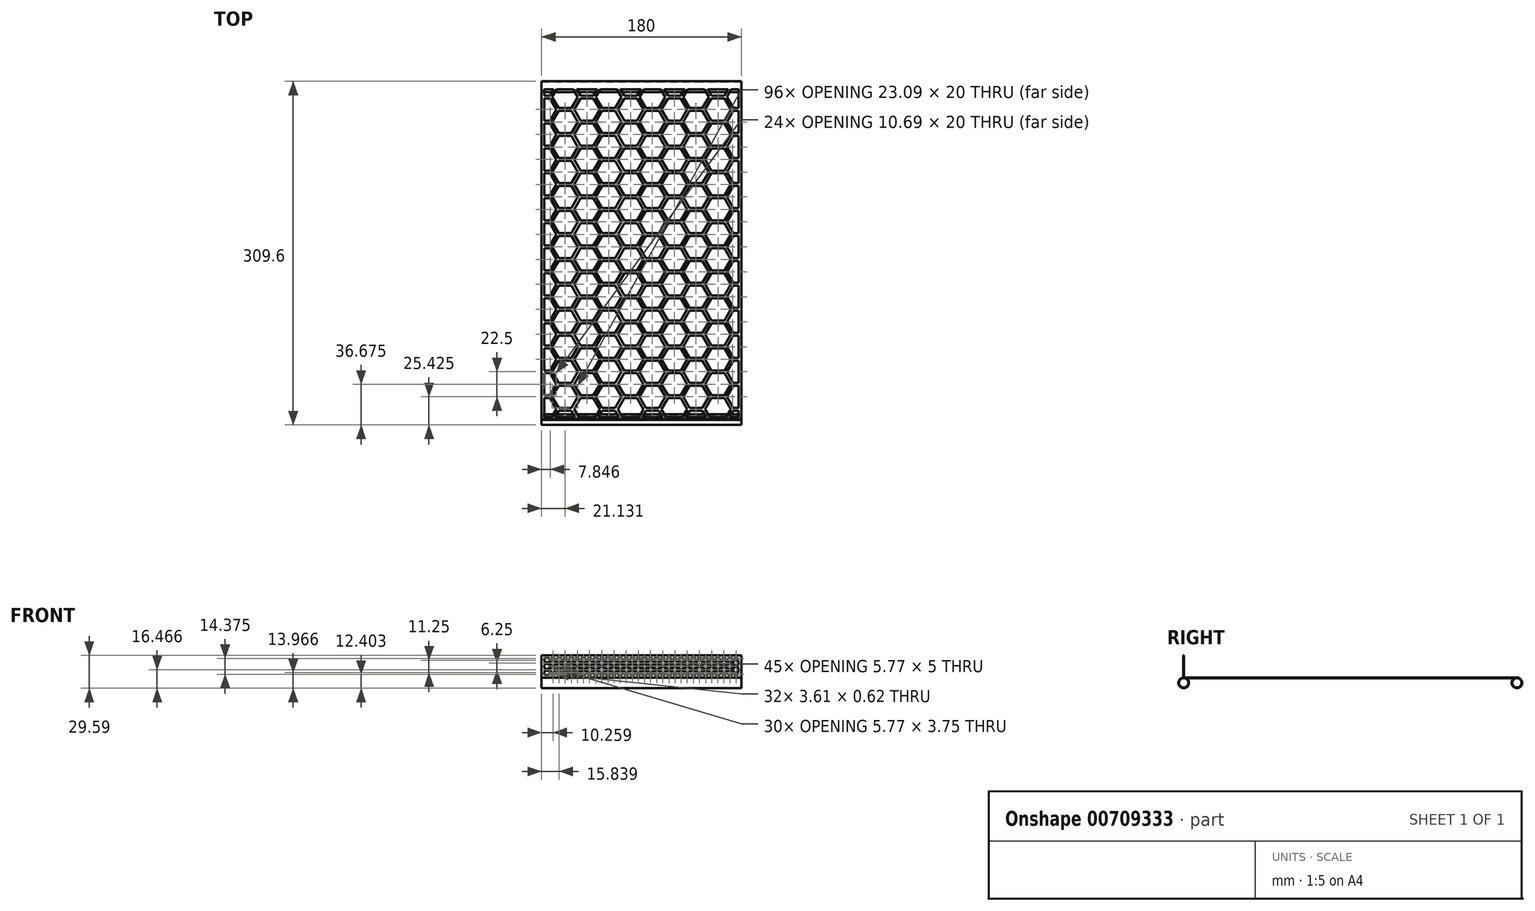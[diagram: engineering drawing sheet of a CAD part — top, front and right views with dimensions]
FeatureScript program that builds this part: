
annotation { "Feature Type Name" : "Feature", "Feature Type Description" : "" }
export const myFeature = defineFeature(function(context is Context, id is Id, definition is map)
    precondition{}
    {
        {
            var Q0;
            Q0=qCreatedBy(makeId("Top.planeOp"),FACE);
            var sketch = newSketch(context, id + "F0", { "sketchPlane" : qUnion([Q0])});
            skLineSegment(sketch, "E0.bottom", {"start": v(90, -150) * mm, "end": v(-90, -150) * mm});
            skLineSegment(sketch, "E0.top", {"start": v(90, 150) * mm, "end": v(-90, 150) * mm});
            skLineSegment(sketch, "E0.left", {"start": v(90, -150) * mm, "end": v(90, 150) * mm});
            skLineSegment(sketch, "E0.right", {"start": v(-90, -150) * mm, "end": v(-90, 150) * mm});
            skPoint(sketch, "E0.middle", {"position": v(0, 0) * mm});
            skSolve(sketch);
        }
        {
            var Q0;
            Q0 = qSketchRegion(id + "F0", true);
            extrude(context, id + "F1", {"entities" : qUnion([Q0]), "endBound" : BoundingType.SYMMETRIC, "depth" : 0.6 * mm, "offsetDistance" : 25 * mm});
        }
        {
            var Q0;
            Q0=qCreatedBy(makeId("Right.planeOp"),FACE);
            var sketch = newSketch(context, id + "F2", { "sketchPlane" : qUnion([Q0])});
            skLineSegment(sketch, "E1.0", {"start": v(-150, 0.3) * mm, "end": v(-150, -0.3) * mm, "construction": true});
            skCircle(sketch, "E2", {"center": v(-150, -4.5) * mm, "radius": 4.2 * mm});
            skCircle(sketch, "E3", {"center": v(-150, -4.5) * mm, "radius": 4.8 * mm});
            skCircle(sketch, "E4.MirrorC", {"center": v(150, -4.5) * mm, "radius": 4.8 * mm});
            skCircle(sketch, "E5.MirrorC", {"center": v(150, -4.5) * mm, "radius": 4.2 * mm});
            skLineSegment(sketch, "E6.bottom", {"start": v(-150.3, 0.3) * mm, "end": v(-149.7, 0.3) * mm});
            skLineSegment(sketch, "E6.top", {"start": v(-150.3, 20.3) * mm, "end": v(-149.7, 20.3) * mm});
            skLineSegment(sketch, "E6.left", {"start": v(-150.3, 0.3) * mm, "end": v(-150.3, 20.3) * mm});
            skLineSegment(sketch, "E6.right", {"start": v(-149.7, 0.3) * mm, "end": v(-149.7, 20.3) * mm});
            skPoint(sketch, "E7", {"position": v(-150, 0.3) * mm});
            skSolve(sketch);
        }
        {
            var Q0;
            Q0 = qSketchRegion(id + "F2", true);
            var Q1;
            Q1=makeQuery(id+"F1.opExtrude","CAP_EDGE",EDGE,{"disambiguationData":[OSD([sQuery(id+"F0.wireOp",EDGE,"E0.bottom")])],"isStart":false});
            sweep(context, id + "F3", {"operationType" : NewBodyOperationType.ADD, "profiles" : qUnion([Q0]), "path" : qUnion([Q1])});
        }
        {
            var Q0;
            Q0=makeQuery(id+"F1.opExtrude","CAP_FACE",FACE,{"disambiguationData":[OSD([sQuery(id+"F0.wireOp",EDGE,"E0.bottom"),sQuery(id+"F0.wireOp",EDGE,"E0.top"),sQuery(id+"F0.wireOp",EDGE,"E0.left"),sQuery(id+"F0.wireOp",EDGE,"E0.right")])],"isStart":false});
            var sketch = newSketch(context, id + "F4", { "sketchPlane" : qUnion([Q0])});
            skPoint(sketch, "E8.0", {"position": v(-90, 147.68) * mm});
            skPoint(sketch, "E9.0", {"position": v(-90, -147.68) * mm});
            skLineSegment(sketch, "E10", {"start": v(-90, 147.68) * mm, "end": v(90, 147.68) * mm});
            skLineSegment(sketch, "E11", {"start": v(-90, -147.68) * mm, "end": v(90, -147.68) * mm});
            skCircle(sketch, "E12.cCircle", {"center": v(-68.87, 163.12) * mm, "radius": 10 * mm, "construction": true});
            skLineSegment(sketch, "E12.0", {"start": v(-63.1, 153.12) * mm, "end": v(-74.64, 153.12) * mm});
            skLineSegment(sketch, "E12.1", {"start": v(-74.64, 153.12) * mm, "end": v(-80.42, 163.12) * mm});
            skLineSegment(sketch, "E12.2", {"start": v(-80.42, 163.12) * mm, "end": v(-74.64, 173.12) * mm});
            skLineSegment(sketch, "E12.3", {"start": v(-74.64, 173.12) * mm, "end": v(-63.1, 173.12) * mm});
            skLineSegment(sketch, "E12.4", {"start": v(-63.1, 173.12) * mm, "end": v(-57.32, 163.12) * mm});
            skLineSegment(sketch, "E12.5", {"start": v(-57.32, 163.12) * mm, "end": v(-63.1, 153.12) * mm});
            skPoint(sketch, "E12.0.midPoint", {"position": v(-68.87, 153.12) * mm});
            skCircle(sketch, "E13.cCircle", {"center": v(-88.35, 151.87) * mm, "radius": 10 * mm, "construction": true});
            skLineSegment(sketch, "E13.0", {"start": v(-82.58, 141.87) * mm, "end": v(-94.13, 141.87) * mm});
            skLineSegment(sketch, "E13.1", {"start": v(-94.13, 141.87) * mm, "end": v(-99.9, 151.87) * mm});
            skLineSegment(sketch, "E13.2", {"start": v(-99.9, 151.87) * mm, "end": v(-94.13, 161.87) * mm});
            skLineSegment(sketch, "E13.3", {"start": v(-94.13, 161.87) * mm, "end": v(-82.58, 161.87) * mm});
            skLineSegment(sketch, "E13.4", {"start": v(-82.58, 161.87) * mm, "end": v(-76.8, 151.87) * mm});
            skLineSegment(sketch, "E13.5", {"start": v(-76.8, 151.87) * mm, "end": v(-82.58, 141.87) * mm});
            skPoint(sketch, "E13.0.midPoint", {"position": v(-88.35, 141.87) * mm});
            skLineSegment(sketch, "E14.0", {"start": v(87.5, -149.7) * mm, "end": v(87.5, 150) * mm});
            skLineSegment(sketch, "E15.0", {"start": v(-87.5, -149.7) * mm, "end": v(-87.5, 150) * mm});
            skLineSegment(sketch, "E16", {"start": v(0, 147.68) * mm, "end": v(0, -147.68) * mm, "construction": true});
            skLineSegment(sketch, "E17", {"start": v(-87.5, 0) * mm, "end": v(87.5, 0) * mm, "construction": true});
            skLineSegment(sketch, "E18.0.1.0", {"start": v(-94.13, 139.37) * mm, "end": v(-82.58, 139.37) * mm});
            skLineSegment(sketch, "E18.0.1.1", {"start": v(-99.9, 129.37) * mm, "end": v(-94.13, 139.37) * mm});
            skLineSegment(sketch, "E18.0.1.2", {"start": v(-94.13, 119.37) * mm, "end": v(-99.9, 129.37) * mm});
            skLineSegment(sketch, "E18.0.1.3", {"start": v(-82.58, 119.37) * mm, "end": v(-94.13, 119.37) * mm});
            skLineSegment(sketch, "E18.0.1.4", {"start": v(-76.8, 129.37) * mm, "end": v(-82.58, 119.37) * mm});
            skLineSegment(sketch, "E18.0.1.5", {"start": v(-82.58, 139.37) * mm, "end": v(-76.8, 129.37) * mm});
            skLineSegment(sketch, "E18.0.1.6", {"start": v(-80.42, 140.62) * mm, "end": v(-74.64, 150.62) * mm});
            skLineSegment(sketch, "E18.0.1.7", {"start": v(-74.64, 130.62) * mm, "end": v(-80.42, 140.62) * mm});
            skLineSegment(sketch, "E18.0.1.8", {"start": v(-74.64, 150.62) * mm, "end": v(-63.1, 150.62) * mm});
            skLineSegment(sketch, "E18.0.1.9", {"start": v(-63.1, 150.62) * mm, "end": v(-57.32, 140.62) * mm});
            skLineSegment(sketch, "E18.0.1.10", {"start": v(-57.32, 140.62) * mm, "end": v(-63.1, 130.62) * mm});
            skLineSegment(sketch, "E18.0.1.11", {"start": v(-63.1, 130.62) * mm, "end": v(-74.64, 130.62) * mm});
            skLineSegment(sketch, "E18.1.0.0", {"start": v(-54.82, 161.87) * mm, "end": v(-43.28, 161.87) * mm});
            skLineSegment(sketch, "E18.1.0.1", {"start": v(-60.6, 151.87) * mm, "end": v(-54.82, 161.87) * mm});
            skLineSegment(sketch, "E18.1.0.2", {"start": v(-54.82, 141.87) * mm, "end": v(-60.6, 151.87) * mm});
            skLineSegment(sketch, "E18.1.0.3", {"start": v(-43.28, 141.87) * mm, "end": v(-54.82, 141.87) * mm});
            skLineSegment(sketch, "E18.1.0.4", {"start": v(-37.5, 151.87) * mm, "end": v(-43.28, 141.87) * mm});
            skLineSegment(sketch, "E18.1.0.5", {"start": v(-43.28, 161.87) * mm, "end": v(-37.5, 151.87) * mm});
            skLineSegment(sketch, "E18.1.0.6", {"start": v(-41.11, 163.12) * mm, "end": v(-35.34, 173.12) * mm});
            skLineSegment(sketch, "E18.1.0.7", {"start": v(-35.34, 153.12) * mm, "end": v(-41.11, 163.12) * mm});
            skLineSegment(sketch, "E18.1.0.8", {"start": v(-35.34, 173.12) * mm, "end": v(-23.79, 173.12) * mm});
            skLineSegment(sketch, "E18.1.0.9", {"start": v(-23.79, 173.12) * mm, "end": v(-18.02, 163.12) * mm});
            skLineSegment(sketch, "E18.1.0.10", {"start": v(-18.02, 163.12) * mm, "end": v(-23.79, 153.12) * mm});
            skLineSegment(sketch, "E18.1.0.11", {"start": v(-23.79, 153.12) * mm, "end": v(-35.34, 153.12) * mm});
            skLineSegment(sketch, "E18.1.1.0", {"start": v(-54.82, 139.37) * mm, "end": v(-43.28, 139.37) * mm});
            skLineSegment(sketch, "E18.1.1.1", {"start": v(-60.6, 129.37) * mm, "end": v(-54.82, 139.37) * mm});
            skLineSegment(sketch, "E18.1.1.2", {"start": v(-54.82, 119.37) * mm, "end": v(-60.6, 129.37) * mm});
            skLineSegment(sketch, "E18.1.1.3", {"start": v(-43.28, 119.37) * mm, "end": v(-54.82, 119.37) * mm});
            skLineSegment(sketch, "E18.1.1.4", {"start": v(-37.5, 129.37) * mm, "end": v(-43.28, 119.37) * mm});
            skLineSegment(sketch, "E18.1.1.5", {"start": v(-43.28, 139.37) * mm, "end": v(-37.5, 129.37) * mm});
            skLineSegment(sketch, "E18.1.1.6", {"start": v(-41.11, 140.62) * mm, "end": v(-35.34, 150.62) * mm});
            skLineSegment(sketch, "E18.1.1.7", {"start": v(-35.34, 130.62) * mm, "end": v(-41.11, 140.62) * mm});
            skLineSegment(sketch, "E18.1.1.8", {"start": v(-35.34, 150.62) * mm, "end": v(-23.79, 150.62) * mm});
            skLineSegment(sketch, "E18.1.1.9", {"start": v(-23.79, 150.62) * mm, "end": v(-18.02, 140.62) * mm});
            skLineSegment(sketch, "E18.1.1.10", {"start": v(-18.02, 140.62) * mm, "end": v(-23.79, 130.62) * mm});
            skLineSegment(sketch, "E18.1.1.11", {"start": v(-23.79, 130.62) * mm, "end": v(-35.34, 130.62) * mm});
            skLineSegment(sketch, "E18.2.0.0", {"start": v(-15.52, 161.87) * mm, "end": v(-3.97, 161.87) * mm});
            skLineSegment(sketch, "E18.2.0.1", {"start": v(-21.29, 151.87) * mm, "end": v(-15.52, 161.87) * mm});
            skLineSegment(sketch, "E18.2.0.2", {"start": v(-15.52, 141.87) * mm, "end": v(-21.29, 151.87) * mm});
            skLineSegment(sketch, "E18.2.0.3", {"start": v(-3.97, 141.87) * mm, "end": v(-15.52, 141.87) * mm});
            skLineSegment(sketch, "E18.2.0.4", {"start": v(1.8, 151.87) * mm, "end": v(-3.97, 141.87) * mm});
            skLineSegment(sketch, "E18.2.0.5", {"start": v(-3.97, 161.87) * mm, "end": v(1.8, 151.87) * mm});
            skLineSegment(sketch, "E18.2.0.6", {"start": v(-1.8, 163.12) * mm, "end": v(3.97, 173.12) * mm});
            skLineSegment(sketch, "E18.2.0.7", {"start": v(3.97, 153.12) * mm, "end": v(-1.8, 163.12) * mm});
            skLineSegment(sketch, "E18.2.0.8", {"start": v(3.97, 173.12) * mm, "end": v(15.52, 173.12) * mm});
            skLineSegment(sketch, "E18.2.0.9", {"start": v(15.52, 173.12) * mm, "end": v(21.29, 163.12) * mm});
            skLineSegment(sketch, "E18.2.0.10", {"start": v(21.29, 163.12) * mm, "end": v(15.52, 153.12) * mm});
            skLineSegment(sketch, "E18.2.0.11", {"start": v(15.52, 153.12) * mm, "end": v(3.97, 153.12) * mm});
            skLineSegment(sketch, "E18.2.1.0", {"start": v(-15.52, 139.37) * mm, "end": v(-3.97, 139.37) * mm});
            skLineSegment(sketch, "E18.2.1.1", {"start": v(-21.29, 129.37) * mm, "end": v(-15.52, 139.37) * mm});
            skLineSegment(sketch, "E18.2.1.2", {"start": v(-15.52, 119.37) * mm, "end": v(-21.29, 129.37) * mm});
            skLineSegment(sketch, "E18.2.1.3", {"start": v(-3.97, 119.37) * mm, "end": v(-15.52, 119.37) * mm});
            skLineSegment(sketch, "E18.2.1.4", {"start": v(1.8, 129.37) * mm, "end": v(-3.97, 119.37) * mm});
            skLineSegment(sketch, "E18.2.1.5", {"start": v(-3.97, 139.37) * mm, "end": v(1.8, 129.37) * mm});
            skLineSegment(sketch, "E18.2.1.6", {"start": v(-1.8, 140.62) * mm, "end": v(3.97, 150.62) * mm});
            skLineSegment(sketch, "E18.2.1.7", {"start": v(3.97, 130.62) * mm, "end": v(-1.8, 140.62) * mm});
            skLineSegment(sketch, "E18.2.1.8", {"start": v(3.97, 150.62) * mm, "end": v(15.52, 150.62) * mm});
            skLineSegment(sketch, "E18.2.1.9", {"start": v(15.52, 150.62) * mm, "end": v(21.29, 140.62) * mm});
            skLineSegment(sketch, "E18.2.1.10", {"start": v(21.29, 140.62) * mm, "end": v(15.52, 130.62) * mm});
            skLineSegment(sketch, "E18.2.1.11", {"start": v(15.52, 130.62) * mm, "end": v(3.97, 130.62) * mm});
            skLineSegment(sketch, "E18.direction1", {"start": v(-94.13, 161.87) * mm, "end": v(-54.82, 161.87) * mm, "construction": true});
            skLineSegment(sketch, "E18.direction2", {"start": v(-94.13, 161.87) * mm, "end": v(-94.13, 139.37) * mm, "construction": true});
            skLineSegment(sketch, "E19.0.3.0", {"start": v(23.79, 161.87) * mm, "end": v(35.34, 161.87) * mm});
            skLineSegment(sketch, "E19.3.3.0", {"start": v(18.02, 151.87) * mm, "end": v(23.79, 161.87) * mm});
            skLineSegment(sketch, "E19.6.3.0", {"start": v(23.79, 141.87) * mm, "end": v(18.02, 151.87) * mm});
            skLineSegment(sketch, "E19.9.3.0", {"start": v(35.34, 141.87) * mm, "end": v(23.79, 141.87) * mm});
            skLineSegment(sketch, "E19.12.3.0", {"start": v(41.11, 151.87) * mm, "end": v(35.34, 141.87) * mm});
            skLineSegment(sketch, "E19.15.3.0", {"start": v(35.34, 161.87) * mm, "end": v(41.11, 151.87) * mm});
            skLineSegment(sketch, "E19.18.3.0", {"start": v(37.5, 163.12) * mm, "end": v(43.28, 173.12) * mm});
            skLineSegment(sketch, "E19.21.3.0", {"start": v(43.28, 153.12) * mm, "end": v(37.5, 163.12) * mm});
            skLineSegment(sketch, "E19.24.3.0", {"start": v(43.28, 173.12) * mm, "end": v(54.82, 173.12) * mm});
            skLineSegment(sketch, "E19.27.3.0", {"start": v(54.82, 173.12) * mm, "end": v(60.6, 163.12) * mm});
            skLineSegment(sketch, "E19.30.3.0", {"start": v(60.6, 163.12) * mm, "end": v(54.82, 153.12) * mm});
            skLineSegment(sketch, "E19.33.3.0", {"start": v(54.82, 153.12) * mm, "end": v(43.28, 153.12) * mm});
            skLineSegment(sketch, "E19.0.3.1", {"start": v(23.79, 139.37) * mm, "end": v(35.34, 139.37) * mm});
            skLineSegment(sketch, "E19.3.3.1", {"start": v(18.02, 129.37) * mm, "end": v(23.79, 139.37) * mm});
            skLineSegment(sketch, "E19.6.3.1", {"start": v(23.79, 119.37) * mm, "end": v(18.02, 129.37) * mm});
            skLineSegment(sketch, "E19.9.3.1", {"start": v(35.34, 119.37) * mm, "end": v(23.79, 119.37) * mm});
            skLineSegment(sketch, "E19.12.3.1", {"start": v(41.11, 129.37) * mm, "end": v(35.34, 119.37) * mm});
            skLineSegment(sketch, "E19.15.3.1", {"start": v(35.34, 139.37) * mm, "end": v(41.11, 129.37) * mm});
            skLineSegment(sketch, "E19.18.3.1", {"start": v(37.5, 140.62) * mm, "end": v(43.28, 150.62) * mm});
            skLineSegment(sketch, "E19.21.3.1", {"start": v(43.28, 130.62) * mm, "end": v(37.5, 140.62) * mm});
            skLineSegment(sketch, "E19.24.3.1", {"start": v(43.28, 150.62) * mm, "end": v(54.82, 150.62) * mm});
            skLineSegment(sketch, "E19.27.3.1", {"start": v(54.82, 150.62) * mm, "end": v(60.6, 140.62) * mm});
            skLineSegment(sketch, "E19.30.3.1", {"start": v(60.6, 140.62) * mm, "end": v(54.82, 130.62) * mm});
            skLineSegment(sketch, "E19.33.3.1", {"start": v(54.82, 130.62) * mm, "end": v(43.28, 130.62) * mm});
            skLineSegment(sketch, "E19.0.4.0", {"start": v(63.1, 161.87) * mm, "end": v(74.64, 161.87) * mm});
            skLineSegment(sketch, "E19.3.4.0", {"start": v(57.32, 151.87) * mm, "end": v(63.1, 161.87) * mm});
            skLineSegment(sketch, "E19.6.4.0", {"start": v(63.1, 141.87) * mm, "end": v(57.32, 151.87) * mm});
            skLineSegment(sketch, "E19.9.4.0", {"start": v(74.64, 141.87) * mm, "end": v(63.1, 141.87) * mm});
            skLineSegment(sketch, "E19.12.4.0", {"start": v(80.42, 151.87) * mm, "end": v(74.64, 141.87) * mm});
            skLineSegment(sketch, "E19.15.4.0", {"start": v(74.64, 161.87) * mm, "end": v(80.42, 151.87) * mm});
            skLineSegment(sketch, "E19.18.4.0", {"start": v(76.8, 163.12) * mm, "end": v(82.58, 173.12) * mm});
            skLineSegment(sketch, "E19.21.4.0", {"start": v(82.58, 153.12) * mm, "end": v(76.8, 163.12) * mm});
            skLineSegment(sketch, "E19.24.4.0", {"start": v(82.58, 173.12) * mm, "end": v(94.13, 173.12) * mm});
            skLineSegment(sketch, "E19.27.4.0", {"start": v(94.13, 173.12) * mm, "end": v(99.9, 163.12) * mm});
            skLineSegment(sketch, "E19.30.4.0", {"start": v(99.9, 163.12) * mm, "end": v(94.13, 153.12) * mm});
            skLineSegment(sketch, "E19.33.4.0", {"start": v(94.13, 153.12) * mm, "end": v(82.58, 153.12) * mm});
            skLineSegment(sketch, "E19.0.4.1", {"start": v(63.1, 139.37) * mm, "end": v(74.64, 139.37) * mm});
            skLineSegment(sketch, "E19.3.4.1", {"start": v(57.32, 129.37) * mm, "end": v(63.1, 139.37) * mm});
            skLineSegment(sketch, "E19.6.4.1", {"start": v(63.1, 119.37) * mm, "end": v(57.32, 129.37) * mm});
            skLineSegment(sketch, "E19.9.4.1", {"start": v(74.64, 119.37) * mm, "end": v(63.1, 119.37) * mm});
            skLineSegment(sketch, "E19.12.4.1", {"start": v(80.42, 129.37) * mm, "end": v(74.64, 119.37) * mm});
            skLineSegment(sketch, "E19.15.4.1", {"start": v(74.64, 139.37) * mm, "end": v(80.42, 129.37) * mm});
            skLineSegment(sketch, "E19.18.4.1", {"start": v(76.8, 140.62) * mm, "end": v(82.58, 150.62) * mm});
            skLineSegment(sketch, "E19.21.4.1", {"start": v(82.58, 130.62) * mm, "end": v(76.8, 140.62) * mm});
            skLineSegment(sketch, "E19.24.4.1", {"start": v(82.58, 150.62) * mm, "end": v(94.13, 150.62) * mm});
            skLineSegment(sketch, "E19.27.4.1", {"start": v(94.13, 150.62) * mm, "end": v(99.9, 140.62) * mm});
            skLineSegment(sketch, "E19.30.4.1", {"start": v(99.9, 140.62) * mm, "end": v(94.13, 130.62) * mm});
            skLineSegment(sketch, "E19.33.4.1", {"start": v(94.13, 130.62) * mm, "end": v(82.58, 130.62) * mm});
            skLineSegment(sketch, "E20.0.0.2", {"start": v(-94.13, 116.87) * mm, "end": v(-82.58, 116.87) * mm});
            skLineSegment(sketch, "E20.3.0.2", {"start": v(-99.9, 106.87) * mm, "end": v(-94.13, 116.87) * mm});
            skLineSegment(sketch, "E20.6.0.2", {"start": v(-94.13, 96.87) * mm, "end": v(-99.9, 106.87) * mm});
            skLineSegment(sketch, "E20.9.0.2", {"start": v(-82.58, 96.87) * mm, "end": v(-94.13, 96.87) * mm});
            skLineSegment(sketch, "E20.12.0.2", {"start": v(-76.8, 106.87) * mm, "end": v(-82.58, 96.87) * mm});
            skLineSegment(sketch, "E20.15.0.2", {"start": v(-82.58, 116.87) * mm, "end": v(-76.8, 106.87) * mm});
            skLineSegment(sketch, "E20.18.0.2", {"start": v(-80.42, 118.12) * mm, "end": v(-74.64, 128.12) * mm});
            skLineSegment(sketch, "E20.21.0.2", {"start": v(-74.64, 108.12) * mm, "end": v(-80.42, 118.12) * mm});
            skLineSegment(sketch, "E20.24.0.2", {"start": v(-74.64, 128.12) * mm, "end": v(-63.1, 128.12) * mm});
            skLineSegment(sketch, "E20.27.0.2", {"start": v(-63.1, 128.12) * mm, "end": v(-57.32, 118.12) * mm});
            skLineSegment(sketch, "E20.30.0.2", {"start": v(-57.32, 118.12) * mm, "end": v(-63.1, 108.12) * mm});
            skLineSegment(sketch, "E20.33.0.2", {"start": v(-63.1, 108.12) * mm, "end": v(-74.64, 108.12) * mm});
            skLineSegment(sketch, "E20.0.0.3", {"start": v(-94.13, 94.37) * mm, "end": v(-82.58, 94.37) * mm});
            skLineSegment(sketch, "E20.3.0.3", {"start": v(-99.9, 84.37) * mm, "end": v(-94.13, 94.37) * mm});
            skLineSegment(sketch, "E20.6.0.3", {"start": v(-94.13, 74.37) * mm, "end": v(-99.9, 84.37) * mm});
            skLineSegment(sketch, "E20.9.0.3", {"start": v(-82.58, 74.37) * mm, "end": v(-94.13, 74.37) * mm});
            skLineSegment(sketch, "E20.12.0.3", {"start": v(-76.8, 84.37) * mm, "end": v(-82.58, 74.37) * mm});
            skLineSegment(sketch, "E20.15.0.3", {"start": v(-82.58, 94.37) * mm, "end": v(-76.8, 84.37) * mm});
            skLineSegment(sketch, "E20.18.0.3", {"start": v(-80.42, 95.62) * mm, "end": v(-74.64, 105.62) * mm});
            skLineSegment(sketch, "E20.21.0.3", {"start": v(-74.64, 85.62) * mm, "end": v(-80.42, 95.62) * mm});
            skLineSegment(sketch, "E20.24.0.3", {"start": v(-74.64, 105.62) * mm, "end": v(-63.1, 105.62) * mm});
            skLineSegment(sketch, "E20.27.0.3", {"start": v(-63.1, 105.62) * mm, "end": v(-57.32, 95.62) * mm});
            skLineSegment(sketch, "E20.30.0.3", {"start": v(-57.32, 95.62) * mm, "end": v(-63.1, 85.62) * mm});
            skLineSegment(sketch, "E20.33.0.3", {"start": v(-63.1, 85.62) * mm, "end": v(-74.64, 85.62) * mm});
            skLineSegment(sketch, "E20.0.0.4", {"start": v(-94.13, 71.87) * mm, "end": v(-82.58, 71.87) * mm});
            skLineSegment(sketch, "E20.3.0.4", {"start": v(-99.9, 61.87) * mm, "end": v(-94.13, 71.87) * mm});
            skLineSegment(sketch, "E20.6.0.4", {"start": v(-94.13, 51.87) * mm, "end": v(-99.9, 61.87) * mm});
            skLineSegment(sketch, "E20.9.0.4", {"start": v(-82.58, 51.87) * mm, "end": v(-94.13, 51.87) * mm});
            skLineSegment(sketch, "E20.12.0.4", {"start": v(-76.8, 61.87) * mm, "end": v(-82.58, 51.87) * mm});
            skLineSegment(sketch, "E20.15.0.4", {"start": v(-82.58, 71.87) * mm, "end": v(-76.8, 61.87) * mm});
            skLineSegment(sketch, "E20.18.0.4", {"start": v(-80.42, 73.12) * mm, "end": v(-74.64, 83.12) * mm});
            skLineSegment(sketch, "E20.21.0.4", {"start": v(-74.64, 63.12) * mm, "end": v(-80.42, 73.12) * mm});
            skLineSegment(sketch, "E20.24.0.4", {"start": v(-74.64, 83.12) * mm, "end": v(-63.1, 83.12) * mm});
            skLineSegment(sketch, "E20.27.0.4", {"start": v(-63.1, 83.12) * mm, "end": v(-57.32, 73.12) * mm});
            skLineSegment(sketch, "E20.30.0.4", {"start": v(-57.32, 73.12) * mm, "end": v(-63.1, 63.12) * mm});
            skLineSegment(sketch, "E20.33.0.4", {"start": v(-63.1, 63.12) * mm, "end": v(-74.64, 63.12) * mm});
            skLineSegment(sketch, "E20.0.0.5", {"start": v(-94.13, 49.37) * mm, "end": v(-82.58, 49.37) * mm});
            skLineSegment(sketch, "E20.3.0.5", {"start": v(-99.9, 39.37) * mm, "end": v(-94.13, 49.37) * mm});
            skLineSegment(sketch, "E20.6.0.5", {"start": v(-94.13, 29.37) * mm, "end": v(-99.9, 39.37) * mm});
            skLineSegment(sketch, "E20.9.0.5", {"start": v(-82.58, 29.37) * mm, "end": v(-94.13, 29.37) * mm});
            skLineSegment(sketch, "E20.12.0.5", {"start": v(-76.8, 39.37) * mm, "end": v(-82.58, 29.37) * mm});
            skLineSegment(sketch, "E20.15.0.5", {"start": v(-82.58, 49.37) * mm, "end": v(-76.8, 39.37) * mm});
            skLineSegment(sketch, "E20.18.0.5", {"start": v(-80.42, 50.62) * mm, "end": v(-74.64, 60.62) * mm});
            skLineSegment(sketch, "E20.21.0.5", {"start": v(-74.64, 40.62) * mm, "end": v(-80.42, 50.62) * mm});
            skLineSegment(sketch, "E20.24.0.5", {"start": v(-74.64, 60.62) * mm, "end": v(-63.1, 60.62) * mm});
            skLineSegment(sketch, "E20.27.0.5", {"start": v(-63.1, 60.62) * mm, "end": v(-57.32, 50.62) * mm});
            skLineSegment(sketch, "E20.30.0.5", {"start": v(-57.32, 50.62) * mm, "end": v(-63.1, 40.62) * mm});
            skLineSegment(sketch, "E20.33.0.5", {"start": v(-63.1, 40.62) * mm, "end": v(-74.64, 40.62) * mm});
            skLineSegment(sketch, "E20.0.0.6", {"start": v(-94.13, 26.87) * mm, "end": v(-82.58, 26.87) * mm});
            skLineSegment(sketch, "E20.3.0.6", {"start": v(-99.9, 16.87) * mm, "end": v(-94.13, 26.87) * mm});
            skLineSegment(sketch, "E20.6.0.6", {"start": v(-94.13, 6.87) * mm, "end": v(-99.9, 16.87) * mm});
            skLineSegment(sketch, "E20.9.0.6", {"start": v(-82.58, 6.87) * mm, "end": v(-94.13, 6.87) * mm});
            skLineSegment(sketch, "E20.12.0.6", {"start": v(-76.8, 16.87) * mm, "end": v(-82.58, 6.87) * mm});
            skLineSegment(sketch, "E20.15.0.6", {"start": v(-82.58, 26.87) * mm, "end": v(-76.8, 16.87) * mm});
            skLineSegment(sketch, "E20.18.0.6", {"start": v(-80.42, 28.12) * mm, "end": v(-74.64, 38.12) * mm});
            skLineSegment(sketch, "E20.21.0.6", {"start": v(-74.64, 18.12) * mm, "end": v(-80.42, 28.12) * mm});
            skLineSegment(sketch, "E20.24.0.6", {"start": v(-74.64, 38.12) * mm, "end": v(-63.1, 38.12) * mm});
            skLineSegment(sketch, "E20.27.0.6", {"start": v(-63.1, 38.12) * mm, "end": v(-57.32, 28.12) * mm});
            skLineSegment(sketch, "E20.30.0.6", {"start": v(-57.32, 28.12) * mm, "end": v(-63.1, 18.12) * mm});
            skLineSegment(sketch, "E20.33.0.6", {"start": v(-63.1, 18.12) * mm, "end": v(-74.64, 18.12) * mm});
            skLineSegment(sketch, "E20.0.0.7", {"start": v(-94.13, 4.37) * mm, "end": v(-82.58, 4.37) * mm});
            skLineSegment(sketch, "E20.3.0.7", {"start": v(-99.9, -5.63) * mm, "end": v(-94.13, 4.37) * mm});
            skLineSegment(sketch, "E20.6.0.7", {"start": v(-94.13, -15.63) * mm, "end": v(-99.9, -5.63) * mm});
            skLineSegment(sketch, "E20.9.0.7", {"start": v(-82.58, -15.63) * mm, "end": v(-94.13, -15.63) * mm});
            skLineSegment(sketch, "E20.12.0.7", {"start": v(-76.8, -5.63) * mm, "end": v(-82.58, -15.63) * mm});
            skLineSegment(sketch, "E20.15.0.7", {"start": v(-82.58, 4.37) * mm, "end": v(-76.8, -5.63) * mm});
            skLineSegment(sketch, "E20.18.0.7", {"start": v(-80.42, 5.62) * mm, "end": v(-74.64, 15.62) * mm});
            skLineSegment(sketch, "E20.21.0.7", {"start": v(-74.64, -4.38) * mm, "end": v(-80.42, 5.62) * mm});
            skLineSegment(sketch, "E20.24.0.7", {"start": v(-74.64, 15.62) * mm, "end": v(-63.1, 15.62) * mm});
            skLineSegment(sketch, "E20.27.0.7", {"start": v(-63.1, 15.62) * mm, "end": v(-57.32, 5.62) * mm});
            skLineSegment(sketch, "E20.30.0.7", {"start": v(-57.32, 5.62) * mm, "end": v(-63.1, -4.38) * mm});
            skLineSegment(sketch, "E20.33.0.7", {"start": v(-63.1, -4.38) * mm, "end": v(-74.64, -4.38) * mm});
            skLineSegment(sketch, "E20.0.0.8", {"start": v(-94.13, -18.13) * mm, "end": v(-82.58, -18.13) * mm});
            skLineSegment(sketch, "E20.3.0.8", {"start": v(-99.9, -28.13) * mm, "end": v(-94.13, -18.13) * mm});
            skLineSegment(sketch, "E20.6.0.8", {"start": v(-94.13, -38.13) * mm, "end": v(-99.9, -28.13) * mm});
            skLineSegment(sketch, "E20.9.0.8", {"start": v(-82.58, -38.13) * mm, "end": v(-94.13, -38.13) * mm});
            skLineSegment(sketch, "E20.12.0.8", {"start": v(-76.8, -28.13) * mm, "end": v(-82.58, -38.13) * mm});
            skLineSegment(sketch, "E20.15.0.8", {"start": v(-82.58, -18.13) * mm, "end": v(-76.8, -28.13) * mm});
            skLineSegment(sketch, "E20.18.0.8", {"start": v(-80.42, -16.88) * mm, "end": v(-74.64, -6.88) * mm});
            skLineSegment(sketch, "E20.21.0.8", {"start": v(-74.64, -26.88) * mm, "end": v(-80.42, -16.88) * mm});
            skLineSegment(sketch, "E20.24.0.8", {"start": v(-74.64, -6.88) * mm, "end": v(-63.1, -6.88) * mm});
            skLineSegment(sketch, "E20.27.0.8", {"start": v(-63.1, -6.88) * mm, "end": v(-57.32, -16.88) * mm});
            skLineSegment(sketch, "E20.30.0.8", {"start": v(-57.32, -16.88) * mm, "end": v(-63.1, -26.88) * mm});
            skLineSegment(sketch, "E20.33.0.8", {"start": v(-63.1, -26.88) * mm, "end": v(-74.64, -26.88) * mm});
            skLineSegment(sketch, "E20.0.0.9", {"start": v(-94.13, -40.63) * mm, "end": v(-82.58, -40.63) * mm});
            skLineSegment(sketch, "E20.3.0.9", {"start": v(-99.9, -50.63) * mm, "end": v(-94.13, -40.63) * mm});
            skLineSegment(sketch, "E20.6.0.9", {"start": v(-94.13, -60.63) * mm, "end": v(-99.9, -50.63) * mm});
            skLineSegment(sketch, "E20.9.0.9", {"start": v(-82.58, -60.63) * mm, "end": v(-94.13, -60.63) * mm});
            skLineSegment(sketch, "E20.12.0.9", {"start": v(-76.8, -50.63) * mm, "end": v(-82.58, -60.63) * mm});
            skLineSegment(sketch, "E20.15.0.9", {"start": v(-82.58, -40.63) * mm, "end": v(-76.8, -50.63) * mm});
            skLineSegment(sketch, "E20.18.0.9", {"start": v(-80.42, -39.38) * mm, "end": v(-74.64, -29.38) * mm});
            skLineSegment(sketch, "E20.21.0.9", {"start": v(-74.64, -49.38) * mm, "end": v(-80.42, -39.38) * mm});
            skLineSegment(sketch, "E20.24.0.9", {"start": v(-74.64, -29.38) * mm, "end": v(-63.1, -29.38) * mm});
            skLineSegment(sketch, "E20.27.0.9", {"start": v(-63.1, -29.38) * mm, "end": v(-57.32, -39.38) * mm});
            skLineSegment(sketch, "E20.30.0.9", {"start": v(-57.32, -39.38) * mm, "end": v(-63.1, -49.38) * mm});
            skLineSegment(sketch, "E20.33.0.9", {"start": v(-63.1, -49.38) * mm, "end": v(-74.64, -49.38) * mm});
            skLineSegment(sketch, "E20.0.0.10", {"start": v(-94.13, -63.13) * mm, "end": v(-82.58, -63.13) * mm});
            skLineSegment(sketch, "E20.3.0.10", {"start": v(-99.9, -73.13) * mm, "end": v(-94.13, -63.13) * mm});
            skLineSegment(sketch, "E20.6.0.10", {"start": v(-94.13, -83.13) * mm, "end": v(-99.9, -73.13) * mm});
            skLineSegment(sketch, "E20.9.0.10", {"start": v(-82.58, -83.13) * mm, "end": v(-94.13, -83.13) * mm});
            skLineSegment(sketch, "E20.12.0.10", {"start": v(-76.8, -73.13) * mm, "end": v(-82.58, -83.13) * mm});
            skLineSegment(sketch, "E20.15.0.10", {"start": v(-82.58, -63.13) * mm, "end": v(-76.8, -73.13) * mm});
            skLineSegment(sketch, "E20.18.0.10", {"start": v(-80.42, -61.88) * mm, "end": v(-74.64, -51.88) * mm});
            skLineSegment(sketch, "E20.21.0.10", {"start": v(-74.64, -71.88) * mm, "end": v(-80.42, -61.88) * mm});
            skLineSegment(sketch, "E20.24.0.10", {"start": v(-74.64, -51.88) * mm, "end": v(-63.1, -51.88) * mm});
            skLineSegment(sketch, "E20.27.0.10", {"start": v(-63.1, -51.88) * mm, "end": v(-57.32, -61.88) * mm});
            skLineSegment(sketch, "E20.30.0.10", {"start": v(-57.32, -61.88) * mm, "end": v(-63.1, -71.88) * mm});
            skLineSegment(sketch, "E20.33.0.10", {"start": v(-63.1, -71.88) * mm, "end": v(-74.64, -71.88) * mm});
            skLineSegment(sketch, "E20.0.0.11", {"start": v(-94.13, -85.63) * mm, "end": v(-82.58, -85.63) * mm});
            skLineSegment(sketch, "E20.3.0.11", {"start": v(-99.9, -95.63) * mm, "end": v(-94.13, -85.63) * mm});
            skLineSegment(sketch, "E20.6.0.11", {"start": v(-94.13, -105.63) * mm, "end": v(-99.9, -95.63) * mm});
            skLineSegment(sketch, "E20.9.0.11", {"start": v(-82.58, -105.63) * mm, "end": v(-94.13, -105.63) * mm});
            skLineSegment(sketch, "E20.12.0.11", {"start": v(-76.8, -95.63) * mm, "end": v(-82.58, -105.63) * mm});
            skLineSegment(sketch, "E20.15.0.11", {"start": v(-82.58, -85.62) * mm, "end": v(-76.8, -95.63) * mm});
            skLineSegment(sketch, "E20.18.0.11", {"start": v(-80.42, -84.38) * mm, "end": v(-74.64, -74.38) * mm});
            skLineSegment(sketch, "E20.21.0.11", {"start": v(-74.64, -94.38) * mm, "end": v(-80.42, -84.38) * mm});
            skLineSegment(sketch, "E20.24.0.11", {"start": v(-74.64, -74.38) * mm, "end": v(-63.1, -74.38) * mm});
            skLineSegment(sketch, "E20.27.0.11", {"start": v(-63.1, -74.38) * mm, "end": v(-57.32, -84.38) * mm});
            skLineSegment(sketch, "E20.30.0.11", {"start": v(-57.32, -84.38) * mm, "end": v(-63.1, -94.38) * mm});
            skLineSegment(sketch, "E20.33.0.11", {"start": v(-63.1, -94.38) * mm, "end": v(-74.64, -94.38) * mm});
            skLineSegment(sketch, "E20.0.0.12", {"start": v(-94.13, -108.13) * mm, "end": v(-82.58, -108.13) * mm});
            skLineSegment(sketch, "E20.3.0.12", {"start": v(-99.9, -118.13) * mm, "end": v(-94.13, -108.13) * mm});
            skLineSegment(sketch, "E20.6.0.12", {"start": v(-94.13, -128.13) * mm, "end": v(-99.9, -118.13) * mm});
            skLineSegment(sketch, "E20.9.0.12", {"start": v(-82.58, -128.13) * mm, "end": v(-94.13, -128.13) * mm});
            skLineSegment(sketch, "E20.12.0.12", {"start": v(-76.8, -118.13) * mm, "end": v(-82.58, -128.13) * mm});
            skLineSegment(sketch, "E20.15.0.12", {"start": v(-82.58, -108.13) * mm, "end": v(-76.8, -118.13) * mm});
            skLineSegment(sketch, "E20.18.0.12", {"start": v(-80.42, -106.88) * mm, "end": v(-74.64, -96.88) * mm});
            skLineSegment(sketch, "E20.21.0.12", {"start": v(-74.64, -116.87) * mm, "end": v(-80.42, -106.88) * mm});
            skLineSegment(sketch, "E20.24.0.12", {"start": v(-74.64, -96.88) * mm, "end": v(-63.1, -96.88) * mm});
            skLineSegment(sketch, "E20.27.0.12", {"start": v(-63.1, -96.88) * mm, "end": v(-57.32, -106.88) * mm});
            skLineSegment(sketch, "E20.30.0.12", {"start": v(-57.32, -106.88) * mm, "end": v(-63.1, -116.88) * mm});
            skLineSegment(sketch, "E20.33.0.12", {"start": v(-63.1, -116.88) * mm, "end": v(-74.64, -116.88) * mm});
            skLineSegment(sketch, "E20.0.0.13", {"start": v(-94.13, -130.62) * mm, "end": v(-82.58, -130.62) * mm});
            skLineSegment(sketch, "E20.3.0.13", {"start": v(-99.9, -140.63) * mm, "end": v(-94.13, -130.63) * mm});
            skLineSegment(sketch, "E20.6.0.13", {"start": v(-94.13, -150.63) * mm, "end": v(-99.9, -140.63) * mm});
            skLineSegment(sketch, "E20.9.0.13", {"start": v(-82.58, -150.62) * mm, "end": v(-94.13, -150.62) * mm});
            skLineSegment(sketch, "E20.12.0.13", {"start": v(-76.8, -140.62) * mm, "end": v(-82.58, -150.62) * mm});
            skLineSegment(sketch, "E20.15.0.13", {"start": v(-82.58, -130.62) * mm, "end": v(-76.8, -140.62) * mm});
            skLineSegment(sketch, "E20.18.0.13", {"start": v(-80.42, -129.38) * mm, "end": v(-74.64, -119.38) * mm});
            skLineSegment(sketch, "E20.21.0.13", {"start": v(-74.64, -139.37) * mm, "end": v(-80.42, -129.38) * mm});
            skLineSegment(sketch, "E20.24.0.13", {"start": v(-74.64, -119.37) * mm, "end": v(-63.1, -119.37) * mm});
            skLineSegment(sketch, "E20.27.0.13", {"start": v(-63.1, -119.38) * mm, "end": v(-57.32, -129.37) * mm});
            skLineSegment(sketch, "E20.30.0.13", {"start": v(-57.32, -129.38) * mm, "end": v(-63.1, -139.38) * mm});
            skLineSegment(sketch, "E20.33.0.13", {"start": v(-63.1, -139.38) * mm, "end": v(-74.64, -139.38) * mm});
            skLineSegment(sketch, "E20.0.0.14", {"start": v(-94.13, -153.12) * mm, "end": v(-82.58, -153.12) * mm});
            skLineSegment(sketch, "E20.3.0.14", {"start": v(-99.9, -163.13) * mm, "end": v(-94.13, -153.13) * mm});
            skLineSegment(sketch, "E20.6.0.14", {"start": v(-94.13, -173.13) * mm, "end": v(-99.9, -163.13) * mm});
            skLineSegment(sketch, "E20.9.0.14", {"start": v(-82.58, -173.12) * mm, "end": v(-94.13, -173.12) * mm});
            skLineSegment(sketch, "E20.12.0.14", {"start": v(-76.8, -163.13) * mm, "end": v(-82.58, -173.12) * mm});
            skLineSegment(sketch, "E20.15.0.14", {"start": v(-82.58, -153.12) * mm, "end": v(-76.8, -163.12) * mm});
            skLineSegment(sketch, "E20.18.0.14", {"start": v(-80.42, -151.88) * mm, "end": v(-74.64, -141.88) * mm});
            skLineSegment(sketch, "E20.21.0.14", {"start": v(-74.64, -161.87) * mm, "end": v(-80.42, -151.88) * mm});
            skLineSegment(sketch, "E20.24.0.14", {"start": v(-74.64, -141.88) * mm, "end": v(-63.1, -141.88) * mm});
            skLineSegment(sketch, "E20.27.0.14", {"start": v(-63.1, -141.88) * mm, "end": v(-57.32, -151.87) * mm});
            skLineSegment(sketch, "E20.30.0.14", {"start": v(-57.32, -151.88) * mm, "end": v(-63.1, -161.88) * mm});
            skLineSegment(sketch, "E20.33.0.14", {"start": v(-63.1, -161.88) * mm, "end": v(-74.64, -161.88) * mm});
            skLineSegment(sketch, "E20.0.1.2", {"start": v(-54.82, 116.87) * mm, "end": v(-43.28, 116.87) * mm});
            skLineSegment(sketch, "E20.3.1.2", {"start": v(-60.6, 106.87) * mm, "end": v(-54.82, 116.87) * mm});
            skLineSegment(sketch, "E20.6.1.2", {"start": v(-54.82, 96.87) * mm, "end": v(-60.6, 106.87) * mm});
            skLineSegment(sketch, "E20.9.1.2", {"start": v(-43.28, 96.87) * mm, "end": v(-54.82, 96.87) * mm});
            skLineSegment(sketch, "E20.12.1.2", {"start": v(-37.5, 106.87) * mm, "end": v(-43.28, 96.87) * mm});
            skLineSegment(sketch, "E20.15.1.2", {"start": v(-43.28, 116.87) * mm, "end": v(-37.5, 106.87) * mm});
            skLineSegment(sketch, "E20.18.1.2", {"start": v(-41.11, 118.12) * mm, "end": v(-35.34, 128.12) * mm});
            skLineSegment(sketch, "E20.21.1.2", {"start": v(-35.34, 108.12) * mm, "end": v(-41.11, 118.12) * mm});
            skLineSegment(sketch, "E20.24.1.2", {"start": v(-35.34, 128.12) * mm, "end": v(-23.79, 128.12) * mm});
            skLineSegment(sketch, "E20.27.1.2", {"start": v(-23.79, 128.12) * mm, "end": v(-18.02, 118.12) * mm});
            skLineSegment(sketch, "E20.30.1.2", {"start": v(-18.02, 118.12) * mm, "end": v(-23.79, 108.12) * mm});
            skLineSegment(sketch, "E20.33.1.2", {"start": v(-23.79, 108.12) * mm, "end": v(-35.34, 108.12) * mm});
            skLineSegment(sketch, "E20.0.1.3", {"start": v(-54.82, 94.37) * mm, "end": v(-43.28, 94.37) * mm});
            skLineSegment(sketch, "E20.3.1.3", {"start": v(-60.6, 84.37) * mm, "end": v(-54.82, 94.37) * mm});
            skLineSegment(sketch, "E20.6.1.3", {"start": v(-54.82, 74.37) * mm, "end": v(-60.6, 84.37) * mm});
            skLineSegment(sketch, "E20.9.1.3", {"start": v(-43.28, 74.37) * mm, "end": v(-54.82, 74.37) * mm});
            skLineSegment(sketch, "E20.12.1.3", {"start": v(-37.5, 84.37) * mm, "end": v(-43.28, 74.37) * mm});
            skLineSegment(sketch, "E20.15.1.3", {"start": v(-43.28, 94.37) * mm, "end": v(-37.5, 84.37) * mm});
            skLineSegment(sketch, "E20.18.1.3", {"start": v(-41.11, 95.62) * mm, "end": v(-35.34, 105.62) * mm});
            skLineSegment(sketch, "E20.21.1.3", {"start": v(-35.34, 85.62) * mm, "end": v(-41.11, 95.62) * mm});
            skLineSegment(sketch, "E20.24.1.3", {"start": v(-35.34, 105.62) * mm, "end": v(-23.79, 105.62) * mm});
            skLineSegment(sketch, "E20.27.1.3", {"start": v(-23.79, 105.62) * mm, "end": v(-18.02, 95.62) * mm});
            skLineSegment(sketch, "E20.30.1.3", {"start": v(-18.02, 95.62) * mm, "end": v(-23.79, 85.62) * mm});
            skLineSegment(sketch, "E20.33.1.3", {"start": v(-23.79, 85.62) * mm, "end": v(-35.34, 85.62) * mm});
            skLineSegment(sketch, "E20.0.1.4", {"start": v(-54.82, 71.87) * mm, "end": v(-43.28, 71.87) * mm});
            skLineSegment(sketch, "E20.3.1.4", {"start": v(-60.6, 61.87) * mm, "end": v(-54.82, 71.87) * mm});
            skLineSegment(sketch, "E20.6.1.4", {"start": v(-54.82, 51.87) * mm, "end": v(-60.6, 61.87) * mm});
            skLineSegment(sketch, "E20.9.1.4", {"start": v(-43.28, 51.87) * mm, "end": v(-54.82, 51.87) * mm});
            skLineSegment(sketch, "E20.12.1.4", {"start": v(-37.5, 61.87) * mm, "end": v(-43.28, 51.87) * mm});
            skLineSegment(sketch, "E20.15.1.4", {"start": v(-43.28, 71.87) * mm, "end": v(-37.5, 61.87) * mm});
            skLineSegment(sketch, "E20.18.1.4", {"start": v(-41.11, 73.12) * mm, "end": v(-35.34, 83.12) * mm});
            skLineSegment(sketch, "E20.21.1.4", {"start": v(-35.34, 63.12) * mm, "end": v(-41.11, 73.12) * mm});
            skLineSegment(sketch, "E20.24.1.4", {"start": v(-35.34, 83.12) * mm, "end": v(-23.79, 83.12) * mm});
            skLineSegment(sketch, "E20.27.1.4", {"start": v(-23.79, 83.12) * mm, "end": v(-18.02, 73.12) * mm});
            skLineSegment(sketch, "E20.30.1.4", {"start": v(-18.02, 73.12) * mm, "end": v(-23.79, 63.12) * mm});
            skLineSegment(sketch, "E20.33.1.4", {"start": v(-23.79, 63.12) * mm, "end": v(-35.34, 63.12) * mm});
            skLineSegment(sketch, "E20.0.1.5", {"start": v(-54.82, 49.37) * mm, "end": v(-43.28, 49.37) * mm});
            skLineSegment(sketch, "E20.3.1.5", {"start": v(-60.6, 39.37) * mm, "end": v(-54.82, 49.37) * mm});
            skLineSegment(sketch, "E20.6.1.5", {"start": v(-54.82, 29.37) * mm, "end": v(-60.6, 39.37) * mm});
            skLineSegment(sketch, "E20.9.1.5", {"start": v(-43.28, 29.37) * mm, "end": v(-54.82, 29.37) * mm});
            skLineSegment(sketch, "E20.12.1.5", {"start": v(-37.5, 39.37) * mm, "end": v(-43.28, 29.37) * mm});
            skLineSegment(sketch, "E20.15.1.5", {"start": v(-43.28, 49.37) * mm, "end": v(-37.5, 39.37) * mm});
            skLineSegment(sketch, "E20.18.1.5", {"start": v(-41.11, 50.62) * mm, "end": v(-35.34, 60.62) * mm});
            skLineSegment(sketch, "E20.21.1.5", {"start": v(-35.34, 40.62) * mm, "end": v(-41.11, 50.62) * mm});
            skLineSegment(sketch, "E20.24.1.5", {"start": v(-35.34, 60.62) * mm, "end": v(-23.79, 60.62) * mm});
            skLineSegment(sketch, "E20.27.1.5", {"start": v(-23.79, 60.62) * mm, "end": v(-18.02, 50.62) * mm});
            skLineSegment(sketch, "E20.30.1.5", {"start": v(-18.02, 50.62) * mm, "end": v(-23.79, 40.62) * mm});
            skLineSegment(sketch, "E20.33.1.5", {"start": v(-23.79, 40.62) * mm, "end": v(-35.34, 40.62) * mm});
            skLineSegment(sketch, "E20.0.1.6", {"start": v(-54.82, 26.87) * mm, "end": v(-43.28, 26.87) * mm});
            skLineSegment(sketch, "E20.3.1.6", {"start": v(-60.6, 16.87) * mm, "end": v(-54.82, 26.87) * mm});
            skLineSegment(sketch, "E20.6.1.6", {"start": v(-54.82, 6.87) * mm, "end": v(-60.6, 16.87) * mm});
            skLineSegment(sketch, "E20.9.1.6", {"start": v(-43.28, 6.87) * mm, "end": v(-54.82, 6.87) * mm});
            skLineSegment(sketch, "E20.12.1.6", {"start": v(-37.5, 16.87) * mm, "end": v(-43.28, 6.87) * mm});
            skLineSegment(sketch, "E20.15.1.6", {"start": v(-43.28, 26.87) * mm, "end": v(-37.5, 16.87) * mm});
            skLineSegment(sketch, "E20.18.1.6", {"start": v(-41.11, 28.12) * mm, "end": v(-35.34, 38.12) * mm});
            skLineSegment(sketch, "E20.21.1.6", {"start": v(-35.34, 18.12) * mm, "end": v(-41.11, 28.12) * mm});
            skLineSegment(sketch, "E20.24.1.6", {"start": v(-35.34, 38.12) * mm, "end": v(-23.79, 38.12) * mm});
            skLineSegment(sketch, "E20.27.1.6", {"start": v(-23.79, 38.12) * mm, "end": v(-18.02, 28.12) * mm});
            skLineSegment(sketch, "E20.30.1.6", {"start": v(-18.02, 28.12) * mm, "end": v(-23.79, 18.12) * mm});
            skLineSegment(sketch, "E20.33.1.6", {"start": v(-23.79, 18.12) * mm, "end": v(-35.34, 18.12) * mm});
            skLineSegment(sketch, "E20.0.1.7", {"start": v(-54.82, 4.37) * mm, "end": v(-43.28, 4.37) * mm});
            skLineSegment(sketch, "E20.3.1.7", {"start": v(-60.6, -5.63) * mm, "end": v(-54.82, 4.37) * mm});
            skLineSegment(sketch, "E20.6.1.7", {"start": v(-54.82, -15.63) * mm, "end": v(-60.6, -5.63) * mm});
            skLineSegment(sketch, "E20.9.1.7", {"start": v(-43.28, -15.63) * mm, "end": v(-54.82, -15.63) * mm});
            skLineSegment(sketch, "E20.12.1.7", {"start": v(-37.5, -5.63) * mm, "end": v(-43.28, -15.63) * mm});
            skLineSegment(sketch, "E20.15.1.7", {"start": v(-43.28, 4.37) * mm, "end": v(-37.5, -5.63) * mm});
            skLineSegment(sketch, "E20.18.1.7", {"start": v(-41.11, 5.62) * mm, "end": v(-35.34, 15.62) * mm});
            skLineSegment(sketch, "E20.21.1.7", {"start": v(-35.34, -4.38) * mm, "end": v(-41.11, 5.62) * mm});
            skLineSegment(sketch, "E20.24.1.7", {"start": v(-35.34, 15.62) * mm, "end": v(-23.79, 15.62) * mm});
            skLineSegment(sketch, "E20.27.1.7", {"start": v(-23.79, 15.62) * mm, "end": v(-18.02, 5.62) * mm});
            skLineSegment(sketch, "E20.30.1.7", {"start": v(-18.02, 5.62) * mm, "end": v(-23.79, -4.38) * mm});
            skLineSegment(sketch, "E20.33.1.7", {"start": v(-23.79, -4.38) * mm, "end": v(-35.34, -4.38) * mm});
            skLineSegment(sketch, "E20.0.1.8", {"start": v(-54.82, -18.13) * mm, "end": v(-43.28, -18.13) * mm});
            skLineSegment(sketch, "E20.3.1.8", {"start": v(-60.6, -28.13) * mm, "end": v(-54.82, -18.13) * mm});
            skLineSegment(sketch, "E20.6.1.8", {"start": v(-54.82, -38.13) * mm, "end": v(-60.6, -28.13) * mm});
            skLineSegment(sketch, "E20.9.1.8", {"start": v(-43.28, -38.13) * mm, "end": v(-54.82, -38.13) * mm});
            skLineSegment(sketch, "E20.12.1.8", {"start": v(-37.5, -28.13) * mm, "end": v(-43.28, -38.13) * mm});
            skLineSegment(sketch, "E20.15.1.8", {"start": v(-43.28, -18.13) * mm, "end": v(-37.5, -28.13) * mm});
            skLineSegment(sketch, "E20.18.1.8", {"start": v(-41.11, -16.88) * mm, "end": v(-35.34, -6.88) * mm});
            skLineSegment(sketch, "E20.21.1.8", {"start": v(-35.34, -26.88) * mm, "end": v(-41.11, -16.88) * mm});
            skLineSegment(sketch, "E20.24.1.8", {"start": v(-35.34, -6.88) * mm, "end": v(-23.79, -6.88) * mm});
            skLineSegment(sketch, "E20.27.1.8", {"start": v(-23.79, -6.88) * mm, "end": v(-18.02, -16.88) * mm});
            skLineSegment(sketch, "E20.30.1.8", {"start": v(-18.02, -16.88) * mm, "end": v(-23.79, -26.88) * mm});
            skLineSegment(sketch, "E20.33.1.8", {"start": v(-23.79, -26.88) * mm, "end": v(-35.34, -26.88) * mm});
            skLineSegment(sketch, "E20.0.1.9", {"start": v(-54.82, -40.63) * mm, "end": v(-43.28, -40.63) * mm});
            skLineSegment(sketch, "E20.3.1.9", {"start": v(-60.6, -50.63) * mm, "end": v(-54.82, -40.63) * mm});
            skLineSegment(sketch, "E20.6.1.9", {"start": v(-54.82, -60.63) * mm, "end": v(-60.6, -50.63) * mm});
            skLineSegment(sketch, "E20.9.1.9", {"start": v(-43.28, -60.63) * mm, "end": v(-54.82, -60.63) * mm});
            skLineSegment(sketch, "E20.12.1.9", {"start": v(-37.5, -50.63) * mm, "end": v(-43.28, -60.63) * mm});
            skLineSegment(sketch, "E20.15.1.9", {"start": v(-43.28, -40.63) * mm, "end": v(-37.5, -50.63) * mm});
            skLineSegment(sketch, "E20.18.1.9", {"start": v(-41.11, -39.38) * mm, "end": v(-35.34, -29.38) * mm});
            skLineSegment(sketch, "E20.21.1.9", {"start": v(-35.34, -49.38) * mm, "end": v(-41.11, -39.38) * mm});
            skLineSegment(sketch, "E20.24.1.9", {"start": v(-35.34, -29.38) * mm, "end": v(-23.79, -29.38) * mm});
            skLineSegment(sketch, "E20.27.1.9", {"start": v(-23.79, -29.38) * mm, "end": v(-18.02, -39.38) * mm});
            skLineSegment(sketch, "E20.30.1.9", {"start": v(-18.02, -39.38) * mm, "end": v(-23.79, -49.38) * mm});
            skLineSegment(sketch, "E20.33.1.9", {"start": v(-23.79, -49.38) * mm, "end": v(-35.34, -49.38) * mm});
            skLineSegment(sketch, "E20.0.1.10", {"start": v(-54.82, -63.13) * mm, "end": v(-43.28, -63.13) * mm});
            skLineSegment(sketch, "E20.3.1.10", {"start": v(-60.6, -73.13) * mm, "end": v(-54.82, -63.13) * mm});
            skLineSegment(sketch, "E20.6.1.10", {"start": v(-54.82, -83.13) * mm, "end": v(-60.6, -73.13) * mm});
            skLineSegment(sketch, "E20.9.1.10", {"start": v(-43.28, -83.13) * mm, "end": v(-54.82, -83.13) * mm});
            skLineSegment(sketch, "E20.12.1.10", {"start": v(-37.5, -73.13) * mm, "end": v(-43.28, -83.13) * mm});
            skLineSegment(sketch, "E20.15.1.10", {"start": v(-43.28, -63.13) * mm, "end": v(-37.5, -73.13) * mm});
            skLineSegment(sketch, "E20.18.1.10", {"start": v(-41.11, -61.88) * mm, "end": v(-35.34, -51.88) * mm});
            skLineSegment(sketch, "E20.21.1.10", {"start": v(-35.34, -71.88) * mm, "end": v(-41.11, -61.88) * mm});
            skLineSegment(sketch, "E20.24.1.10", {"start": v(-35.34, -51.88) * mm, "end": v(-23.79, -51.88) * mm});
            skLineSegment(sketch, "E20.27.1.10", {"start": v(-23.79, -51.88) * mm, "end": v(-18.02, -61.88) * mm});
            skLineSegment(sketch, "E20.30.1.10", {"start": v(-18.02, -61.88) * mm, "end": v(-23.79, -71.88) * mm});
            skLineSegment(sketch, "E20.33.1.10", {"start": v(-23.79, -71.88) * mm, "end": v(-35.34, -71.88) * mm});
            skLineSegment(sketch, "E20.0.1.11", {"start": v(-54.82, -85.63) * mm, "end": v(-43.28, -85.63) * mm});
            skLineSegment(sketch, "E20.3.1.11", {"start": v(-60.6, -95.63) * mm, "end": v(-54.82, -85.63) * mm});
            skLineSegment(sketch, "E20.6.1.11", {"start": v(-54.82, -105.63) * mm, "end": v(-60.6, -95.63) * mm});
            skLineSegment(sketch, "E20.9.1.11", {"start": v(-43.28, -105.63) * mm, "end": v(-54.82, -105.63) * mm});
            skLineSegment(sketch, "E20.12.1.11", {"start": v(-37.5, -95.63) * mm, "end": v(-43.28, -105.63) * mm});
            skLineSegment(sketch, "E20.15.1.11", {"start": v(-43.28, -85.62) * mm, "end": v(-37.5, -95.63) * mm});
            skLineSegment(sketch, "E20.18.1.11", {"start": v(-41.11, -84.38) * mm, "end": v(-35.34, -74.38) * mm});
            skLineSegment(sketch, "E20.21.1.11", {"start": v(-35.34, -94.38) * mm, "end": v(-41.11, -84.38) * mm});
            skLineSegment(sketch, "E20.24.1.11", {"start": v(-35.34, -74.38) * mm, "end": v(-23.79, -74.38) * mm});
            skLineSegment(sketch, "E20.27.1.11", {"start": v(-23.79, -74.38) * mm, "end": v(-18.02, -84.38) * mm});
            skLineSegment(sketch, "E20.30.1.11", {"start": v(-18.02, -84.38) * mm, "end": v(-23.79, -94.38) * mm});
            skLineSegment(sketch, "E20.33.1.11", {"start": v(-23.79, -94.38) * mm, "end": v(-35.34, -94.38) * mm});
            skLineSegment(sketch, "E20.0.1.12", {"start": v(-54.82, -108.13) * mm, "end": v(-43.28, -108.13) * mm});
            skLineSegment(sketch, "E20.3.1.12", {"start": v(-60.6, -118.13) * mm, "end": v(-54.82, -108.13) * mm});
            skLineSegment(sketch, "E20.6.1.12", {"start": v(-54.82, -128.13) * mm, "end": v(-60.6, -118.13) * mm});
            skLineSegment(sketch, "E20.9.1.12", {"start": v(-43.28, -128.13) * mm, "end": v(-54.82, -128.13) * mm});
            skLineSegment(sketch, "E20.12.1.12", {"start": v(-37.5, -118.13) * mm, "end": v(-43.28, -128.13) * mm});
            skLineSegment(sketch, "E20.15.1.12", {"start": v(-43.28, -108.12) * mm, "end": v(-37.5, -118.13) * mm});
            skLineSegment(sketch, "E20.18.1.12", {"start": v(-41.11, -106.88) * mm, "end": v(-35.34, -96.88) * mm});
            skLineSegment(sketch, "E20.21.1.12", {"start": v(-35.34, -116.87) * mm, "end": v(-41.11, -106.88) * mm});
            skLineSegment(sketch, "E20.24.1.12", {"start": v(-35.34, -96.88) * mm, "end": v(-23.79, -96.88) * mm});
            skLineSegment(sketch, "E20.27.1.12", {"start": v(-23.79, -96.88) * mm, "end": v(-18.02, -106.88) * mm});
            skLineSegment(sketch, "E20.30.1.12", {"start": v(-18.02, -106.88) * mm, "end": v(-23.79, -116.88) * mm});
            skLineSegment(sketch, "E20.33.1.12", {"start": v(-23.79, -116.88) * mm, "end": v(-35.34, -116.88) * mm});
            skLineSegment(sketch, "E20.0.1.13", {"start": v(-54.82, -130.62) * mm, "end": v(-43.28, -130.62) * mm});
            skLineSegment(sketch, "E20.3.1.13", {"start": v(-60.6, -140.63) * mm, "end": v(-54.82, -130.63) * mm});
            skLineSegment(sketch, "E20.6.1.13", {"start": v(-54.82, -150.63) * mm, "end": v(-60.6, -140.62) * mm});
            skLineSegment(sketch, "E20.9.1.13", {"start": v(-43.28, -150.62) * mm, "end": v(-54.82, -150.62) * mm});
            skLineSegment(sketch, "E20.12.1.13", {"start": v(-37.5, -140.62) * mm, "end": v(-43.28, -150.62) * mm});
            skLineSegment(sketch, "E20.15.1.13", {"start": v(-43.28, -130.62) * mm, "end": v(-37.5, -140.62) * mm});
            skLineSegment(sketch, "E20.18.1.13", {"start": v(-41.11, -129.38) * mm, "end": v(-35.34, -119.38) * mm});
            skLineSegment(sketch, "E20.21.1.13", {"start": v(-35.34, -139.37) * mm, "end": v(-41.11, -129.38) * mm});
            skLineSegment(sketch, "E20.24.1.13", {"start": v(-35.34, -119.37) * mm, "end": v(-23.79, -119.37) * mm});
            skLineSegment(sketch, "E20.27.1.13", {"start": v(-23.79, -119.38) * mm, "end": v(-18.02, -129.37) * mm});
            skLineSegment(sketch, "E20.30.1.13", {"start": v(-18.02, -129.38) * mm, "end": v(-23.79, -139.38) * mm});
            skLineSegment(sketch, "E20.33.1.13", {"start": v(-23.79, -139.38) * mm, "end": v(-35.34, -139.38) * mm});
            skLineSegment(sketch, "E20.0.1.14", {"start": v(-54.82, -153.12) * mm, "end": v(-43.28, -153.12) * mm});
            skLineSegment(sketch, "E20.3.1.14", {"start": v(-60.6, -163.13) * mm, "end": v(-54.82, -153.13) * mm});
            skLineSegment(sketch, "E20.6.1.14", {"start": v(-54.82, -173.13) * mm, "end": v(-60.6, -163.13) * mm});
            skLineSegment(sketch, "E20.9.1.14", {"start": v(-43.28, -173.12) * mm, "end": v(-54.82, -173.12) * mm});
            skLineSegment(sketch, "E20.12.1.14", {"start": v(-37.5, -163.13) * mm, "end": v(-43.28, -173.12) * mm});
            skLineSegment(sketch, "E20.15.1.14", {"start": v(-43.28, -153.12) * mm, "end": v(-37.5, -163.12) * mm});
            skLineSegment(sketch, "E20.18.1.14", {"start": v(-41.11, -151.88) * mm, "end": v(-35.34, -141.88) * mm});
            skLineSegment(sketch, "E20.21.1.14", {"start": v(-35.34, -161.87) * mm, "end": v(-41.11, -151.88) * mm});
            skLineSegment(sketch, "E20.24.1.14", {"start": v(-35.34, -141.88) * mm, "end": v(-23.79, -141.88) * mm});
            skLineSegment(sketch, "E20.27.1.14", {"start": v(-23.79, -141.88) * mm, "end": v(-18.02, -151.87) * mm});
            skLineSegment(sketch, "E20.30.1.14", {"start": v(-18.02, -151.88) * mm, "end": v(-23.79, -161.88) * mm});
            skLineSegment(sketch, "E20.33.1.14", {"start": v(-23.79, -161.88) * mm, "end": v(-35.34, -161.88) * mm});
            skLineSegment(sketch, "E20.0.2.2", {"start": v(-15.52, 116.87) * mm, "end": v(-3.97, 116.87) * mm});
            skLineSegment(sketch, "E20.3.2.2", {"start": v(-21.29, 106.87) * mm, "end": v(-15.52, 116.87) * mm});
            skLineSegment(sketch, "E20.6.2.2", {"start": v(-15.52, 96.87) * mm, "end": v(-21.29, 106.87) * mm});
            skLineSegment(sketch, "E20.9.2.2", {"start": v(-3.97, 96.87) * mm, "end": v(-15.52, 96.87) * mm});
            skLineSegment(sketch, "E20.12.2.2", {"start": v(1.8, 106.87) * mm, "end": v(-3.97, 96.87) * mm});
            skLineSegment(sketch, "E20.15.2.2", {"start": v(-3.97, 116.87) * mm, "end": v(1.8, 106.87) * mm});
            skLineSegment(sketch, "E20.18.2.2", {"start": v(-1.8, 118.12) * mm, "end": v(3.97, 128.12) * mm});
            skLineSegment(sketch, "E20.21.2.2", {"start": v(3.97, 108.12) * mm, "end": v(-1.8, 118.12) * mm});
            skLineSegment(sketch, "E20.24.2.2", {"start": v(3.97, 128.12) * mm, "end": v(15.52, 128.12) * mm});
            skLineSegment(sketch, "E20.27.2.2", {"start": v(15.52, 128.12) * mm, "end": v(21.29, 118.12) * mm});
            skLineSegment(sketch, "E20.30.2.2", {"start": v(21.29, 118.12) * mm, "end": v(15.52, 108.12) * mm});
            skLineSegment(sketch, "E20.33.2.2", {"start": v(15.52, 108.12) * mm, "end": v(3.97, 108.12) * mm});
            skLineSegment(sketch, "E20.0.2.3", {"start": v(-15.52, 94.37) * mm, "end": v(-3.97, 94.37) * mm});
            skLineSegment(sketch, "E20.3.2.3", {"start": v(-21.29, 84.37) * mm, "end": v(-15.52, 94.37) * mm});
            skLineSegment(sketch, "E20.6.2.3", {"start": v(-15.52, 74.37) * mm, "end": v(-21.29, 84.37) * mm});
            skLineSegment(sketch, "E20.9.2.3", {"start": v(-3.97, 74.37) * mm, "end": v(-15.52, 74.37) * mm});
            skLineSegment(sketch, "E20.12.2.3", {"start": v(1.8, 84.37) * mm, "end": v(-3.97, 74.37) * mm});
            skLineSegment(sketch, "E20.15.2.3", {"start": v(-3.97, 94.37) * mm, "end": v(1.8, 84.37) * mm});
            skLineSegment(sketch, "E20.18.2.3", {"start": v(-1.8, 95.62) * mm, "end": v(3.97, 105.62) * mm});
            skLineSegment(sketch, "E20.21.2.3", {"start": v(3.97, 85.62) * mm, "end": v(-1.8, 95.62) * mm});
            skLineSegment(sketch, "E20.24.2.3", {"start": v(3.97, 105.62) * mm, "end": v(15.52, 105.62) * mm});
            skLineSegment(sketch, "E20.27.2.3", {"start": v(15.52, 105.62) * mm, "end": v(21.29, 95.62) * mm});
            skLineSegment(sketch, "E20.30.2.3", {"start": v(21.29, 95.62) * mm, "end": v(15.52, 85.62) * mm});
            skLineSegment(sketch, "E20.33.2.3", {"start": v(15.52, 85.62) * mm, "end": v(3.97, 85.62) * mm});
            skLineSegment(sketch, "E20.0.2.4", {"start": v(-15.52, 71.87) * mm, "end": v(-3.97, 71.87) * mm});
            skLineSegment(sketch, "E20.3.2.4", {"start": v(-21.29, 61.87) * mm, "end": v(-15.52, 71.87) * mm});
            skLineSegment(sketch, "E20.6.2.4", {"start": v(-15.52, 51.87) * mm, "end": v(-21.29, 61.87) * mm});
            skLineSegment(sketch, "E20.9.2.4", {"start": v(-3.97, 51.87) * mm, "end": v(-15.52, 51.87) * mm});
            skLineSegment(sketch, "E20.12.2.4", {"start": v(1.8, 61.87) * mm, "end": v(-3.97, 51.87) * mm});
            skLineSegment(sketch, "E20.15.2.4", {"start": v(-3.97, 71.87) * mm, "end": v(1.8, 61.87) * mm});
            skLineSegment(sketch, "E20.18.2.4", {"start": v(-1.8, 73.12) * mm, "end": v(3.97, 83.12) * mm});
            skLineSegment(sketch, "E20.21.2.4", {"start": v(3.97, 63.12) * mm, "end": v(-1.8, 73.12) * mm});
            skLineSegment(sketch, "E20.24.2.4", {"start": v(3.97, 83.12) * mm, "end": v(15.52, 83.12) * mm});
            skLineSegment(sketch, "E20.27.2.4", {"start": v(15.52, 83.12) * mm, "end": v(21.29, 73.12) * mm});
            skLineSegment(sketch, "E20.30.2.4", {"start": v(21.29, 73.12) * mm, "end": v(15.52, 63.12) * mm});
            skLineSegment(sketch, "E20.33.2.4", {"start": v(15.52, 63.12) * mm, "end": v(3.97, 63.12) * mm});
            skLineSegment(sketch, "E20.0.2.5", {"start": v(-15.52, 49.37) * mm, "end": v(-3.97, 49.37) * mm});
            skLineSegment(sketch, "E20.3.2.5", {"start": v(-21.29, 39.37) * mm, "end": v(-15.52, 49.37) * mm});
            skLineSegment(sketch, "E20.6.2.5", {"start": v(-15.52, 29.37) * mm, "end": v(-21.29, 39.37) * mm});
            skLineSegment(sketch, "E20.9.2.5", {"start": v(-3.97, 29.37) * mm, "end": v(-15.52, 29.37) * mm});
            skLineSegment(sketch, "E20.12.2.5", {"start": v(1.8, 39.37) * mm, "end": v(-3.97, 29.37) * mm});
            skLineSegment(sketch, "E20.15.2.5", {"start": v(-3.97, 49.37) * mm, "end": v(1.8, 39.37) * mm});
            skLineSegment(sketch, "E20.18.2.5", {"start": v(-1.8, 50.62) * mm, "end": v(3.97, 60.62) * mm});
            skLineSegment(sketch, "E20.21.2.5", {"start": v(3.97, 40.62) * mm, "end": v(-1.8, 50.62) * mm});
            skLineSegment(sketch, "E20.24.2.5", {"start": v(3.97, 60.62) * mm, "end": v(15.52, 60.62) * mm});
            skLineSegment(sketch, "E20.27.2.5", {"start": v(15.52, 60.62) * mm, "end": v(21.29, 50.62) * mm});
            skLineSegment(sketch, "E20.30.2.5", {"start": v(21.29, 50.62) * mm, "end": v(15.52, 40.62) * mm});
            skLineSegment(sketch, "E20.33.2.5", {"start": v(15.52, 40.62) * mm, "end": v(3.97, 40.62) * mm});
            skLineSegment(sketch, "E20.0.2.6", {"start": v(-15.52, 26.87) * mm, "end": v(-3.97, 26.87) * mm});
            skLineSegment(sketch, "E20.3.2.6", {"start": v(-21.29, 16.87) * mm, "end": v(-15.52, 26.87) * mm});
            skLineSegment(sketch, "E20.6.2.6", {"start": v(-15.52, 6.87) * mm, "end": v(-21.29, 16.87) * mm});
            skLineSegment(sketch, "E20.9.2.6", {"start": v(-3.97, 6.87) * mm, "end": v(-15.52, 6.87) * mm});
            skLineSegment(sketch, "E20.12.2.6", {"start": v(1.8, 16.87) * mm, "end": v(-3.97, 6.87) * mm});
            skLineSegment(sketch, "E20.15.2.6", {"start": v(-3.97, 26.87) * mm, "end": v(1.8, 16.87) * mm});
            skLineSegment(sketch, "E20.18.2.6", {"start": v(-1.8, 28.12) * mm, "end": v(3.97, 38.12) * mm});
            skLineSegment(sketch, "E20.21.2.6", {"start": v(3.97, 18.12) * mm, "end": v(-1.8, 28.12) * mm});
            skLineSegment(sketch, "E20.24.2.6", {"start": v(3.97, 38.12) * mm, "end": v(15.52, 38.12) * mm});
            skLineSegment(sketch, "E20.27.2.6", {"start": v(15.52, 38.12) * mm, "end": v(21.29, 28.12) * mm});
            skLineSegment(sketch, "E20.30.2.6", {"start": v(21.29, 28.12) * mm, "end": v(15.52, 18.12) * mm});
            skLineSegment(sketch, "E20.33.2.6", {"start": v(15.52, 18.12) * mm, "end": v(3.97, 18.12) * mm});
            skLineSegment(sketch, "E20.0.2.7", {"start": v(-15.52, 4.37) * mm, "end": v(-3.97, 4.37) * mm});
            skLineSegment(sketch, "E20.3.2.7", {"start": v(-21.29, -5.63) * mm, "end": v(-15.52, 4.37) * mm});
            skLineSegment(sketch, "E20.6.2.7", {"start": v(-15.52, -15.63) * mm, "end": v(-21.29, -5.63) * mm});
            skLineSegment(sketch, "E20.9.2.7", {"start": v(-3.97, -15.63) * mm, "end": v(-15.52, -15.63) * mm});
            skLineSegment(sketch, "E20.12.2.7", {"start": v(1.8, -5.63) * mm, "end": v(-3.97, -15.63) * mm});
            skLineSegment(sketch, "E20.15.2.7", {"start": v(-3.97, 4.37) * mm, "end": v(1.8, -5.63) * mm});
            skLineSegment(sketch, "E20.18.2.7", {"start": v(-1.8, 5.62) * mm, "end": v(3.97, 15.62) * mm});
            skLineSegment(sketch, "E20.21.2.7", {"start": v(3.97, -4.38) * mm, "end": v(-1.8, 5.62) * mm});
            skLineSegment(sketch, "E20.24.2.7", {"start": v(3.97, 15.62) * mm, "end": v(15.52, 15.62) * mm});
            skLineSegment(sketch, "E20.27.2.7", {"start": v(15.52, 15.62) * mm, "end": v(21.29, 5.62) * mm});
            skLineSegment(sketch, "E20.30.2.7", {"start": v(21.29, 5.62) * mm, "end": v(15.52, -4.38) * mm});
            skLineSegment(sketch, "E20.33.2.7", {"start": v(15.52, -4.38) * mm, "end": v(3.97, -4.38) * mm});
            skLineSegment(sketch, "E20.0.2.8", {"start": v(-15.52, -18.13) * mm, "end": v(-3.97, -18.13) * mm});
            skLineSegment(sketch, "E20.3.2.8", {"start": v(-21.29, -28.13) * mm, "end": v(-15.52, -18.13) * mm});
            skLineSegment(sketch, "E20.6.2.8", {"start": v(-15.52, -38.13) * mm, "end": v(-21.29, -28.13) * mm});
            skLineSegment(sketch, "E20.9.2.8", {"start": v(-3.97, -38.13) * mm, "end": v(-15.52, -38.13) * mm});
            skLineSegment(sketch, "E20.12.2.8", {"start": v(1.8, -28.13) * mm, "end": v(-3.97, -38.13) * mm});
            skLineSegment(sketch, "E20.15.2.8", {"start": v(-3.97, -18.13) * mm, "end": v(1.8, -28.13) * mm});
            skLineSegment(sketch, "E20.18.2.8", {"start": v(-1.8, -16.88) * mm, "end": v(3.97, -6.88) * mm});
            skLineSegment(sketch, "E20.21.2.8", {"start": v(3.97, -26.88) * mm, "end": v(-1.8, -16.88) * mm});
            skLineSegment(sketch, "E20.24.2.8", {"start": v(3.97, -6.88) * mm, "end": v(15.52, -6.88) * mm});
            skLineSegment(sketch, "E20.27.2.8", {"start": v(15.52, -6.88) * mm, "end": v(21.29, -16.88) * mm});
            skLineSegment(sketch, "E20.30.2.8", {"start": v(21.29, -16.88) * mm, "end": v(15.52, -26.88) * mm});
            skLineSegment(sketch, "E20.33.2.8", {"start": v(15.52, -26.88) * mm, "end": v(3.97, -26.88) * mm});
            skLineSegment(sketch, "E20.0.2.9", {"start": v(-15.52, -40.63) * mm, "end": v(-3.97, -40.63) * mm});
            skLineSegment(sketch, "E20.3.2.9", {"start": v(-21.29, -50.63) * mm, "end": v(-15.52, -40.63) * mm});
            skLineSegment(sketch, "E20.6.2.9", {"start": v(-15.52, -60.63) * mm, "end": v(-21.29, -50.63) * mm});
            skLineSegment(sketch, "E20.9.2.9", {"start": v(-3.97, -60.63) * mm, "end": v(-15.52, -60.63) * mm});
            skLineSegment(sketch, "E20.12.2.9", {"start": v(1.8, -50.63) * mm, "end": v(-3.97, -60.63) * mm});
            skLineSegment(sketch, "E20.15.2.9", {"start": v(-3.97, -40.63) * mm, "end": v(1.8, -50.63) * mm});
            skLineSegment(sketch, "E20.18.2.9", {"start": v(-1.8, -39.38) * mm, "end": v(3.97, -29.38) * mm});
            skLineSegment(sketch, "E20.21.2.9", {"start": v(3.97, -49.38) * mm, "end": v(-1.8, -39.38) * mm});
            skLineSegment(sketch, "E20.24.2.9", {"start": v(3.97, -29.38) * mm, "end": v(15.52, -29.38) * mm});
            skLineSegment(sketch, "E20.27.2.9", {"start": v(15.52, -29.38) * mm, "end": v(21.29, -39.38) * mm});
            skLineSegment(sketch, "E20.30.2.9", {"start": v(21.29, -39.38) * mm, "end": v(15.52, -49.38) * mm});
            skLineSegment(sketch, "E20.33.2.9", {"start": v(15.52, -49.38) * mm, "end": v(3.97, -49.38) * mm});
            skLineSegment(sketch, "E20.0.2.10", {"start": v(-15.52, -63.13) * mm, "end": v(-3.97, -63.13) * mm});
            skLineSegment(sketch, "E20.3.2.10", {"start": v(-21.29, -73.13) * mm, "end": v(-15.52, -63.13) * mm});
            skLineSegment(sketch, "E20.6.2.10", {"start": v(-15.52, -83.13) * mm, "end": v(-21.29, -73.13) * mm});
            skLineSegment(sketch, "E20.9.2.10", {"start": v(-3.97, -83.13) * mm, "end": v(-15.52, -83.13) * mm});
            skLineSegment(sketch, "E20.12.2.10", {"start": v(1.8, -73.13) * mm, "end": v(-3.97, -83.13) * mm});
            skLineSegment(sketch, "E20.15.2.10", {"start": v(-3.97, -63.13) * mm, "end": v(1.8, -73.13) * mm});
            skLineSegment(sketch, "E20.18.2.10", {"start": v(-1.8, -61.88) * mm, "end": v(3.97, -51.88) * mm});
            skLineSegment(sketch, "E20.21.2.10", {"start": v(3.97, -71.88) * mm, "end": v(-1.8, -61.88) * mm});
            skLineSegment(sketch, "E20.24.2.10", {"start": v(3.97, -51.88) * mm, "end": v(15.52, -51.88) * mm});
            skLineSegment(sketch, "E20.27.2.10", {"start": v(15.52, -51.88) * mm, "end": v(21.29, -61.88) * mm});
            skLineSegment(sketch, "E20.30.2.10", {"start": v(21.29, -61.88) * mm, "end": v(15.52, -71.88) * mm});
            skLineSegment(sketch, "E20.33.2.10", {"start": v(15.52, -71.88) * mm, "end": v(3.97, -71.88) * mm});
            skLineSegment(sketch, "E20.0.2.11", {"start": v(-15.52, -85.63) * mm, "end": v(-3.97, -85.63) * mm});
            skLineSegment(sketch, "E20.3.2.11", {"start": v(-21.29, -95.63) * mm, "end": v(-15.52, -85.63) * mm});
            skLineSegment(sketch, "E20.6.2.11", {"start": v(-15.52, -105.63) * mm, "end": v(-21.29, -95.63) * mm});
            skLineSegment(sketch, "E20.9.2.11", {"start": v(-3.97, -105.63) * mm, "end": v(-15.52, -105.63) * mm});
            skLineSegment(sketch, "E20.12.2.11", {"start": v(1.8, -95.63) * mm, "end": v(-3.97, -105.63) * mm});
            skLineSegment(sketch, "E20.15.2.11", {"start": v(-3.97, -85.62) * mm, "end": v(1.8, -95.63) * mm});
            skLineSegment(sketch, "E20.18.2.11", {"start": v(-1.8, -84.38) * mm, "end": v(3.97, -74.38) * mm});
            skLineSegment(sketch, "E20.21.2.11", {"start": v(3.97, -94.38) * mm, "end": v(-1.8, -84.38) * mm});
            skLineSegment(sketch, "E20.24.2.11", {"start": v(3.97, -74.38) * mm, "end": v(15.52, -74.38) * mm});
            skLineSegment(sketch, "E20.27.2.11", {"start": v(15.52, -74.38) * mm, "end": v(21.29, -84.38) * mm});
            skLineSegment(sketch, "E20.30.2.11", {"start": v(21.29, -84.38) * mm, "end": v(15.52, -94.38) * mm});
            skLineSegment(sketch, "E20.33.2.11", {"start": v(15.52, -94.38) * mm, "end": v(3.97, -94.38) * mm});
            skLineSegment(sketch, "E20.0.2.12", {"start": v(-15.52, -108.13) * mm, "end": v(-3.97, -108.13) * mm});
            skLineSegment(sketch, "E20.3.2.12", {"start": v(-21.29, -118.13) * mm, "end": v(-15.52, -108.13) * mm});
            skLineSegment(sketch, "E20.6.2.12", {"start": v(-15.52, -128.13) * mm, "end": v(-21.29, -118.13) * mm});
            skLineSegment(sketch, "E20.9.2.12", {"start": v(-3.97, -128.13) * mm, "end": v(-15.52, -128.13) * mm});
            skLineSegment(sketch, "E20.12.2.12", {"start": v(1.8, -118.13) * mm, "end": v(-3.97, -128.13) * mm});
            skLineSegment(sketch, "E20.15.2.12", {"start": v(-3.97, -108.12) * mm, "end": v(1.8, -118.13) * mm});
            skLineSegment(sketch, "E20.18.2.12", {"start": v(-1.8, -106.88) * mm, "end": v(3.97, -96.88) * mm});
            skLineSegment(sketch, "E20.21.2.12", {"start": v(3.97, -116.87) * mm, "end": v(-1.8, -106.88) * mm});
            skLineSegment(sketch, "E20.24.2.12", {"start": v(3.97, -96.88) * mm, "end": v(15.52, -96.88) * mm});
            skLineSegment(sketch, "E20.27.2.12", {"start": v(15.52, -96.88) * mm, "end": v(21.29, -106.88) * mm});
            skLineSegment(sketch, "E20.30.2.12", {"start": v(21.29, -106.88) * mm, "end": v(15.52, -116.88) * mm});
            skLineSegment(sketch, "E20.33.2.12", {"start": v(15.52, -116.88) * mm, "end": v(3.97, -116.88) * mm});
            skLineSegment(sketch, "E20.0.2.13", {"start": v(-15.52, -130.62) * mm, "end": v(-3.97, -130.62) * mm});
            skLineSegment(sketch, "E20.3.2.13", {"start": v(-21.29, -140.63) * mm, "end": v(-15.52, -130.63) * mm});
            skLineSegment(sketch, "E20.6.2.13", {"start": v(-15.52, -150.63) * mm, "end": v(-21.29, -140.63) * mm});
            skLineSegment(sketch, "E20.9.2.13", {"start": v(-3.97, -150.62) * mm, "end": v(-15.52, -150.62) * mm});
            skLineSegment(sketch, "E20.12.2.13", {"start": v(1.8, -140.62) * mm, "end": v(-3.97, -150.62) * mm});
            skLineSegment(sketch, "E20.15.2.13", {"start": v(-3.97, -130.62) * mm, "end": v(1.8, -140.62) * mm});
            skLineSegment(sketch, "E20.18.2.13", {"start": v(-1.8, -129.38) * mm, "end": v(3.97, -119.38) * mm});
            skLineSegment(sketch, "E20.21.2.13", {"start": v(3.97, -139.37) * mm, "end": v(-1.8, -129.38) * mm});
            skLineSegment(sketch, "E20.24.2.13", {"start": v(3.97, -119.37) * mm, "end": v(15.52, -119.37) * mm});
            skLineSegment(sketch, "E20.27.2.13", {"start": v(15.52, -119.38) * mm, "end": v(21.29, -129.37) * mm});
            skLineSegment(sketch, "E20.30.2.13", {"start": v(21.29, -129.38) * mm, "end": v(15.52, -139.38) * mm});
            skLineSegment(sketch, "E20.33.2.13", {"start": v(15.52, -139.38) * mm, "end": v(3.97, -139.38) * mm});
            skLineSegment(sketch, "E20.0.2.14", {"start": v(-15.52, -153.12) * mm, "end": v(-3.97, -153.12) * mm});
            skLineSegment(sketch, "E20.3.2.14", {"start": v(-21.29, -163.13) * mm, "end": v(-15.52, -153.13) * mm});
            skLineSegment(sketch, "E20.6.2.14", {"start": v(-15.52, -173.13) * mm, "end": v(-21.29, -163.13) * mm});
            skLineSegment(sketch, "E20.9.2.14", {"start": v(-3.97, -173.12) * mm, "end": v(-15.52, -173.12) * mm});
            skLineSegment(sketch, "E20.12.2.14", {"start": v(1.8, -163.13) * mm, "end": v(-3.97, -173.12) * mm});
            skLineSegment(sketch, "E20.15.2.14", {"start": v(-3.97, -153.12) * mm, "end": v(1.8, -163.12) * mm});
            skLineSegment(sketch, "E20.18.2.14", {"start": v(-1.8, -151.88) * mm, "end": v(3.97, -141.88) * mm});
            skLineSegment(sketch, "E20.21.2.14", {"start": v(3.97, -161.87) * mm, "end": v(-1.8, -151.88) * mm});
            skLineSegment(sketch, "E20.24.2.14", {"start": v(3.97, -141.88) * mm, "end": v(15.52, -141.88) * mm});
            skLineSegment(sketch, "E20.27.2.14", {"start": v(15.52, -141.88) * mm, "end": v(21.29, -151.87) * mm});
            skLineSegment(sketch, "E20.30.2.14", {"start": v(21.29, -151.88) * mm, "end": v(15.52, -161.88) * mm});
            skLineSegment(sketch, "E20.33.2.14", {"start": v(15.52, -161.88) * mm, "end": v(3.97, -161.88) * mm});
            skLineSegment(sketch, "E20.0.3.2", {"start": v(23.79, 116.87) * mm, "end": v(35.34, 116.87) * mm});
            skLineSegment(sketch, "E20.3.3.2", {"start": v(18.02, 106.87) * mm, "end": v(23.79, 116.87) * mm});
            skLineSegment(sketch, "E20.6.3.2", {"start": v(23.79, 96.87) * mm, "end": v(18.02, 106.87) * mm});
            skLineSegment(sketch, "E20.9.3.2", {"start": v(35.34, 96.87) * mm, "end": v(23.79, 96.87) * mm});
            skLineSegment(sketch, "E20.12.3.2", {"start": v(41.11, 106.87) * mm, "end": v(35.34, 96.87) * mm});
            skLineSegment(sketch, "E20.15.3.2", {"start": v(35.34, 116.87) * mm, "end": v(41.11, 106.87) * mm});
            skLineSegment(sketch, "E20.18.3.2", {"start": v(37.5, 118.12) * mm, "end": v(43.28, 128.12) * mm});
            skLineSegment(sketch, "E20.21.3.2", {"start": v(43.28, 108.12) * mm, "end": v(37.5, 118.12) * mm});
            skLineSegment(sketch, "E20.24.3.2", {"start": v(43.28, 128.12) * mm, "end": v(54.82, 128.12) * mm});
            skLineSegment(sketch, "E20.27.3.2", {"start": v(54.82, 128.12) * mm, "end": v(60.6, 118.12) * mm});
            skLineSegment(sketch, "E20.30.3.2", {"start": v(60.6, 118.12) * mm, "end": v(54.82, 108.12) * mm});
            skLineSegment(sketch, "E20.33.3.2", {"start": v(54.82, 108.12) * mm, "end": v(43.28, 108.12) * mm});
            skLineSegment(sketch, "E20.0.3.3", {"start": v(23.79, 94.37) * mm, "end": v(35.34, 94.37) * mm});
            skLineSegment(sketch, "E20.3.3.3", {"start": v(18.02, 84.37) * mm, "end": v(23.79, 94.37) * mm});
            skLineSegment(sketch, "E20.6.3.3", {"start": v(23.79, 74.37) * mm, "end": v(18.02, 84.37) * mm});
            skLineSegment(sketch, "E20.9.3.3", {"start": v(35.34, 74.37) * mm, "end": v(23.79, 74.37) * mm});
            skLineSegment(sketch, "E20.12.3.3", {"start": v(41.11, 84.37) * mm, "end": v(35.34, 74.37) * mm});
            skLineSegment(sketch, "E20.15.3.3", {"start": v(35.34, 94.37) * mm, "end": v(41.11, 84.37) * mm});
            skLineSegment(sketch, "E20.18.3.3", {"start": v(37.5, 95.62) * mm, "end": v(43.28, 105.62) * mm});
            skLineSegment(sketch, "E20.21.3.3", {"start": v(43.28, 85.62) * mm, "end": v(37.5, 95.62) * mm});
            skLineSegment(sketch, "E20.24.3.3", {"start": v(43.28, 105.62) * mm, "end": v(54.82, 105.62) * mm});
            skLineSegment(sketch, "E20.27.3.3", {"start": v(54.82, 105.62) * mm, "end": v(60.6, 95.62) * mm});
            skLineSegment(sketch, "E20.30.3.3", {"start": v(60.6, 95.62) * mm, "end": v(54.82, 85.62) * mm});
            skLineSegment(sketch, "E20.33.3.3", {"start": v(54.82, 85.62) * mm, "end": v(43.28, 85.62) * mm});
            skLineSegment(sketch, "E20.0.3.4", {"start": v(23.79, 71.87) * mm, "end": v(35.34, 71.87) * mm});
            skLineSegment(sketch, "E20.3.3.4", {"start": v(18.02, 61.87) * mm, "end": v(23.79, 71.87) * mm});
            skLineSegment(sketch, "E20.6.3.4", {"start": v(23.79, 51.87) * mm, "end": v(18.02, 61.87) * mm});
            skLineSegment(sketch, "E20.9.3.4", {"start": v(35.34, 51.87) * mm, "end": v(23.79, 51.87) * mm});
            skLineSegment(sketch, "E20.12.3.4", {"start": v(41.11, 61.87) * mm, "end": v(35.34, 51.87) * mm});
            skLineSegment(sketch, "E20.15.3.4", {"start": v(35.34, 71.87) * mm, "end": v(41.11, 61.87) * mm});
            skLineSegment(sketch, "E20.18.3.4", {"start": v(37.5, 73.12) * mm, "end": v(43.28, 83.12) * mm});
            skLineSegment(sketch, "E20.21.3.4", {"start": v(43.28, 63.12) * mm, "end": v(37.5, 73.12) * mm});
            skLineSegment(sketch, "E20.24.3.4", {"start": v(43.28, 83.12) * mm, "end": v(54.82, 83.12) * mm});
            skLineSegment(sketch, "E20.27.3.4", {"start": v(54.82, 83.12) * mm, "end": v(60.6, 73.12) * mm});
            skLineSegment(sketch, "E20.30.3.4", {"start": v(60.6, 73.12) * mm, "end": v(54.82, 63.12) * mm});
            skLineSegment(sketch, "E20.33.3.4", {"start": v(54.82, 63.12) * mm, "end": v(43.28, 63.12) * mm});
            skLineSegment(sketch, "E20.0.3.5", {"start": v(23.79, 49.37) * mm, "end": v(35.34, 49.37) * mm});
            skLineSegment(sketch, "E20.3.3.5", {"start": v(18.02, 39.37) * mm, "end": v(23.79, 49.37) * mm});
            skLineSegment(sketch, "E20.6.3.5", {"start": v(23.79, 29.37) * mm, "end": v(18.02, 39.37) * mm});
            skLineSegment(sketch, "E20.9.3.5", {"start": v(35.34, 29.37) * mm, "end": v(23.79, 29.37) * mm});
            skLineSegment(sketch, "E20.12.3.5", {"start": v(41.11, 39.37) * mm, "end": v(35.34, 29.37) * mm});
            skLineSegment(sketch, "E20.15.3.5", {"start": v(35.34, 49.37) * mm, "end": v(41.11, 39.37) * mm});
            skLineSegment(sketch, "E20.18.3.5", {"start": v(37.5, 50.62) * mm, "end": v(43.28, 60.62) * mm});
            skLineSegment(sketch, "E20.21.3.5", {"start": v(43.28, 40.62) * mm, "end": v(37.5, 50.62) * mm});
            skLineSegment(sketch, "E20.24.3.5", {"start": v(43.28, 60.62) * mm, "end": v(54.82, 60.62) * mm});
            skLineSegment(sketch, "E20.27.3.5", {"start": v(54.82, 60.62) * mm, "end": v(60.6, 50.62) * mm});
            skLineSegment(sketch, "E20.30.3.5", {"start": v(60.6, 50.62) * mm, "end": v(54.82, 40.62) * mm});
            skLineSegment(sketch, "E20.33.3.5", {"start": v(54.82, 40.62) * mm, "end": v(43.28, 40.62) * mm});
            skLineSegment(sketch, "E20.0.3.6", {"start": v(23.79, 26.87) * mm, "end": v(35.34, 26.87) * mm});
            skLineSegment(sketch, "E20.3.3.6", {"start": v(18.02, 16.87) * mm, "end": v(23.79, 26.87) * mm});
            skLineSegment(sketch, "E20.6.3.6", {"start": v(23.79, 6.87) * mm, "end": v(18.02, 16.87) * mm});
            skLineSegment(sketch, "E20.9.3.6", {"start": v(35.34, 6.87) * mm, "end": v(23.79, 6.87) * mm});
            skLineSegment(sketch, "E20.12.3.6", {"start": v(41.11, 16.87) * mm, "end": v(35.34, 6.87) * mm});
            skLineSegment(sketch, "E20.15.3.6", {"start": v(35.34, 26.87) * mm, "end": v(41.11, 16.87) * mm});
            skLineSegment(sketch, "E20.18.3.6", {"start": v(37.5, 28.12) * mm, "end": v(43.28, 38.12) * mm});
            skLineSegment(sketch, "E20.21.3.6", {"start": v(43.28, 18.12) * mm, "end": v(37.5, 28.12) * mm});
            skLineSegment(sketch, "E20.24.3.6", {"start": v(43.28, 38.12) * mm, "end": v(54.82, 38.12) * mm});
            skLineSegment(sketch, "E20.27.3.6", {"start": v(54.82, 38.12) * mm, "end": v(60.6, 28.12) * mm});
            skLineSegment(sketch, "E20.30.3.6", {"start": v(60.6, 28.12) * mm, "end": v(54.82, 18.12) * mm});
            skLineSegment(sketch, "E20.33.3.6", {"start": v(54.82, 18.12) * mm, "end": v(43.28, 18.12) * mm});
            skLineSegment(sketch, "E20.0.3.7", {"start": v(23.79, 4.37) * mm, "end": v(35.34, 4.37) * mm});
            skLineSegment(sketch, "E20.3.3.7", {"start": v(18.02, -5.63) * mm, "end": v(23.79, 4.37) * mm});
            skLineSegment(sketch, "E20.6.3.7", {"start": v(23.79, -15.63) * mm, "end": v(18.02, -5.63) * mm});
            skLineSegment(sketch, "E20.9.3.7", {"start": v(35.34, -15.63) * mm, "end": v(23.79, -15.63) * mm});
            skLineSegment(sketch, "E20.12.3.7", {"start": v(41.11, -5.63) * mm, "end": v(35.34, -15.63) * mm});
            skLineSegment(sketch, "E20.15.3.7", {"start": v(35.34, 4.37) * mm, "end": v(41.11, -5.63) * mm});
            skLineSegment(sketch, "E20.18.3.7", {"start": v(37.5, 5.62) * mm, "end": v(43.28, 15.62) * mm});
            skLineSegment(sketch, "E20.21.3.7", {"start": v(43.28, -4.38) * mm, "end": v(37.5, 5.62) * mm});
            skLineSegment(sketch, "E20.24.3.7", {"start": v(43.28, 15.62) * mm, "end": v(54.82, 15.62) * mm});
            skLineSegment(sketch, "E20.27.3.7", {"start": v(54.82, 15.62) * mm, "end": v(60.6, 5.62) * mm});
            skLineSegment(sketch, "E20.30.3.7", {"start": v(60.6, 5.62) * mm, "end": v(54.82, -4.38) * mm});
            skLineSegment(sketch, "E20.33.3.7", {"start": v(54.82, -4.38) * mm, "end": v(43.28, -4.38) * mm});
            skLineSegment(sketch, "E20.0.3.8", {"start": v(23.79, -18.13) * mm, "end": v(35.34, -18.13) * mm});
            skLineSegment(sketch, "E20.3.3.8", {"start": v(18.02, -28.13) * mm, "end": v(23.79, -18.13) * mm});
            skLineSegment(sketch, "E20.6.3.8", {"start": v(23.79, -38.13) * mm, "end": v(18.02, -28.13) * mm});
            skLineSegment(sketch, "E20.9.3.8", {"start": v(35.34, -38.13) * mm, "end": v(23.79, -38.13) * mm});
            skLineSegment(sketch, "E20.12.3.8", {"start": v(41.11, -28.13) * mm, "end": v(35.34, -38.13) * mm});
            skLineSegment(sketch, "E20.15.3.8", {"start": v(35.34, -18.13) * mm, "end": v(41.11, -28.13) * mm});
            skLineSegment(sketch, "E20.18.3.8", {"start": v(37.5, -16.88) * mm, "end": v(43.28, -6.88) * mm});
            skLineSegment(sketch, "E20.21.3.8", {"start": v(43.28, -26.88) * mm, "end": v(37.5, -16.88) * mm});
            skLineSegment(sketch, "E20.24.3.8", {"start": v(43.28, -6.88) * mm, "end": v(54.82, -6.88) * mm});
            skLineSegment(sketch, "E20.27.3.8", {"start": v(54.82, -6.88) * mm, "end": v(60.6, -16.88) * mm});
            skLineSegment(sketch, "E20.30.3.8", {"start": v(60.6, -16.88) * mm, "end": v(54.82, -26.88) * mm});
            skLineSegment(sketch, "E20.33.3.8", {"start": v(54.82, -26.88) * mm, "end": v(43.28, -26.88) * mm});
            skLineSegment(sketch, "E20.0.3.9", {"start": v(23.79, -40.63) * mm, "end": v(35.34, -40.63) * mm});
            skLineSegment(sketch, "E20.3.3.9", {"start": v(18.02, -50.63) * mm, "end": v(23.79, -40.63) * mm});
            skLineSegment(sketch, "E20.6.3.9", {"start": v(23.79, -60.63) * mm, "end": v(18.02, -50.63) * mm});
            skLineSegment(sketch, "E20.9.3.9", {"start": v(35.34, -60.63) * mm, "end": v(23.79, -60.63) * mm});
            skLineSegment(sketch, "E20.12.3.9", {"start": v(41.11, -50.63) * mm, "end": v(35.34, -60.63) * mm});
            skLineSegment(sketch, "E20.15.3.9", {"start": v(35.34, -40.63) * mm, "end": v(41.11, -50.63) * mm});
            skLineSegment(sketch, "E20.18.3.9", {"start": v(37.5, -39.38) * mm, "end": v(43.28, -29.38) * mm});
            skLineSegment(sketch, "E20.21.3.9", {"start": v(43.28, -49.38) * mm, "end": v(37.5, -39.38) * mm});
            skLineSegment(sketch, "E20.24.3.9", {"start": v(43.28, -29.38) * mm, "end": v(54.82, -29.38) * mm});
            skLineSegment(sketch, "E20.27.3.9", {"start": v(54.82, -29.38) * mm, "end": v(60.6, -39.38) * mm});
            skLineSegment(sketch, "E20.30.3.9", {"start": v(60.6, -39.38) * mm, "end": v(54.82, -49.38) * mm});
            skLineSegment(sketch, "E20.33.3.9", {"start": v(54.82, -49.38) * mm, "end": v(43.28, -49.38) * mm});
            skLineSegment(sketch, "E20.0.3.10", {"start": v(23.79, -63.13) * mm, "end": v(35.34, -63.13) * mm});
            skLineSegment(sketch, "E20.3.3.10", {"start": v(18.02, -73.13) * mm, "end": v(23.79, -63.13) * mm});
            skLineSegment(sketch, "E20.6.3.10", {"start": v(23.79, -83.13) * mm, "end": v(18.02, -73.13) * mm});
            skLineSegment(sketch, "E20.9.3.10", {"start": v(35.34, -83.13) * mm, "end": v(23.79, -83.13) * mm});
            skLineSegment(sketch, "E20.12.3.10", {"start": v(41.11, -73.13) * mm, "end": v(35.34, -83.13) * mm});
            skLineSegment(sketch, "E20.15.3.10", {"start": v(35.34, -63.13) * mm, "end": v(41.11, -73.13) * mm});
            skLineSegment(sketch, "E20.18.3.10", {"start": v(37.5, -61.88) * mm, "end": v(43.28, -51.88) * mm});
            skLineSegment(sketch, "E20.21.3.10", {"start": v(43.28, -71.88) * mm, "end": v(37.5, -61.88) * mm});
            skLineSegment(sketch, "E20.24.3.10", {"start": v(43.28, -51.88) * mm, "end": v(54.82, -51.88) * mm});
            skLineSegment(sketch, "E20.27.3.10", {"start": v(54.82, -51.88) * mm, "end": v(60.6, -61.88) * mm});
            skLineSegment(sketch, "E20.30.3.10", {"start": v(60.6, -61.88) * mm, "end": v(54.82, -71.88) * mm});
            skLineSegment(sketch, "E20.33.3.10", {"start": v(54.82, -71.88) * mm, "end": v(43.28, -71.88) * mm});
            skLineSegment(sketch, "E20.0.3.11", {"start": v(23.79, -85.63) * mm, "end": v(35.34, -85.63) * mm});
            skLineSegment(sketch, "E20.3.3.11", {"start": v(18.02, -95.63) * mm, "end": v(23.79, -85.63) * mm});
            skLineSegment(sketch, "E20.6.3.11", {"start": v(23.79, -105.63) * mm, "end": v(18.02, -95.63) * mm});
            skLineSegment(sketch, "E20.9.3.11", {"start": v(35.34, -105.63) * mm, "end": v(23.79, -105.63) * mm});
            skLineSegment(sketch, "E20.12.3.11", {"start": v(41.11, -95.63) * mm, "end": v(35.34, -105.63) * mm});
            skLineSegment(sketch, "E20.15.3.11", {"start": v(35.34, -85.62) * mm, "end": v(41.11, -95.63) * mm});
            skLineSegment(sketch, "E20.18.3.11", {"start": v(37.5, -84.38) * mm, "end": v(43.28, -74.38) * mm});
            skLineSegment(sketch, "E20.21.3.11", {"start": v(43.28, -94.37) * mm, "end": v(37.5, -84.38) * mm});
            skLineSegment(sketch, "E20.24.3.11", {"start": v(43.28, -74.38) * mm, "end": v(54.82, -74.38) * mm});
            skLineSegment(sketch, "E20.27.3.11", {"start": v(54.82, -74.38) * mm, "end": v(60.6, -84.38) * mm});
            skLineSegment(sketch, "E20.30.3.11", {"start": v(60.6, -84.38) * mm, "end": v(54.82, -94.38) * mm});
            skLineSegment(sketch, "E20.33.3.11", {"start": v(54.82, -94.38) * mm, "end": v(43.28, -94.38) * mm});
            skLineSegment(sketch, "E20.0.3.12", {"start": v(23.79, -108.13) * mm, "end": v(35.34, -108.13) * mm});
            skLineSegment(sketch, "E20.3.3.12", {"start": v(18.02, -118.13) * mm, "end": v(23.79, -108.13) * mm});
            skLineSegment(sketch, "E20.6.3.12", {"start": v(23.79, -128.13) * mm, "end": v(18.02, -118.13) * mm});
            skLineSegment(sketch, "E20.9.3.12", {"start": v(35.34, -128.13) * mm, "end": v(23.79, -128.13) * mm});
            skLineSegment(sketch, "E20.12.3.12", {"start": v(41.11, -118.13) * mm, "end": v(35.34, -128.13) * mm});
            skLineSegment(sketch, "E20.15.3.12", {"start": v(35.34, -108.12) * mm, "end": v(41.11, -118.13) * mm});
            skLineSegment(sketch, "E20.18.3.12", {"start": v(37.5, -106.88) * mm, "end": v(43.28, -96.88) * mm});
            skLineSegment(sketch, "E20.21.3.12", {"start": v(43.28, -116.87) * mm, "end": v(37.5, -106.88) * mm});
            skLineSegment(sketch, "E20.24.3.12", {"start": v(43.28, -96.88) * mm, "end": v(54.82, -96.88) * mm});
            skLineSegment(sketch, "E20.27.3.12", {"start": v(54.82, -96.88) * mm, "end": v(60.6, -106.88) * mm});
            skLineSegment(sketch, "E20.30.3.12", {"start": v(60.6, -106.88) * mm, "end": v(54.82, -116.88) * mm});
            skLineSegment(sketch, "E20.33.3.12", {"start": v(54.82, -116.88) * mm, "end": v(43.28, -116.88) * mm});
            skLineSegment(sketch, "E20.0.3.13", {"start": v(23.79, -130.62) * mm, "end": v(35.34, -130.62) * mm});
            skLineSegment(sketch, "E20.3.3.13", {"start": v(18.02, -140.63) * mm, "end": v(23.79, -130.63) * mm});
            skLineSegment(sketch, "E20.6.3.13", {"start": v(23.79, -150.63) * mm, "end": v(18.02, -140.63) * mm});
            skLineSegment(sketch, "E20.9.3.13", {"start": v(35.34, -150.62) * mm, "end": v(23.79, -150.62) * mm});
            skLineSegment(sketch, "E20.12.3.13", {"start": v(41.11, -140.62) * mm, "end": v(35.34, -150.62) * mm});
            skLineSegment(sketch, "E20.15.3.13", {"start": v(35.34, -130.62) * mm, "end": v(41.11, -140.62) * mm});
            skLineSegment(sketch, "E20.18.3.13", {"start": v(37.5, -129.38) * mm, "end": v(43.28, -119.38) * mm});
            skLineSegment(sketch, "E20.21.3.13", {"start": v(43.28, -139.37) * mm, "end": v(37.5, -129.38) * mm});
            skLineSegment(sketch, "E20.24.3.13", {"start": v(43.28, -119.37) * mm, "end": v(54.82, -119.37) * mm});
            skLineSegment(sketch, "E20.27.3.13", {"start": v(54.82, -119.37) * mm, "end": v(60.6, -129.37) * mm});
            skLineSegment(sketch, "E20.30.3.13", {"start": v(60.6, -129.38) * mm, "end": v(54.82, -139.38) * mm});
            skLineSegment(sketch, "E20.33.3.13", {"start": v(54.82, -139.38) * mm, "end": v(43.28, -139.38) * mm});
            skLineSegment(sketch, "E20.0.3.14", {"start": v(23.79, -153.12) * mm, "end": v(35.34, -153.12) * mm});
            skLineSegment(sketch, "E20.3.3.14", {"start": v(18.02, -163.13) * mm, "end": v(23.79, -153.13) * mm});
            skLineSegment(sketch, "E20.6.3.14", {"start": v(23.79, -173.13) * mm, "end": v(18.02, -163.13) * mm});
            skLineSegment(sketch, "E20.9.3.14", {"start": v(35.34, -173.12) * mm, "end": v(23.79, -173.12) * mm});
            skLineSegment(sketch, "E20.12.3.14", {"start": v(41.11, -163.13) * mm, "end": v(35.34, -173.13) * mm});
            skLineSegment(sketch, "E20.15.3.14", {"start": v(35.34, -153.12) * mm, "end": v(41.11, -163.12) * mm});
            skLineSegment(sketch, "E20.18.3.14", {"start": v(37.5, -151.88) * mm, "end": v(43.28, -141.88) * mm});
            skLineSegment(sketch, "E20.21.3.14", {"start": v(43.28, -161.87) * mm, "end": v(37.5, -151.88) * mm});
            skLineSegment(sketch, "E20.24.3.14", {"start": v(43.28, -141.88) * mm, "end": v(54.82, -141.88) * mm});
            skLineSegment(sketch, "E20.27.3.14", {"start": v(54.82, -141.88) * mm, "end": v(60.6, -151.87) * mm});
            skLineSegment(sketch, "E20.30.3.14", {"start": v(60.6, -151.88) * mm, "end": v(54.82, -161.88) * mm});
            skLineSegment(sketch, "E20.33.3.14", {"start": v(54.82, -161.88) * mm, "end": v(43.28, -161.88) * mm});
            skLineSegment(sketch, "E20.0.4.2", {"start": v(63.1, 116.87) * mm, "end": v(74.64, 116.87) * mm});
            skLineSegment(sketch, "E20.3.4.2", {"start": v(57.32, 106.87) * mm, "end": v(63.1, 116.87) * mm});
            skLineSegment(sketch, "E20.6.4.2", {"start": v(63.1, 96.87) * mm, "end": v(57.32, 106.87) * mm});
            skLineSegment(sketch, "E20.9.4.2", {"start": v(74.64, 96.87) * mm, "end": v(63.1, 96.87) * mm});
            skLineSegment(sketch, "E20.12.4.2", {"start": v(80.42, 106.87) * mm, "end": v(74.64, 96.87) * mm});
            skLineSegment(sketch, "E20.15.4.2", {"start": v(74.64, 116.87) * mm, "end": v(80.42, 106.87) * mm});
            skLineSegment(sketch, "E20.18.4.2", {"start": v(76.8, 118.12) * mm, "end": v(82.58, 128.12) * mm});
            skLineSegment(sketch, "E20.21.4.2", {"start": v(82.58, 108.12) * mm, "end": v(76.8, 118.12) * mm});
            skLineSegment(sketch, "E20.24.4.2", {"start": v(82.58, 128.12) * mm, "end": v(94.13, 128.12) * mm});
            skLineSegment(sketch, "E20.27.4.2", {"start": v(94.13, 128.12) * mm, "end": v(99.9, 118.12) * mm});
            skLineSegment(sketch, "E20.30.4.2", {"start": v(99.9, 118.12) * mm, "end": v(94.13, 108.12) * mm});
            skLineSegment(sketch, "E20.33.4.2", {"start": v(94.13, 108.12) * mm, "end": v(82.58, 108.12) * mm});
            skLineSegment(sketch, "E20.0.4.3", {"start": v(63.1, 94.37) * mm, "end": v(74.64, 94.37) * mm});
            skLineSegment(sketch, "E20.3.4.3", {"start": v(57.32, 84.37) * mm, "end": v(63.1, 94.37) * mm});
            skLineSegment(sketch, "E20.6.4.3", {"start": v(63.1, 74.37) * mm, "end": v(57.32, 84.37) * mm});
            skLineSegment(sketch, "E20.9.4.3", {"start": v(74.64, 74.37) * mm, "end": v(63.1, 74.37) * mm});
            skLineSegment(sketch, "E20.12.4.3", {"start": v(80.42, 84.37) * mm, "end": v(74.64, 74.37) * mm});
            skLineSegment(sketch, "E20.15.4.3", {"start": v(74.64, 94.37) * mm, "end": v(80.42, 84.37) * mm});
            skLineSegment(sketch, "E20.18.4.3", {"start": v(76.8, 95.62) * mm, "end": v(82.58, 105.62) * mm});
            skLineSegment(sketch, "E20.21.4.3", {"start": v(82.58, 85.62) * mm, "end": v(76.8, 95.62) * mm});
            skLineSegment(sketch, "E20.24.4.3", {"start": v(82.58, 105.62) * mm, "end": v(94.13, 105.62) * mm});
            skLineSegment(sketch, "E20.27.4.3", {"start": v(94.13, 105.62) * mm, "end": v(99.9, 95.62) * mm});
            skLineSegment(sketch, "E20.30.4.3", {"start": v(99.9, 95.62) * mm, "end": v(94.13, 85.62) * mm});
            skLineSegment(sketch, "E20.33.4.3", {"start": v(94.13, 85.62) * mm, "end": v(82.58, 85.62) * mm});
            skLineSegment(sketch, "E20.0.4.4", {"start": v(63.1, 71.87) * mm, "end": v(74.64, 71.87) * mm});
            skLineSegment(sketch, "E20.3.4.4", {"start": v(57.32, 61.87) * mm, "end": v(63.1, 71.87) * mm});
            skLineSegment(sketch, "E20.6.4.4", {"start": v(63.1, 51.87) * mm, "end": v(57.32, 61.87) * mm});
            skLineSegment(sketch, "E20.9.4.4", {"start": v(74.64, 51.87) * mm, "end": v(63.1, 51.87) * mm});
            skLineSegment(sketch, "E20.12.4.4", {"start": v(80.42, 61.87) * mm, "end": v(74.64, 51.87) * mm});
            skLineSegment(sketch, "E20.15.4.4", {"start": v(74.64, 71.87) * mm, "end": v(80.42, 61.87) * mm});
            skLineSegment(sketch, "E20.18.4.4", {"start": v(76.8, 73.12) * mm, "end": v(82.58, 83.12) * mm});
            skLineSegment(sketch, "E20.21.4.4", {"start": v(82.58, 63.12) * mm, "end": v(76.8, 73.12) * mm});
            skLineSegment(sketch, "E20.24.4.4", {"start": v(82.58, 83.12) * mm, "end": v(94.13, 83.12) * mm});
            skLineSegment(sketch, "E20.27.4.4", {"start": v(94.13, 83.12) * mm, "end": v(99.9, 73.12) * mm});
            skLineSegment(sketch, "E20.30.4.4", {"start": v(99.9, 73.12) * mm, "end": v(94.13, 63.12) * mm});
            skLineSegment(sketch, "E20.33.4.4", {"start": v(94.13, 63.12) * mm, "end": v(82.58, 63.12) * mm});
            skLineSegment(sketch, "E20.0.4.5", {"start": v(63.1, 49.37) * mm, "end": v(74.64, 49.37) * mm});
            skLineSegment(sketch, "E20.3.4.5", {"start": v(57.32, 39.37) * mm, "end": v(63.1, 49.37) * mm});
            skLineSegment(sketch, "E20.6.4.5", {"start": v(63.1, 29.37) * mm, "end": v(57.32, 39.37) * mm});
            skLineSegment(sketch, "E20.9.4.5", {"start": v(74.64, 29.37) * mm, "end": v(63.1, 29.37) * mm});
            skLineSegment(sketch, "E20.12.4.5", {"start": v(80.42, 39.37) * mm, "end": v(74.64, 29.37) * mm});
            skLineSegment(sketch, "E20.15.4.5", {"start": v(74.64, 49.37) * mm, "end": v(80.42, 39.37) * mm});
            skLineSegment(sketch, "E20.18.4.5", {"start": v(76.8, 50.62) * mm, "end": v(82.58, 60.62) * mm});
            skLineSegment(sketch, "E20.21.4.5", {"start": v(82.58, 40.62) * mm, "end": v(76.8, 50.62) * mm});
            skLineSegment(sketch, "E20.24.4.5", {"start": v(82.58, 60.62) * mm, "end": v(94.13, 60.62) * mm});
            skLineSegment(sketch, "E20.27.4.5", {"start": v(94.13, 60.62) * mm, "end": v(99.9, 50.62) * mm});
            skLineSegment(sketch, "E20.30.4.5", {"start": v(99.9, 50.62) * mm, "end": v(94.13, 40.62) * mm});
            skLineSegment(sketch, "E20.33.4.5", {"start": v(94.13, 40.62) * mm, "end": v(82.58, 40.62) * mm});
            skLineSegment(sketch, "E20.0.4.6", {"start": v(63.1, 26.87) * mm, "end": v(74.64, 26.87) * mm});
            skLineSegment(sketch, "E20.3.4.6", {"start": v(57.32, 16.87) * mm, "end": v(63.1, 26.87) * mm});
            skLineSegment(sketch, "E20.6.4.6", {"start": v(63.1, 6.87) * mm, "end": v(57.32, 16.87) * mm});
            skLineSegment(sketch, "E20.9.4.6", {"start": v(74.64, 6.87) * mm, "end": v(63.1, 6.87) * mm});
            skLineSegment(sketch, "E20.12.4.6", {"start": v(80.42, 16.87) * mm, "end": v(74.64, 6.87) * mm});
            skLineSegment(sketch, "E20.15.4.6", {"start": v(74.64, 26.87) * mm, "end": v(80.42, 16.87) * mm});
            skLineSegment(sketch, "E20.18.4.6", {"start": v(76.8, 28.12) * mm, "end": v(82.58, 38.12) * mm});
            skLineSegment(sketch, "E20.21.4.6", {"start": v(82.58, 18.12) * mm, "end": v(76.8, 28.12) * mm});
            skLineSegment(sketch, "E20.24.4.6", {"start": v(82.58, 38.12) * mm, "end": v(94.13, 38.12) * mm});
            skLineSegment(sketch, "E20.27.4.6", {"start": v(94.13, 38.12) * mm, "end": v(99.9, 28.12) * mm});
            skLineSegment(sketch, "E20.30.4.6", {"start": v(99.9, 28.12) * mm, "end": v(94.13, 18.12) * mm});
            skLineSegment(sketch, "E20.33.4.6", {"start": v(94.13, 18.12) * mm, "end": v(82.58, 18.12) * mm});
            skLineSegment(sketch, "E20.0.4.7", {"start": v(63.1, 4.37) * mm, "end": v(74.64, 4.37) * mm});
            skLineSegment(sketch, "E20.3.4.7", {"start": v(57.32, -5.63) * mm, "end": v(63.1, 4.37) * mm});
            skLineSegment(sketch, "E20.6.4.7", {"start": v(63.1, -15.63) * mm, "end": v(57.32, -5.63) * mm});
            skLineSegment(sketch, "E20.9.4.7", {"start": v(74.64, -15.63) * mm, "end": v(63.1, -15.63) * mm});
            skLineSegment(sketch, "E20.12.4.7", {"start": v(80.42, -5.63) * mm, "end": v(74.64, -15.63) * mm});
            skLineSegment(sketch, "E20.15.4.7", {"start": v(74.64, 4.37) * mm, "end": v(80.42, -5.63) * mm});
            skLineSegment(sketch, "E20.18.4.7", {"start": v(76.8, 5.62) * mm, "end": v(82.58, 15.62) * mm});
            skLineSegment(sketch, "E20.21.4.7", {"start": v(82.58, -4.38) * mm, "end": v(76.8, 5.62) * mm});
            skLineSegment(sketch, "E20.24.4.7", {"start": v(82.58, 15.62) * mm, "end": v(94.13, 15.62) * mm});
            skLineSegment(sketch, "E20.27.4.7", {"start": v(94.13, 15.62) * mm, "end": v(99.9, 5.62) * mm});
            skLineSegment(sketch, "E20.30.4.7", {"start": v(99.9, 5.62) * mm, "end": v(94.13, -4.38) * mm});
            skLineSegment(sketch, "E20.33.4.7", {"start": v(94.13, -4.38) * mm, "end": v(82.58, -4.38) * mm});
            skLineSegment(sketch, "E20.0.4.8", {"start": v(63.1, -18.13) * mm, "end": v(74.64, -18.13) * mm});
            skLineSegment(sketch, "E20.3.4.8", {"start": v(57.32, -28.13) * mm, "end": v(63.1, -18.13) * mm});
            skLineSegment(sketch, "E20.6.4.8", {"start": v(63.1, -38.13) * mm, "end": v(57.32, -28.13) * mm});
            skLineSegment(sketch, "E20.9.4.8", {"start": v(74.64, -38.13) * mm, "end": v(63.1, -38.13) * mm});
            skLineSegment(sketch, "E20.12.4.8", {"start": v(80.42, -28.13) * mm, "end": v(74.64, -38.13) * mm});
            skLineSegment(sketch, "E20.15.4.8", {"start": v(74.64, -18.13) * mm, "end": v(80.42, -28.13) * mm});
            skLineSegment(sketch, "E20.18.4.8", {"start": v(76.8, -16.88) * mm, "end": v(82.58, -6.88) * mm});
            skLineSegment(sketch, "E20.21.4.8", {"start": v(82.58, -26.88) * mm, "end": v(76.8, -16.88) * mm});
            skLineSegment(sketch, "E20.24.4.8", {"start": v(82.58, -6.88) * mm, "end": v(94.13, -6.88) * mm});
            skLineSegment(sketch, "E20.27.4.8", {"start": v(94.13, -6.88) * mm, "end": v(99.9, -16.88) * mm});
            skLineSegment(sketch, "E20.30.4.8", {"start": v(99.9, -16.88) * mm, "end": v(94.13, -26.88) * mm});
            skLineSegment(sketch, "E20.33.4.8", {"start": v(94.13, -26.88) * mm, "end": v(82.58, -26.88) * mm});
            skLineSegment(sketch, "E20.0.4.9", {"start": v(63.1, -40.63) * mm, "end": v(74.64, -40.63) * mm});
            skLineSegment(sketch, "E20.3.4.9", {"start": v(57.32, -50.63) * mm, "end": v(63.1, -40.63) * mm});
            skLineSegment(sketch, "E20.6.4.9", {"start": v(63.1, -60.63) * mm, "end": v(57.32, -50.63) * mm});
            skLineSegment(sketch, "E20.9.4.9", {"start": v(74.64, -60.63) * mm, "end": v(63.1, -60.63) * mm});
            skLineSegment(sketch, "E20.12.4.9", {"start": v(80.42, -50.63) * mm, "end": v(74.64, -60.63) * mm});
            skLineSegment(sketch, "E20.15.4.9", {"start": v(74.64, -40.63) * mm, "end": v(80.42, -50.63) * mm});
            skLineSegment(sketch, "E20.18.4.9", {"start": v(76.8, -39.38) * mm, "end": v(82.58, -29.38) * mm});
            skLineSegment(sketch, "E20.21.4.9", {"start": v(82.58, -49.38) * mm, "end": v(76.8, -39.38) * mm});
            skLineSegment(sketch, "E20.24.4.9", {"start": v(82.58, -29.38) * mm, "end": v(94.13, -29.38) * mm});
            skLineSegment(sketch, "E20.27.4.9", {"start": v(94.13, -29.38) * mm, "end": v(99.9, -39.38) * mm});
            skLineSegment(sketch, "E20.30.4.9", {"start": v(99.9, -39.38) * mm, "end": v(94.13, -49.38) * mm});
            skLineSegment(sketch, "E20.33.4.9", {"start": v(94.13, -49.38) * mm, "end": v(82.58, -49.38) * mm});
            skLineSegment(sketch, "E20.0.4.10", {"start": v(63.1, -63.13) * mm, "end": v(74.64, -63.13) * mm});
            skLineSegment(sketch, "E20.3.4.10", {"start": v(57.32, -73.13) * mm, "end": v(63.1, -63.13) * mm});
            skLineSegment(sketch, "E20.6.4.10", {"start": v(63.1, -83.13) * mm, "end": v(57.32, -73.13) * mm});
            skLineSegment(sketch, "E20.9.4.10", {"start": v(74.64, -83.13) * mm, "end": v(63.1, -83.13) * mm});
            skLineSegment(sketch, "E20.12.4.10", {"start": v(80.42, -73.13) * mm, "end": v(74.64, -83.13) * mm});
            skLineSegment(sketch, "E20.15.4.10", {"start": v(74.64, -63.13) * mm, "end": v(80.42, -73.13) * mm});
            skLineSegment(sketch, "E20.18.4.10", {"start": v(76.8, -61.88) * mm, "end": v(82.58, -51.88) * mm});
            skLineSegment(sketch, "E20.21.4.10", {"start": v(82.58, -71.88) * mm, "end": v(76.8, -61.88) * mm});
            skLineSegment(sketch, "E20.24.4.10", {"start": v(82.58, -51.88) * mm, "end": v(94.13, -51.88) * mm});
            skLineSegment(sketch, "E20.27.4.10", {"start": v(94.13, -51.88) * mm, "end": v(99.9, -61.88) * mm});
            skLineSegment(sketch, "E20.30.4.10", {"start": v(99.9, -61.88) * mm, "end": v(94.13, -71.88) * mm});
            skLineSegment(sketch, "E20.33.4.10", {"start": v(94.13, -71.88) * mm, "end": v(82.58, -71.88) * mm});
            skLineSegment(sketch, "E20.0.4.11", {"start": v(63.1, -85.63) * mm, "end": v(74.64, -85.63) * mm});
            skLineSegment(sketch, "E20.3.4.11", {"start": v(57.32, -95.63) * mm, "end": v(63.1, -85.63) * mm});
            skLineSegment(sketch, "E20.6.4.11", {"start": v(63.1, -105.63) * mm, "end": v(57.32, -95.63) * mm});
            skLineSegment(sketch, "E20.9.4.11", {"start": v(74.64, -105.63) * mm, "end": v(63.1, -105.63) * mm});
            skLineSegment(sketch, "E20.12.4.11", {"start": v(80.42, -95.63) * mm, "end": v(74.64, -105.63) * mm});
            skLineSegment(sketch, "E20.15.4.11", {"start": v(74.64, -85.62) * mm, "end": v(80.42, -95.63) * mm});
            skLineSegment(sketch, "E20.18.4.11", {"start": v(76.8, -84.38) * mm, "end": v(82.58, -74.38) * mm});
            skLineSegment(sketch, "E20.21.4.11", {"start": v(82.58, -94.37) * mm, "end": v(76.8, -84.38) * mm});
            skLineSegment(sketch, "E20.24.4.11", {"start": v(82.58, -74.38) * mm, "end": v(94.13, -74.38) * mm});
            skLineSegment(sketch, "E20.27.4.11", {"start": v(94.13, -74.38) * mm, "end": v(99.9, -84.38) * mm});
            skLineSegment(sketch, "E20.30.4.11", {"start": v(99.9, -84.38) * mm, "end": v(94.13, -94.38) * mm});
            skLineSegment(sketch, "E20.33.4.11", {"start": v(94.13, -94.38) * mm, "end": v(82.58, -94.38) * mm});
            skLineSegment(sketch, "E20.0.4.12", {"start": v(63.1, -108.13) * mm, "end": v(74.64, -108.13) * mm});
            skLineSegment(sketch, "E20.3.4.12", {"start": v(57.32, -118.13) * mm, "end": v(63.1, -108.13) * mm});
            skLineSegment(sketch, "E20.6.4.12", {"start": v(63.1, -128.13) * mm, "end": v(57.32, -118.13) * mm});
            skLineSegment(sketch, "E20.9.4.12", {"start": v(74.64, -128.13) * mm, "end": v(63.1, -128.13) * mm});
            skLineSegment(sketch, "E20.12.4.12", {"start": v(80.42, -118.13) * mm, "end": v(74.64, -128.13) * mm});
            skLineSegment(sketch, "E20.15.4.12", {"start": v(74.64, -108.12) * mm, "end": v(80.42, -118.13) * mm});
            skLineSegment(sketch, "E20.18.4.12", {"start": v(76.8, -106.88) * mm, "end": v(82.58, -96.88) * mm});
            skLineSegment(sketch, "E20.21.4.12", {"start": v(82.58, -116.87) * mm, "end": v(76.8, -106.88) * mm});
            skLineSegment(sketch, "E20.24.4.12", {"start": v(82.58, -96.88) * mm, "end": v(94.13, -96.88) * mm});
            skLineSegment(sketch, "E20.27.4.12", {"start": v(94.13, -96.88) * mm, "end": v(99.9, -106.88) * mm});
            skLineSegment(sketch, "E20.30.4.12", {"start": v(99.9, -106.88) * mm, "end": v(94.13, -116.88) * mm});
            skLineSegment(sketch, "E20.33.4.12", {"start": v(94.13, -116.88) * mm, "end": v(82.58, -116.88) * mm});
            skLineSegment(sketch, "E20.0.4.13", {"start": v(63.1, -130.62) * mm, "end": v(74.64, -130.62) * mm});
            skLineSegment(sketch, "E20.3.4.13", {"start": v(57.32, -140.63) * mm, "end": v(63.1, -130.63) * mm});
            skLineSegment(sketch, "E20.6.4.13", {"start": v(63.1, -150.63) * mm, "end": v(57.32, -140.63) * mm});
            skLineSegment(sketch, "E20.9.4.13", {"start": v(74.64, -150.62) * mm, "end": v(63.1, -150.62) * mm});
            skLineSegment(sketch, "E20.12.4.13", {"start": v(80.42, -140.62) * mm, "end": v(74.64, -150.62) * mm});
            skLineSegment(sketch, "E20.15.4.13", {"start": v(74.64, -130.62) * mm, "end": v(80.42, -140.62) * mm});
            skLineSegment(sketch, "E20.18.4.13", {"start": v(76.8, -129.38) * mm, "end": v(82.58, -119.38) * mm});
            skLineSegment(sketch, "E20.21.4.13", {"start": v(82.58, -139.37) * mm, "end": v(76.8, -129.38) * mm});
            skLineSegment(sketch, "E20.24.4.13", {"start": v(82.58, -119.37) * mm, "end": v(94.13, -119.37) * mm});
            skLineSegment(sketch, "E20.27.4.13", {"start": v(94.13, -119.38) * mm, "end": v(99.9, -129.37) * mm});
            skLineSegment(sketch, "E20.30.4.13", {"start": v(99.9, -129.38) * mm, "end": v(94.13, -139.38) * mm});
            skLineSegment(sketch, "E20.33.4.13", {"start": v(94.13, -139.38) * mm, "end": v(82.58, -139.38) * mm});
            skLineSegment(sketch, "E20.0.4.14", {"start": v(63.1, -153.12) * mm, "end": v(74.64, -153.12) * mm});
            skLineSegment(sketch, "E20.3.4.14", {"start": v(57.32, -163.13) * mm, "end": v(63.1, -153.13) * mm});
            skLineSegment(sketch, "E20.6.4.14", {"start": v(63.1, -173.13) * mm, "end": v(57.32, -163.13) * mm});
            skLineSegment(sketch, "E20.9.4.14", {"start": v(74.64, -173.13) * mm, "end": v(63.1, -173.13) * mm});
            skLineSegment(sketch, "E20.12.4.14", {"start": v(80.42, -163.13) * mm, "end": v(74.64, -173.13) * mm});
            skLineSegment(sketch, "E20.15.4.14", {"start": v(74.64, -153.12) * mm, "end": v(80.42, -163.12) * mm});
            skLineSegment(sketch, "E20.18.4.14", {"start": v(76.8, -151.88) * mm, "end": v(82.58, -141.88) * mm});
            skLineSegment(sketch, "E20.21.4.14", {"start": v(82.58, -161.87) * mm, "end": v(76.8, -151.88) * mm});
            skLineSegment(sketch, "E20.24.4.14", {"start": v(82.58, -141.88) * mm, "end": v(94.13, -141.88) * mm});
            skLineSegment(sketch, "E20.27.4.14", {"start": v(94.13, -141.88) * mm, "end": v(99.9, -151.87) * mm});
            skLineSegment(sketch, "E20.30.4.14", {"start": v(99.9, -151.88) * mm, "end": v(94.13, -161.88) * mm});
            skLineSegment(sketch, "E20.33.4.14", {"start": v(94.13, -161.88) * mm, "end": v(82.58, -161.88) * mm});
            skSolve(sketch);
        }
        {
            var Q0;
            {var subQ0=sQuery(id+"F4.wireOp",EDGE,"E15.0");var subQ1=sQuery(id+"F4.wireOp",EDGE,"E10");var subQ2=makeQuery(id+"F4.imprint","INTERSECT",VERTEX,{"derivedFrom":[subQ1,subQ0]});Q0=makeQuery(id+"F4.imprint","IMPRINT",FACE,{"disambiguationData":[TD([[makeQuery(id+"F4.imprint","IMPRINT",EDGE,{"disambiguationData":[TD([[subQ2,-1.0]])],"derivedFrom":subQ1}),-1.0]])]});}
            var Q1;
            {var subQ0=sQuery(id+"F4.wireOp",EDGE,"E18.0.1.7");Q1=makeQuery(id+"F4.imprint","IMPRINT",FACE,{"disambiguationData":[TD([[makeQuery(id+"F4.imprint","IMPRINT",EDGE,{"derivedFrom":subQ0}),-1.0]])]});}
            var Q2;
            {var subQ5=sQuery(id+"F4.wireOp",EDGE,"E18.1.0.3");Q2=makeQuery(id+"F4.imprint","IMPRINT",FACE,{"disambiguationData":[TD([[makeQuery(id+"F4.imprint","IMPRINT",EDGE,{"derivedFrom":subQ5}),-1.0]])]});}
            var Q3;
            {var subQ4=sQuery(id+"F4.wireOp",EDGE,"E18.1.1.7");Q3=makeQuery(id+"F4.imprint","IMPRINT",FACE,{"disambiguationData":[TD([[makeQuery(id+"F4.imprint","IMPRINT",EDGE,{"derivedFrom":subQ4}),-1.0]])]});}
            var Q4;
            {var subQ5=sQuery(id+"F4.wireOp",EDGE,"E18.2.0.3");Q4=makeQuery(id+"F4.imprint","IMPRINT",FACE,{"disambiguationData":[TD([[makeQuery(id+"F4.imprint","IMPRINT",EDGE,{"derivedFrom":subQ5}),-1.0]])]});}
            var Q5;
            {var subQ4=sQuery(id+"F4.wireOp",EDGE,"E18.2.1.7");Q5=makeQuery(id+"F4.imprint","IMPRINT",FACE,{"disambiguationData":[TD([[makeQuery(id+"F4.imprint","IMPRINT",EDGE,{"derivedFrom":subQ4}),-1.0]])]});}
            var Q6;
            {var subQ5=sQuery(id+"F4.wireOp",EDGE,"E19.9.3.0");Q6=makeQuery(id+"F4.imprint","IMPRINT",FACE,{"disambiguationData":[TD([[makeQuery(id+"F4.imprint","IMPRINT",EDGE,{"derivedFrom":subQ5}),-1.0]])]});}
            var Q7;
            {var subQ4=sQuery(id+"F4.wireOp",EDGE,"E19.21.3.1");Q7=makeQuery(id+"F4.imprint","IMPRINT",FACE,{"disambiguationData":[TD([[makeQuery(id+"F4.imprint","IMPRINT",EDGE,{"derivedFrom":subQ4}),-1.0]])]});}
            var Q8;
            {var subQ5=sQuery(id+"F4.wireOp",EDGE,"E19.9.4.0");Q8=makeQuery(id+"F4.imprint","IMPRINT",FACE,{"disambiguationData":[TD([[makeQuery(id+"F4.imprint","IMPRINT",EDGE,{"derivedFrom":subQ5}),-1.0]])]});}
            var Q9;
            {var subQ0=sQuery(id+"F4.wireOp",EDGE,"E19.21.4.1");Q9=makeQuery(id+"F4.imprint","IMPRINT",FACE,{"disambiguationData":[TD([[makeQuery(id+"F4.imprint","IMPRINT",EDGE,{"derivedFrom":subQ0}),-1.0]])]});}
            var Q10;
            {var subQ0=sQuery(id+"F4.wireOp",EDGE,"E18.0.1.4");Q10=makeQuery(id+"F4.imprint","IMPRINT",FACE,{"disambiguationData":[TD([[makeQuery(id+"F4.imprint","IMPRINT",EDGE,{"derivedFrom":subQ0}),-1.0]])]});}
            var Q11;
            Q11=makeQuery(id+"F4.imprint","IMPRINT",FACE,{"disambiguationData":[TD([[makeQuery(id+"F4.imprint","IMPRINT",EDGE,{"derivedFrom":sQuery(id+"F4.wireOp",EDGE,"E18.1.1.0")}),-1.0]])]});
            var Q12;
            Q12=makeQuery(id+"F4.imprint","IMPRINT",FACE,{"disambiguationData":[TD([[makeQuery(id+"F4.imprint","IMPRINT",EDGE,{"derivedFrom":sQuery(id+"F4.wireOp",EDGE,"E18.2.1.0")}),-1.0]])]});
            var Q13;
            Q13=makeQuery(id+"F4.imprint","IMPRINT",FACE,{"disambiguationData":[TD([[makeQuery(id+"F4.imprint","IMPRINT",EDGE,{"derivedFrom":sQuery(id+"F4.wireOp",EDGE,"E19.0.3.1")}),-1.0]])]});
            var Q14;
            Q14=makeQuery(id+"F4.imprint","IMPRINT",FACE,{"disambiguationData":[TD([[makeQuery(id+"F4.imprint","IMPRINT",EDGE,{"derivedFrom":sQuery(id+"F4.wireOp",EDGE,"E19.0.4.1")}),-1.0]])]});
            var Q15;
            Q15=makeQuery(id+"F4.imprint","IMPRINT",FACE,{"disambiguationData":[TD([[makeQuery(id+"F4.imprint","IMPRINT",EDGE,{"derivedFrom":sQuery(id+"F4.wireOp",EDGE,"E20.18.0.2")}),-1.0]])]});
            var Q16;
            Q16=makeQuery(id+"F4.imprint","IMPRINT",FACE,{"disambiguationData":[TD([[makeQuery(id+"F4.imprint","IMPRINT",EDGE,{"derivedFrom":sQuery(id+"F4.wireOp",EDGE,"E20.18.1.2")}),-1.0]])]});
            var Q17;
            Q17=makeQuery(id+"F4.imprint","IMPRINT",FACE,{"disambiguationData":[TD([[makeQuery(id+"F4.imprint","IMPRINT",EDGE,{"derivedFrom":sQuery(id+"F4.wireOp",EDGE,"E20.18.2.2")}),-1.0]])]});
            var Q18;
            Q18=makeQuery(id+"F4.imprint","IMPRINT",FACE,{"disambiguationData":[TD([[makeQuery(id+"F4.imprint","IMPRINT",EDGE,{"derivedFrom":sQuery(id+"F4.wireOp",EDGE,"E20.18.3.2")}),-1.0]])]});
            var Q19;
            {var subQ1=sQuery(id+"F4.wireOp",EDGE,"E20.18.4.2");Q19=makeQuery(id+"F4.imprint","IMPRINT",FACE,{"disambiguationData":[TD([[makeQuery(id+"F4.imprint","IMPRINT",EDGE,{"derivedFrom":subQ1}),-1.0]])]});}
            var Q20;
            {var subQ0=sQuery(id+"F4.wireOp",EDGE,"E20.12.0.2");Q20=makeQuery(id+"F4.imprint","IMPRINT",FACE,{"disambiguationData":[TD([[makeQuery(id+"F4.imprint","IMPRINT",EDGE,{"derivedFrom":subQ0}),-1.0]])]});}
            var Q21;
            Q21=makeQuery(id+"F4.imprint","IMPRINT",FACE,{"disambiguationData":[TD([[makeQuery(id+"F4.imprint","IMPRINT",EDGE,{"derivedFrom":sQuery(id+"F4.wireOp",EDGE,"E20.0.1.2")}),-1.0]])]});
            var Q22;
            Q22=makeQuery(id+"F4.imprint","IMPRINT",FACE,{"disambiguationData":[TD([[makeQuery(id+"F4.imprint","IMPRINT",EDGE,{"derivedFrom":sQuery(id+"F4.wireOp",EDGE,"E20.0.2.2")}),-1.0]])]});
            var Q23;
            Q23=makeQuery(id+"F4.imprint","IMPRINT",FACE,{"disambiguationData":[TD([[makeQuery(id+"F4.imprint","IMPRINT",EDGE,{"derivedFrom":sQuery(id+"F4.wireOp",EDGE,"E20.0.3.2")}),-1.0]])]});
            var Q24;
            Q24=makeQuery(id+"F4.imprint","IMPRINT",FACE,{"disambiguationData":[TD([[makeQuery(id+"F4.imprint","IMPRINT",EDGE,{"derivedFrom":sQuery(id+"F4.wireOp",EDGE,"E20.0.4.2")}),-1.0]])]});
            var Q25;
            Q25=makeQuery(id+"F4.imprint","IMPRINT",FACE,{"disambiguationData":[TD([[makeQuery(id+"F4.imprint","IMPRINT",EDGE,{"derivedFrom":sQuery(id+"F4.wireOp",EDGE,"E20.18.0.3")}),-1.0]])]});
            var Q26;
            Q26=makeQuery(id+"F4.imprint","IMPRINT",FACE,{"disambiguationData":[TD([[makeQuery(id+"F4.imprint","IMPRINT",EDGE,{"derivedFrom":sQuery(id+"F4.wireOp",EDGE,"E20.18.1.3")}),-1.0]])]});
            var Q27;
            Q27=makeQuery(id+"F4.imprint","IMPRINT",FACE,{"disambiguationData":[TD([[makeQuery(id+"F4.imprint","IMPRINT",EDGE,{"derivedFrom":sQuery(id+"F4.wireOp",EDGE,"E20.18.2.3")}),-1.0]])]});
            var Q28;
            Q28=makeQuery(id+"F4.imprint","IMPRINT",FACE,{"disambiguationData":[TD([[makeQuery(id+"F4.imprint","IMPRINT",EDGE,{"derivedFrom":sQuery(id+"F4.wireOp",EDGE,"E20.18.3.3")}),-1.0]])]});
            var Q29;
            {var subQ1=sQuery(id+"F4.wireOp",EDGE,"E20.18.4.3");Q29=makeQuery(id+"F4.imprint","IMPRINT",FACE,{"disambiguationData":[TD([[makeQuery(id+"F4.imprint","IMPRINT",EDGE,{"derivedFrom":subQ1}),-1.0]])]});}
            var Q30;
            {var subQ0=sQuery(id+"F4.wireOp",EDGE,"E20.12.0.3");Q30=makeQuery(id+"F4.imprint","IMPRINT",FACE,{"disambiguationData":[TD([[makeQuery(id+"F4.imprint","IMPRINT",EDGE,{"derivedFrom":subQ0}),-1.0]])]});}
            var Q31;
            Q31=makeQuery(id+"F4.imprint","IMPRINT",FACE,{"disambiguationData":[TD([[makeQuery(id+"F4.imprint","IMPRINT",EDGE,{"derivedFrom":sQuery(id+"F4.wireOp",EDGE,"E20.0.1.3")}),-1.0]])]});
            var Q32;
            Q32=makeQuery(id+"F4.imprint","IMPRINT",FACE,{"disambiguationData":[TD([[makeQuery(id+"F4.imprint","IMPRINT",EDGE,{"derivedFrom":sQuery(id+"F4.wireOp",EDGE,"E20.0.2.3")}),-1.0]])]});
            var Q33;
            Q33=makeQuery(id+"F4.imprint","IMPRINT",FACE,{"disambiguationData":[TD([[makeQuery(id+"F4.imprint","IMPRINT",EDGE,{"derivedFrom":sQuery(id+"F4.wireOp",EDGE,"E20.0.3.3")}),-1.0]])]});
            var Q34;
            Q34=makeQuery(id+"F4.imprint","IMPRINT",FACE,{"disambiguationData":[TD([[makeQuery(id+"F4.imprint","IMPRINT",EDGE,{"derivedFrom":sQuery(id+"F4.wireOp",EDGE,"E20.0.4.3")}),-1.0]])]});
            var Q35;
            Q35=makeQuery(id+"F4.imprint","IMPRINT",FACE,{"disambiguationData":[TD([[makeQuery(id+"F4.imprint","IMPRINT",EDGE,{"derivedFrom":sQuery(id+"F4.wireOp",EDGE,"E20.18.0.4")}),-1.0]])]});
            var Q36;
            Q36=makeQuery(id+"F4.imprint","IMPRINT",FACE,{"disambiguationData":[TD([[makeQuery(id+"F4.imprint","IMPRINT",EDGE,{"derivedFrom":sQuery(id+"F4.wireOp",EDGE,"E20.18.1.4")}),-1.0]])]});
            var Q37;
            Q37=makeQuery(id+"F4.imprint","IMPRINT",FACE,{"disambiguationData":[TD([[makeQuery(id+"F4.imprint","IMPRINT",EDGE,{"derivedFrom":sQuery(id+"F4.wireOp",EDGE,"E20.18.2.4")}),-1.0]])]});
            var Q38;
            Q38=makeQuery(id+"F4.imprint","IMPRINT",FACE,{"disambiguationData":[TD([[makeQuery(id+"F4.imprint","IMPRINT",EDGE,{"derivedFrom":sQuery(id+"F4.wireOp",EDGE,"E20.18.3.4")}),-1.0]])]});
            var Q39;
            {var subQ6=sQuery(id+"F4.wireOp",EDGE,"E20.18.4.4");Q39=makeQuery(id+"F4.imprint","IMPRINT",FACE,{"disambiguationData":[TD([[makeQuery(id+"F4.imprint","IMPRINT",EDGE,{"derivedFrom":subQ6}),-1.0]])]});}
            var Q40;
            {var subQ0=sQuery(id+"F4.wireOp",EDGE,"E20.12.0.4");Q40=makeQuery(id+"F4.imprint","IMPRINT",FACE,{"disambiguationData":[TD([[makeQuery(id+"F4.imprint","IMPRINT",EDGE,{"derivedFrom":subQ0}),-1.0]])]});}
            var Q41;
            Q41=makeQuery(id+"F4.imprint","IMPRINT",FACE,{"disambiguationData":[TD([[makeQuery(id+"F4.imprint","IMPRINT",EDGE,{"derivedFrom":sQuery(id+"F4.wireOp",EDGE,"E20.0.1.4")}),-1.0]])]});
            var Q42;
            Q42=makeQuery(id+"F4.imprint","IMPRINT",FACE,{"disambiguationData":[TD([[makeQuery(id+"F4.imprint","IMPRINT",EDGE,{"derivedFrom":sQuery(id+"F4.wireOp",EDGE,"E20.0.2.4")}),-1.0]])]});
            var Q43;
            Q43=makeQuery(id+"F4.imprint","IMPRINT",FACE,{"disambiguationData":[TD([[makeQuery(id+"F4.imprint","IMPRINT",EDGE,{"derivedFrom":sQuery(id+"F4.wireOp",EDGE,"E20.0.3.4")}),-1.0]])]});
            var Q44;
            Q44=makeQuery(id+"F4.imprint","IMPRINT",FACE,{"disambiguationData":[TD([[makeQuery(id+"F4.imprint","IMPRINT",EDGE,{"derivedFrom":sQuery(id+"F4.wireOp",EDGE,"E20.0.4.4")}),-1.0]])]});
            var Q45;
            Q45=makeQuery(id+"F4.imprint","IMPRINT",FACE,{"disambiguationData":[TD([[makeQuery(id+"F4.imprint","IMPRINT",EDGE,{"derivedFrom":sQuery(id+"F4.wireOp",EDGE,"E20.18.0.5")}),-1.0]])]});
            var Q46;
            Q46=makeQuery(id+"F4.imprint","IMPRINT",FACE,{"disambiguationData":[TD([[makeQuery(id+"F4.imprint","IMPRINT",EDGE,{"derivedFrom":sQuery(id+"F4.wireOp",EDGE,"E20.18.1.5")}),-1.0]])]});
            var Q47;
            Q47=makeQuery(id+"F4.imprint","IMPRINT",FACE,{"disambiguationData":[TD([[makeQuery(id+"F4.imprint","IMPRINT",EDGE,{"derivedFrom":sQuery(id+"F4.wireOp",EDGE,"E20.18.2.5")}),-1.0]])]});
            var Q48;
            Q48=makeQuery(id+"F4.imprint","IMPRINT",FACE,{"disambiguationData":[TD([[makeQuery(id+"F4.imprint","IMPRINT",EDGE,{"derivedFrom":sQuery(id+"F4.wireOp",EDGE,"E20.18.3.5")}),-1.0]])]});
            var Q49;
            {var subQ1=sQuery(id+"F4.wireOp",EDGE,"E20.18.4.5");Q49=makeQuery(id+"F4.imprint","IMPRINT",FACE,{"disambiguationData":[TD([[makeQuery(id+"F4.imprint","IMPRINT",EDGE,{"derivedFrom":subQ1}),-1.0]])]});}
            var Q50;
            {var subQ0=sQuery(id+"F4.wireOp",EDGE,"E20.12.0.5");Q50=makeQuery(id+"F4.imprint","IMPRINT",FACE,{"disambiguationData":[TD([[makeQuery(id+"F4.imprint","IMPRINT",EDGE,{"derivedFrom":subQ0}),-1.0]])]});}
            var Q51;
            Q51=makeQuery(id+"F4.imprint","IMPRINT",FACE,{"disambiguationData":[TD([[makeQuery(id+"F4.imprint","IMPRINT",EDGE,{"derivedFrom":sQuery(id+"F4.wireOp",EDGE,"E20.0.1.5")}),-1.0]])]});
            var Q52;
            Q52=makeQuery(id+"F4.imprint","IMPRINT",FACE,{"disambiguationData":[TD([[makeQuery(id+"F4.imprint","IMPRINT",EDGE,{"derivedFrom":sQuery(id+"F4.wireOp",EDGE,"E20.0.2.5")}),-1.0]])]});
            var Q53;
            Q53=makeQuery(id+"F4.imprint","IMPRINT",FACE,{"disambiguationData":[TD([[makeQuery(id+"F4.imprint","IMPRINT",EDGE,{"derivedFrom":sQuery(id+"F4.wireOp",EDGE,"E20.0.3.5")}),-1.0]])]});
            var Q54;
            Q54=makeQuery(id+"F4.imprint","IMPRINT",FACE,{"disambiguationData":[TD([[makeQuery(id+"F4.imprint","IMPRINT",EDGE,{"derivedFrom":sQuery(id+"F4.wireOp",EDGE,"E20.0.4.5")}),-1.0]])]});
            var Q55;
            Q55=makeQuery(id+"F4.imprint","IMPRINT",FACE,{"disambiguationData":[TD([[makeQuery(id+"F4.imprint","IMPRINT",EDGE,{"derivedFrom":sQuery(id+"F4.wireOp",EDGE,"E20.18.0.6")}),-1.0]])]});
            var Q56;
            Q56=makeQuery(id+"F4.imprint","IMPRINT",FACE,{"disambiguationData":[TD([[makeQuery(id+"F4.imprint","IMPRINT",EDGE,{"derivedFrom":sQuery(id+"F4.wireOp",EDGE,"E20.18.1.6")}),-1.0]])]});
            var Q57;
            Q57=makeQuery(id+"F4.imprint","IMPRINT",FACE,{"disambiguationData":[TD([[makeQuery(id+"F4.imprint","IMPRINT",EDGE,{"derivedFrom":sQuery(id+"F4.wireOp",EDGE,"E20.18.2.6")}),-1.0]])]});
            var Q58;
            Q58=makeQuery(id+"F4.imprint","IMPRINT",FACE,{"disambiguationData":[TD([[makeQuery(id+"F4.imprint","IMPRINT",EDGE,{"derivedFrom":sQuery(id+"F4.wireOp",EDGE,"E20.18.3.6")}),-1.0]])]});
            var Q59;
            {var subQ1=sQuery(id+"F4.wireOp",EDGE,"E20.18.4.6");Q59=makeQuery(id+"F4.imprint","IMPRINT",FACE,{"disambiguationData":[TD([[makeQuery(id+"F4.imprint","IMPRINT",EDGE,{"derivedFrom":subQ1}),-1.0]])]});}
            var Q60;
            {var subQ0=sQuery(id+"F4.wireOp",EDGE,"E20.12.0.6");Q60=makeQuery(id+"F4.imprint","IMPRINT",FACE,{"disambiguationData":[TD([[makeQuery(id+"F4.imprint","IMPRINT",EDGE,{"derivedFrom":subQ0}),-1.0]])]});}
            var Q61;
            Q61=makeQuery(id+"F4.imprint","IMPRINT",FACE,{"disambiguationData":[TD([[makeQuery(id+"F4.imprint","IMPRINT",EDGE,{"derivedFrom":sQuery(id+"F4.wireOp",EDGE,"E20.0.1.6")}),-1.0]])]});
            var Q62;
            Q62=makeQuery(id+"F4.imprint","IMPRINT",FACE,{"disambiguationData":[TD([[makeQuery(id+"F4.imprint","IMPRINT",EDGE,{"derivedFrom":sQuery(id+"F4.wireOp",EDGE,"E20.0.2.6")}),-1.0]])]});
            var Q63;
            Q63=makeQuery(id+"F4.imprint","IMPRINT",FACE,{"disambiguationData":[TD([[makeQuery(id+"F4.imprint","IMPRINT",EDGE,{"derivedFrom":sQuery(id+"F4.wireOp",EDGE,"E20.0.3.6")}),-1.0]])]});
            var Q64;
            Q64=makeQuery(id+"F4.imprint","IMPRINT",FACE,{"disambiguationData":[TD([[makeQuery(id+"F4.imprint","IMPRINT",EDGE,{"derivedFrom":sQuery(id+"F4.wireOp",EDGE,"E20.0.4.6")}),-1.0]])]});
            var Q65;
            Q65=makeQuery(id+"F4.imprint","IMPRINT",FACE,{"disambiguationData":[TD([[makeQuery(id+"F4.imprint","IMPRINT",EDGE,{"derivedFrom":sQuery(id+"F4.wireOp",EDGE,"E20.18.0.7")}),-1.0]])]});
            var Q66;
            Q66=makeQuery(id+"F4.imprint","IMPRINT",FACE,{"disambiguationData":[TD([[makeQuery(id+"F4.imprint","IMPRINT",EDGE,{"derivedFrom":sQuery(id+"F4.wireOp",EDGE,"E20.18.1.7")}),-1.0]])]});
            var Q67;
            Q67=makeQuery(id+"F4.imprint","IMPRINT",FACE,{"disambiguationData":[TD([[makeQuery(id+"F4.imprint","IMPRINT",EDGE,{"derivedFrom":sQuery(id+"F4.wireOp",EDGE,"E20.18.2.7")}),-1.0]])]});
            var Q68;
            Q68=makeQuery(id+"F4.imprint","IMPRINT",FACE,{"disambiguationData":[TD([[makeQuery(id+"F4.imprint","IMPRINT",EDGE,{"derivedFrom":sQuery(id+"F4.wireOp",EDGE,"E20.18.3.7")}),-1.0]])]});
            var Q69;
            {var subQ1=sQuery(id+"F4.wireOp",EDGE,"E20.18.4.7");Q69=makeQuery(id+"F4.imprint","IMPRINT",FACE,{"disambiguationData":[TD([[makeQuery(id+"F4.imprint","IMPRINT",EDGE,{"derivedFrom":subQ1}),-1.0]])]});}
            var Q70;
            {var subQ0=sQuery(id+"F4.wireOp",EDGE,"E20.12.0.7");Q70=makeQuery(id+"F4.imprint","IMPRINT",FACE,{"disambiguationData":[TD([[makeQuery(id+"F4.imprint","IMPRINT",EDGE,{"derivedFrom":subQ0}),-1.0]])]});}
            var Q71;
            Q71=makeQuery(id+"F4.imprint","IMPRINT",FACE,{"disambiguationData":[TD([[makeQuery(id+"F4.imprint","IMPRINT",EDGE,{"derivedFrom":sQuery(id+"F4.wireOp",EDGE,"E20.0.1.7")}),-1.0]])]});
            var Q72;
            Q72=makeQuery(id+"F4.imprint","IMPRINT",FACE,{"disambiguationData":[TD([[makeQuery(id+"F4.imprint","IMPRINT",EDGE,{"derivedFrom":sQuery(id+"F4.wireOp",EDGE,"E20.0.2.7")}),-1.0]])]});
            var Q73;
            Q73=makeQuery(id+"F4.imprint","IMPRINT",FACE,{"disambiguationData":[TD([[makeQuery(id+"F4.imprint","IMPRINT",EDGE,{"derivedFrom":sQuery(id+"F4.wireOp",EDGE,"E20.0.3.7")}),-1.0]])]});
            var Q74;
            Q74=makeQuery(id+"F4.imprint","IMPRINT",FACE,{"disambiguationData":[TD([[makeQuery(id+"F4.imprint","IMPRINT",EDGE,{"derivedFrom":sQuery(id+"F4.wireOp",EDGE,"E20.0.4.7")}),-1.0]])]});
            var Q75;
            Q75=makeQuery(id+"F4.imprint","IMPRINT",FACE,{"disambiguationData":[TD([[makeQuery(id+"F4.imprint","IMPRINT",EDGE,{"derivedFrom":sQuery(id+"F4.wireOp",EDGE,"E20.18.0.8")}),-1.0]])]});
            var Q76;
            Q76=makeQuery(id+"F4.imprint","IMPRINT",FACE,{"disambiguationData":[TD([[makeQuery(id+"F4.imprint","IMPRINT",EDGE,{"derivedFrom":sQuery(id+"F4.wireOp",EDGE,"E20.18.1.8")}),-1.0]])]});
            var Q77;
            Q77=makeQuery(id+"F4.imprint","IMPRINT",FACE,{"disambiguationData":[TD([[makeQuery(id+"F4.imprint","IMPRINT",EDGE,{"derivedFrom":sQuery(id+"F4.wireOp",EDGE,"E20.18.2.8")}),-1.0]])]});
            var Q78;
            Q78=makeQuery(id+"F4.imprint","IMPRINT",FACE,{"disambiguationData":[TD([[makeQuery(id+"F4.imprint","IMPRINT",EDGE,{"derivedFrom":sQuery(id+"F4.wireOp",EDGE,"E20.18.3.8")}),-1.0]])]});
            var Q79;
            {var subQ1=sQuery(id+"F4.wireOp",EDGE,"E20.18.4.8");Q79=makeQuery(id+"F4.imprint","IMPRINT",FACE,{"disambiguationData":[TD([[makeQuery(id+"F4.imprint","IMPRINT",EDGE,{"derivedFrom":subQ1}),-1.0]])]});}
            var Q80;
            {var subQ0=sQuery(id+"F4.wireOp",EDGE,"E20.12.0.8");Q80=makeQuery(id+"F4.imprint","IMPRINT",FACE,{"disambiguationData":[TD([[makeQuery(id+"F4.imprint","IMPRINT",EDGE,{"derivedFrom":subQ0}),-1.0]])]});}
            var Q81;
            Q81=makeQuery(id+"F4.imprint","IMPRINT",FACE,{"disambiguationData":[TD([[makeQuery(id+"F4.imprint","IMPRINT",EDGE,{"derivedFrom":sQuery(id+"F4.wireOp",EDGE,"E20.0.1.8")}),-1.0]])]});
            var Q82;
            Q82=makeQuery(id+"F4.imprint","IMPRINT",FACE,{"disambiguationData":[TD([[makeQuery(id+"F4.imprint","IMPRINT",EDGE,{"derivedFrom":sQuery(id+"F4.wireOp",EDGE,"E20.0.2.8")}),-1.0]])]});
            var Q83;
            Q83=makeQuery(id+"F4.imprint","IMPRINT",FACE,{"disambiguationData":[TD([[makeQuery(id+"F4.imprint","IMPRINT",EDGE,{"derivedFrom":sQuery(id+"F4.wireOp",EDGE,"E20.0.3.8")}),-1.0]])]});
            var Q84;
            Q84=makeQuery(id+"F4.imprint","IMPRINT",FACE,{"disambiguationData":[TD([[makeQuery(id+"F4.imprint","IMPRINT",EDGE,{"derivedFrom":sQuery(id+"F4.wireOp",EDGE,"E20.0.4.8")}),-1.0]])]});
            var Q85;
            Q85=makeQuery(id+"F4.imprint","IMPRINT",FACE,{"disambiguationData":[TD([[makeQuery(id+"F4.imprint","IMPRINT",EDGE,{"derivedFrom":sQuery(id+"F4.wireOp",EDGE,"E20.18.0.9")}),-1.0]])]});
            var Q86;
            Q86=makeQuery(id+"F4.imprint","IMPRINT",FACE,{"disambiguationData":[TD([[makeQuery(id+"F4.imprint","IMPRINT",EDGE,{"derivedFrom":sQuery(id+"F4.wireOp",EDGE,"E20.18.1.9")}),-1.0]])]});
            var Q87;
            Q87=makeQuery(id+"F4.imprint","IMPRINT",FACE,{"disambiguationData":[TD([[makeQuery(id+"F4.imprint","IMPRINT",EDGE,{"derivedFrom":sQuery(id+"F4.wireOp",EDGE,"E20.18.2.9")}),-1.0]])]});
            var Q88;
            Q88=makeQuery(id+"F4.imprint","IMPRINT",FACE,{"disambiguationData":[TD([[makeQuery(id+"F4.imprint","IMPRINT",EDGE,{"derivedFrom":sQuery(id+"F4.wireOp",EDGE,"E20.18.3.9")}),-1.0]])]});
            var Q89;
            {var subQ1=sQuery(id+"F4.wireOp",EDGE,"E20.18.4.9");Q89=makeQuery(id+"F4.imprint","IMPRINT",FACE,{"disambiguationData":[TD([[makeQuery(id+"F4.imprint","IMPRINT",EDGE,{"derivedFrom":subQ1}),-1.0]])]});}
            var Q90;
            {var subQ0=sQuery(id+"F4.wireOp",EDGE,"E20.12.0.9");Q90=makeQuery(id+"F4.imprint","IMPRINT",FACE,{"disambiguationData":[TD([[makeQuery(id+"F4.imprint","IMPRINT",EDGE,{"derivedFrom":subQ0}),-1.0]])]});}
            var Q91;
            Q91=makeQuery(id+"F4.imprint","IMPRINT",FACE,{"disambiguationData":[TD([[makeQuery(id+"F4.imprint","IMPRINT",EDGE,{"derivedFrom":sQuery(id+"F4.wireOp",EDGE,"E20.0.1.9")}),-1.0]])]});
            var Q92;
            Q92=makeQuery(id+"F4.imprint","IMPRINT",FACE,{"disambiguationData":[TD([[makeQuery(id+"F4.imprint","IMPRINT",EDGE,{"derivedFrom":sQuery(id+"F4.wireOp",EDGE,"E20.0.2.9")}),-1.0]])]});
            var Q93;
            Q93=makeQuery(id+"F4.imprint","IMPRINT",FACE,{"disambiguationData":[TD([[makeQuery(id+"F4.imprint","IMPRINT",EDGE,{"derivedFrom":sQuery(id+"F4.wireOp",EDGE,"E20.0.3.9")}),-1.0]])]});
            var Q94;
            Q94=makeQuery(id+"F4.imprint","IMPRINT",FACE,{"disambiguationData":[TD([[makeQuery(id+"F4.imprint","IMPRINT",EDGE,{"derivedFrom":sQuery(id+"F4.wireOp",EDGE,"E20.0.4.9")}),-1.0]])]});
            var Q95;
            Q95=makeQuery(id+"F4.imprint","IMPRINT",FACE,{"disambiguationData":[TD([[makeQuery(id+"F4.imprint","IMPRINT",EDGE,{"derivedFrom":sQuery(id+"F4.wireOp",EDGE,"E20.18.0.10")}),-1.0]])]});
            var Q96;
            Q96=makeQuery(id+"F4.imprint","IMPRINT",FACE,{"disambiguationData":[TD([[makeQuery(id+"F4.imprint","IMPRINT",EDGE,{"derivedFrom":sQuery(id+"F4.wireOp",EDGE,"E20.18.1.10")}),-1.0]])]});
            var Q97;
            Q97=makeQuery(id+"F4.imprint","IMPRINT",FACE,{"disambiguationData":[TD([[makeQuery(id+"F4.imprint","IMPRINT",EDGE,{"derivedFrom":sQuery(id+"F4.wireOp",EDGE,"E20.18.2.10")}),-1.0]])]});
            var Q98;
            Q98=makeQuery(id+"F4.imprint","IMPRINT",FACE,{"disambiguationData":[TD([[makeQuery(id+"F4.imprint","IMPRINT",EDGE,{"derivedFrom":sQuery(id+"F4.wireOp",EDGE,"E20.18.3.10")}),-1.0]])]});
            var Q99;
            {var subQ1=sQuery(id+"F4.wireOp",EDGE,"E20.18.4.10");Q99=makeQuery(id+"F4.imprint","IMPRINT",FACE,{"disambiguationData":[TD([[makeQuery(id+"F4.imprint","IMPRINT",EDGE,{"derivedFrom":subQ1}),-1.0]])]});}
            var Q100;
            {var subQ0=sQuery(id+"F4.wireOp",EDGE,"E20.12.0.10");Q100=makeQuery(id+"F4.imprint","IMPRINT",FACE,{"disambiguationData":[TD([[makeQuery(id+"F4.imprint","IMPRINT",EDGE,{"derivedFrom":subQ0}),-1.0]])]});}
            var Q101;
            Q101=makeQuery(id+"F4.imprint","IMPRINT",FACE,{"disambiguationData":[TD([[makeQuery(id+"F4.imprint","IMPRINT",EDGE,{"derivedFrom":sQuery(id+"F4.wireOp",EDGE,"E20.0.1.10")}),-1.0]])]});
            var Q102;
            Q102=makeQuery(id+"F4.imprint","IMPRINT",FACE,{"disambiguationData":[TD([[makeQuery(id+"F4.imprint","IMPRINT",EDGE,{"derivedFrom":sQuery(id+"F4.wireOp",EDGE,"E20.0.2.10")}),-1.0]])]});
            var Q103;
            Q103=makeQuery(id+"F4.imprint","IMPRINT",FACE,{"disambiguationData":[TD([[makeQuery(id+"F4.imprint","IMPRINT",EDGE,{"derivedFrom":sQuery(id+"F4.wireOp",EDGE,"E20.0.3.10")}),-1.0]])]});
            var Q104;
            Q104=makeQuery(id+"F4.imprint","IMPRINT",FACE,{"disambiguationData":[TD([[makeQuery(id+"F4.imprint","IMPRINT",EDGE,{"derivedFrom":sQuery(id+"F4.wireOp",EDGE,"E20.0.4.10")}),-1.0]])]});
            var Q105;
            Q105=makeQuery(id+"F4.imprint","IMPRINT",FACE,{"disambiguationData":[TD([[makeQuery(id+"F4.imprint","IMPRINT",EDGE,{"derivedFrom":sQuery(id+"F4.wireOp",EDGE,"E20.18.0.11")}),-1.0]])]});
            var Q106;
            Q106=makeQuery(id+"F4.imprint","IMPRINT",FACE,{"disambiguationData":[TD([[makeQuery(id+"F4.imprint","IMPRINT",EDGE,{"derivedFrom":sQuery(id+"F4.wireOp",EDGE,"E20.18.1.11")}),-1.0]])]});
            var Q107;
            Q107=makeQuery(id+"F4.imprint","IMPRINT",FACE,{"disambiguationData":[TD([[makeQuery(id+"F4.imprint","IMPRINT",EDGE,{"derivedFrom":sQuery(id+"F4.wireOp",EDGE,"E20.18.2.11")}),-1.0]])]});
            var Q108;
            Q108=makeQuery(id+"F4.imprint","IMPRINT",FACE,{"disambiguationData":[TD([[makeQuery(id+"F4.imprint","IMPRINT",EDGE,{"derivedFrom":sQuery(id+"F4.wireOp",EDGE,"E20.18.3.11")}),-1.0]])]});
            var Q109;
            {var subQ1=sQuery(id+"F4.wireOp",EDGE,"E20.18.4.11");Q109=makeQuery(id+"F4.imprint","IMPRINT",FACE,{"disambiguationData":[TD([[makeQuery(id+"F4.imprint","IMPRINT",EDGE,{"derivedFrom":subQ1}),-1.0]])]});}
            var Q110;
            {var subQ0=sQuery(id+"F4.wireOp",EDGE,"E20.12.0.11");Q110=makeQuery(id+"F4.imprint","IMPRINT",FACE,{"disambiguationData":[TD([[makeQuery(id+"F4.imprint","IMPRINT",EDGE,{"derivedFrom":subQ0}),-1.0]])]});}
            var Q111;
            Q111=makeQuery(id+"F4.imprint","IMPRINT",FACE,{"disambiguationData":[TD([[makeQuery(id+"F4.imprint","IMPRINT",EDGE,{"derivedFrom":sQuery(id+"F4.wireOp",EDGE,"E20.0.1.11")}),-1.0]])]});
            var Q112;
            Q112=makeQuery(id+"F4.imprint","IMPRINT",FACE,{"disambiguationData":[TD([[makeQuery(id+"F4.imprint","IMPRINT",EDGE,{"derivedFrom":sQuery(id+"F4.wireOp",EDGE,"E20.0.2.11")}),-1.0]])]});
            var Q113;
            Q113=makeQuery(id+"F4.imprint","IMPRINT",FACE,{"disambiguationData":[TD([[makeQuery(id+"F4.imprint","IMPRINT",EDGE,{"derivedFrom":sQuery(id+"F4.wireOp",EDGE,"E20.0.3.11")}),-1.0]])]});
            var Q114;
            Q114=makeQuery(id+"F4.imprint","IMPRINT",FACE,{"disambiguationData":[TD([[makeQuery(id+"F4.imprint","IMPRINT",EDGE,{"derivedFrom":sQuery(id+"F4.wireOp",EDGE,"E20.0.4.11")}),-1.0]])]});
            var Q115;
            Q115=makeQuery(id+"F4.imprint","IMPRINT",FACE,{"disambiguationData":[TD([[makeQuery(id+"F4.imprint","IMPRINT",EDGE,{"derivedFrom":sQuery(id+"F4.wireOp",EDGE,"E20.18.0.12")}),-1.0]])]});
            var Q116;
            Q116=makeQuery(id+"F4.imprint","IMPRINT",FACE,{"disambiguationData":[TD([[makeQuery(id+"F4.imprint","IMPRINT",EDGE,{"derivedFrom":sQuery(id+"F4.wireOp",EDGE,"E20.18.1.12")}),-1.0]])]});
            var Q117;
            Q117=makeQuery(id+"F4.imprint","IMPRINT",FACE,{"disambiguationData":[TD([[makeQuery(id+"F4.imprint","IMPRINT",EDGE,{"derivedFrom":sQuery(id+"F4.wireOp",EDGE,"E20.18.2.12")}),-1.0]])]});
            var Q118;
            Q118=makeQuery(id+"F4.imprint","IMPRINT",FACE,{"disambiguationData":[TD([[makeQuery(id+"F4.imprint","IMPRINT",EDGE,{"derivedFrom":sQuery(id+"F4.wireOp",EDGE,"E20.18.3.12")}),-1.0]])]});
            var Q119;
            {var subQ1=sQuery(id+"F4.wireOp",EDGE,"E20.18.4.12");Q119=makeQuery(id+"F4.imprint","IMPRINT",FACE,{"disambiguationData":[TD([[makeQuery(id+"F4.imprint","IMPRINT",EDGE,{"derivedFrom":subQ1}),-1.0]])]});}
            var Q120;
            {var subQ0=sQuery(id+"F4.wireOp",EDGE,"E20.12.0.12");Q120=makeQuery(id+"F4.imprint","IMPRINT",FACE,{"disambiguationData":[TD([[makeQuery(id+"F4.imprint","IMPRINT",EDGE,{"derivedFrom":subQ0}),-1.0]])]});}
            var Q121;
            Q121=makeQuery(id+"F4.imprint","IMPRINT",FACE,{"disambiguationData":[TD([[makeQuery(id+"F4.imprint","IMPRINT",EDGE,{"derivedFrom":sQuery(id+"F4.wireOp",EDGE,"E20.0.1.12")}),-1.0]])]});
            var Q122;
            Q122=makeQuery(id+"F4.imprint","IMPRINT",FACE,{"disambiguationData":[TD([[makeQuery(id+"F4.imprint","IMPRINT",EDGE,{"derivedFrom":sQuery(id+"F4.wireOp",EDGE,"E20.0.2.12")}),-1.0]])]});
            var Q123;
            Q123=makeQuery(id+"F4.imprint","IMPRINT",FACE,{"disambiguationData":[TD([[makeQuery(id+"F4.imprint","IMPRINT",EDGE,{"derivedFrom":sQuery(id+"F4.wireOp",EDGE,"E20.0.3.12")}),-1.0]])]});
            var Q124;
            Q124=makeQuery(id+"F4.imprint","IMPRINT",FACE,{"disambiguationData":[TD([[makeQuery(id+"F4.imprint","IMPRINT",EDGE,{"derivedFrom":sQuery(id+"F4.wireOp",EDGE,"E20.0.4.12")}),-1.0]])]});
            var Q125;
            Q125=makeQuery(id+"F4.imprint","IMPRINT",FACE,{"disambiguationData":[TD([[makeQuery(id+"F4.imprint","IMPRINT",EDGE,{"derivedFrom":sQuery(id+"F4.wireOp",EDGE,"E20.18.0.13")}),-1.0]])]});
            var Q126;
            Q126=makeQuery(id+"F4.imprint","IMPRINT",FACE,{"disambiguationData":[TD([[makeQuery(id+"F4.imprint","IMPRINT",EDGE,{"derivedFrom":sQuery(id+"F4.wireOp",EDGE,"E20.18.1.13")}),-1.0]])]});
            var Q127;
            Q127=makeQuery(id+"F4.imprint","IMPRINT",FACE,{"disambiguationData":[TD([[makeQuery(id+"F4.imprint","IMPRINT",EDGE,{"derivedFrom":sQuery(id+"F4.wireOp",EDGE,"E20.18.2.13")}),-1.0]])]});
            var Q128;
            Q128=makeQuery(id+"F4.imprint","IMPRINT",FACE,{"disambiguationData":[TD([[makeQuery(id+"F4.imprint","IMPRINT",EDGE,{"derivedFrom":sQuery(id+"F4.wireOp",EDGE,"E20.18.3.13")}),-1.0]])]});
            var Q129;
            {var subQ1=sQuery(id+"F4.wireOp",EDGE,"E20.18.4.13");Q129=makeQuery(id+"F4.imprint","IMPRINT",FACE,{"disambiguationData":[TD([[makeQuery(id+"F4.imprint","IMPRINT",EDGE,{"derivedFrom":subQ1}),-1.0]])]});}
            var Q130;
            {var subQ0=sQuery(id+"F4.wireOp",EDGE,"E20.15.0.13");Q130=makeQuery(id+"F4.imprint","IMPRINT",FACE,{"disambiguationData":[TD([[makeQuery(id+"F4.imprint","IMPRINT",EDGE,{"derivedFrom":subQ0}),-1.0]])]});}
            var Q131;
            {var subQ5=sQuery(id+"F4.wireOp",EDGE,"E20.24.0.14");Q131=makeQuery(id+"F4.imprint","IMPRINT",FACE,{"disambiguationData":[TD([[makeQuery(id+"F4.imprint","IMPRINT",EDGE,{"derivedFrom":subQ5}),-1.0]])]});}
            var Q132;
            {var subQ5=sQuery(id+"F4.wireOp",EDGE,"E20.24.1.14");Q132=makeQuery(id+"F4.imprint","IMPRINT",FACE,{"disambiguationData":[TD([[makeQuery(id+"F4.imprint","IMPRINT",EDGE,{"derivedFrom":subQ5}),-1.0]])]});}
            var Q133;
            Q133=makeQuery(id+"F4.imprint","IMPRINT",FACE,{"disambiguationData":[TD([[makeQuery(id+"F4.imprint","IMPRINT",EDGE,{"derivedFrom":sQuery(id+"F4.wireOp",EDGE,"E20.0.2.13")}),-1.0]])]});
            var Q134;
            {var subQ5=sQuery(id+"F4.wireOp",EDGE,"E20.24.2.14");Q134=makeQuery(id+"F4.imprint","IMPRINT",FACE,{"disambiguationData":[TD([[makeQuery(id+"F4.imprint","IMPRINT",EDGE,{"derivedFrom":subQ5}),-1.0]])]});}
            var Q135;
            Q135=makeQuery(id+"F4.imprint","IMPRINT",FACE,{"disambiguationData":[TD([[makeQuery(id+"F4.imprint","IMPRINT",EDGE,{"derivedFrom":sQuery(id+"F4.wireOp",EDGE,"E20.0.3.13")}),-1.0]])]});
            var Q136;
            {var subQ5=sQuery(id+"F4.wireOp",EDGE,"E20.24.3.14");Q136=makeQuery(id+"F4.imprint","IMPRINT",FACE,{"disambiguationData":[TD([[makeQuery(id+"F4.imprint","IMPRINT",EDGE,{"derivedFrom":subQ5}),-1.0]])]});}
            var Q137;
            Q137=makeQuery(id+"F4.imprint","IMPRINT",FACE,{"disambiguationData":[TD([[makeQuery(id+"F4.imprint","IMPRINT",EDGE,{"derivedFrom":sQuery(id+"F4.wireOp",EDGE,"E20.0.4.13")}),-1.0]])]});
            var Q138;
            {var subQ0=sQuery(id+"F4.wireOp",EDGE,"E20.18.4.14");var subQ1=sQuery(id+"F4.wireOp",EDGE,"E11");var subQ2=makeQuery(id+"F4.imprint","INTERSECT",VERTEX,{"derivedFrom":[subQ1,subQ0]});Q138=makeQuery(id+"F4.imprint","IMPRINT",FACE,{"disambiguationData":[TD([[makeQuery(id+"F4.imprint","IMPRINT",EDGE,{"disambiguationData":[TD([[subQ2,-1.0]])],"derivedFrom":subQ1}),1.0]])]});}
            var Q139;
            Q139=makeQuery(id+"F4.imprint","IMPRINT",FACE,{"disambiguationData":[TD([[makeQuery(id+"F4.imprint","IMPRINT",EDGE,{"derivedFrom":sQuery(id+"F4.wireOp",EDGE,"E20.0.1.13")}),-1.0]])]});
            var Q140;
            Q140=makeQuery(id+"F1.opExtrude","CAP_FACE",FACE,{"disambiguationData":[OSD([sQuery(id+"F0.wireOp",EDGE,"E0.bottom"),sQuery(id+"F0.wireOp",EDGE,"E0.top"),sQuery(id+"F0.wireOp",EDGE,"E0.left"),sQuery(id+"F0.wireOp",EDGE,"E0.right")])],"isStart":true});
            extrude(context, id + "F5", {"entities" : qUnion([Q0, Q1, Q2, Q3, Q4, Q5, Q6, Q7, Q8, Q9, Q10, Q11, Q12, Q13, Q14, Q15, Q16, Q17, Q18, Q19, Q20, Q21, Q22, Q23, Q24, Q25, Q26, Q27, Q28, Q29, Q30, Q31, Q32, Q33, Q34, Q35, Q36, Q37, Q38, Q39, Q40, Q41, Q42, Q43, Q44, Q45, Q46, Q47, Q48, Q49, Q50, Q51, Q52, Q53, Q54, Q55, Q56, Q57, Q58, Q59, Q60, Q61, Q62, Q63, Q64, Q65, Q66, Q67, Q68, Q69, Q70, Q71, Q72, Q73, Q74, Q75, Q76, Q77, Q78, Q79, Q80, Q81, Q82, Q83, Q84, Q85, Q86, Q87, Q88, Q89, Q90, Q91, Q92, Q93, Q94, Q95, Q96, Q97, Q98, Q99, Q100, Q101, Q102, Q103, Q104, Q105, Q106, Q107, Q108, Q109, Q110, Q111, Q112, Q113, Q114, Q115, Q116, Q117, Q118, Q119, Q120, Q121, Q122, Q123, Q124, Q125, Q126, Q127, Q128, Q129, Q130, Q131, Q132, Q133, Q134, Q135, Q136, Q137, Q138, Q139]), "operationType" : NewBodyOperationType.REMOVE, "endBound" : BoundingType.UP_TO_SURFACE, "oppositeDirection" : true, "depth" : 25 * mm, "endBoundEntityFace" : qUnion([Q140]), "offsetDistance" : 25 * mm});
        }
        {
            var Q0;
            Q0=makeQuery(id+"F3.opSweep","SWEPT_FACE",FACE,{"disambiguationData":[OSD([sQuery(id+"F0.wireOp",EDGE,"E0.bottom"),sQuery(id+"F2.wireOp",EDGE,"E6.left")])]});
            var sketch = newSketch(context, id + "F6", { "sketchPlane" : qUnion([Q0])});
            skLineSegment(sketch, "E21.0", {"start": v(-91.34, 17.8) * mm, "end": v(88.66, 17.8) * mm});
            skLineSegment(sketch, "E22.0", {"start": v(-87.5, 20.3) * mm, "end": v(-87.5, 0.3) * mm});
            skLineSegment(sketch, "E23.0", {"start": v(-90, 2.8) * mm, "end": v(90, 2.8) * mm});
            skLineSegment(sketch, "E24.0", {"start": v(87.5, 20.3) * mm, "end": v(87.5, 0.3) * mm});
            skCircle(sketch, "E25.cCircle", {"center": v(-79.74, 19.67) * mm, "radius": 2.5 * mm, "construction": true});
            skLineSegment(sketch, "E25.0", {"start": v(-78.3, 17.17) * mm, "end": v(-81.18, 17.17) * mm});
            skLineSegment(sketch, "E25.1", {"start": v(-81.18, 17.17) * mm, "end": v(-82.63, 19.67) * mm});
            skLineSegment(sketch, "E25.2", {"start": v(-82.63, 19.67) * mm, "end": v(-81.18, 22.17) * mm});
            skLineSegment(sketch, "E25.3", {"start": v(-81.18, 22.17) * mm, "end": v(-78.3, 22.17) * mm});
            skLineSegment(sketch, "E25.4", {"start": v(-78.3, 22.17) * mm, "end": v(-76.85, 19.67) * mm});
            skLineSegment(sketch, "E25.5", {"start": v(-76.85, 19.67) * mm, "end": v(-78.3, 17.17) * mm});
            skPoint(sketch, "E25.0.midPoint", {"position": v(-79.74, 17.17) * mm});
            skCircle(sketch, "E26.cCircle", {"center": v(-85.15, 16.54) * mm, "radius": 2.5 * mm, "construction": true});
            skLineSegment(sketch, "E26.0", {"start": v(-83.71, 14.04) * mm, "end": v(-86.6, 14.04) * mm});
            skLineSegment(sketch, "E26.1", {"start": v(-86.6, 14.04) * mm, "end": v(-88.04, 16.54) * mm});
            skLineSegment(sketch, "E26.2", {"start": v(-88.04, 16.54) * mm, "end": v(-86.6, 19.04) * mm});
            skLineSegment(sketch, "E26.3", {"start": v(-86.6, 19.04) * mm, "end": v(-83.71, 19.04) * mm});
            skLineSegment(sketch, "E26.4", {"start": v(-83.71, 19.04) * mm, "end": v(-82.27, 16.54) * mm});
            skLineSegment(sketch, "E26.5", {"start": v(-82.27, 16.54) * mm, "end": v(-83.71, 14.04) * mm});
            skPoint(sketch, "E26.0.midPoint", {"position": v(-85.15, 14.04) * mm});
            skLineSegment(sketch, "E27.0.1.0", {"start": v(-86.6, 12.8) * mm, "end": v(-83.71, 12.8) * mm});
            skLineSegment(sketch, "E27.0.1.1", {"start": v(-88.04, 10.3) * mm, "end": v(-86.6, 12.8) * mm});
            skLineSegment(sketch, "E27.0.1.2", {"start": v(-86.6, 7.8) * mm, "end": v(-88.04, 10.3) * mm});
            skLineSegment(sketch, "E27.0.1.3", {"start": v(-83.71, 7.8) * mm, "end": v(-86.6, 7.8) * mm});
            skLineSegment(sketch, "E27.0.1.4", {"start": v(-82.27, 10.3) * mm, "end": v(-83.71, 7.8) * mm});
            skLineSegment(sketch, "E27.0.1.5", {"start": v(-83.71, 12.8) * mm, "end": v(-82.27, 10.3) * mm});
            skLineSegment(sketch, "E27.0.1.6", {"start": v(-81.18, 10.92) * mm, "end": v(-82.63, 13.42) * mm});
            skLineSegment(sketch, "E27.0.1.7", {"start": v(-82.63, 13.42) * mm, "end": v(-81.18, 15.92) * mm});
            skLineSegment(sketch, "E27.0.1.8", {"start": v(-81.18, 15.92) * mm, "end": v(-78.3, 15.92) * mm});
            skLineSegment(sketch, "E27.0.1.9", {"start": v(-78.3, 15.92) * mm, "end": v(-76.85, 13.42) * mm});
            skLineSegment(sketch, "E27.0.1.10", {"start": v(-76.85, 13.42) * mm, "end": v(-78.3, 10.92) * mm});
            skLineSegment(sketch, "E27.0.1.11", {"start": v(-78.3, 10.92) * mm, "end": v(-81.18, 10.92) * mm});
            skLineSegment(sketch, "E27.1.0.0", {"start": v(-75.6, 19.04) * mm, "end": v(-72.72, 19.04) * mm});
            skLineSegment(sketch, "E27.1.0.1", {"start": v(-77.05, 16.54) * mm, "end": v(-75.6, 19.04) * mm});
            skLineSegment(sketch, "E27.1.0.2", {"start": v(-75.6, 14.04) * mm, "end": v(-77.05, 16.54) * mm});
            skLineSegment(sketch, "E27.1.0.3", {"start": v(-72.72, 14.04) * mm, "end": v(-75.6, 14.04) * mm});
            skLineSegment(sketch, "E27.1.0.4", {"start": v(-71.27, 16.54) * mm, "end": v(-72.72, 14.04) * mm});
            skLineSegment(sketch, "E27.1.0.5", {"start": v(-72.72, 19.04) * mm, "end": v(-71.27, 16.54) * mm});
            skLineSegment(sketch, "E27.1.0.6", {"start": v(-70.2, 17.17) * mm, "end": v(-71.63, 19.67) * mm});
            skLineSegment(sketch, "E27.1.0.7", {"start": v(-71.63, 19.67) * mm, "end": v(-70.2, 22.17) * mm});
            skLineSegment(sketch, "E27.1.0.8", {"start": v(-70.2, 22.17) * mm, "end": v(-67.3, 22.17) * mm});
            skLineSegment(sketch, "E27.1.0.9", {"start": v(-67.3, 22.17) * mm, "end": v(-65.86, 19.67) * mm});
            skLineSegment(sketch, "E27.1.0.10", {"start": v(-65.86, 19.67) * mm, "end": v(-67.3, 17.17) * mm});
            skLineSegment(sketch, "E27.1.0.11", {"start": v(-67.3, 17.17) * mm, "end": v(-70.2, 17.17) * mm});
            skLineSegment(sketch, "E27.1.1.0", {"start": v(-75.6, 12.8) * mm, "end": v(-72.72, 12.8) * mm});
            skLineSegment(sketch, "E27.1.1.1", {"start": v(-77.05, 10.3) * mm, "end": v(-75.6, 12.8) * mm});
            skLineSegment(sketch, "E27.1.1.2", {"start": v(-75.6, 7.8) * mm, "end": v(-77.05, 10.3) * mm});
            skLineSegment(sketch, "E27.1.1.3", {"start": v(-72.72, 7.8) * mm, "end": v(-75.6, 7.8) * mm});
            skLineSegment(sketch, "E27.1.1.4", {"start": v(-71.27, 10.3) * mm, "end": v(-72.72, 7.8) * mm});
            skLineSegment(sketch, "E27.1.1.5", {"start": v(-72.72, 12.8) * mm, "end": v(-71.27, 10.3) * mm});
            skLineSegment(sketch, "E27.1.1.6", {"start": v(-70.2, 10.92) * mm, "end": v(-71.63, 13.42) * mm});
            skLineSegment(sketch, "E27.1.1.7", {"start": v(-71.63, 13.42) * mm, "end": v(-70.2, 15.92) * mm});
            skLineSegment(sketch, "E27.1.1.8", {"start": v(-70.2, 15.92) * mm, "end": v(-67.3, 15.92) * mm});
            skLineSegment(sketch, "E27.1.1.9", {"start": v(-67.3, 15.92) * mm, "end": v(-65.86, 13.42) * mm});
            skLineSegment(sketch, "E27.1.1.10", {"start": v(-65.86, 13.42) * mm, "end": v(-67.3, 10.92) * mm});
            skLineSegment(sketch, "E27.1.1.11", {"start": v(-67.3, 10.92) * mm, "end": v(-70.2, 10.92) * mm});
            skLineSegment(sketch, "E27.2.0.0", {"start": v(-64.61, 19.04) * mm, "end": v(-61.72, 19.04) * mm});
            skLineSegment(sketch, "E27.2.0.1", {"start": v(-66.05, 16.54) * mm, "end": v(-64.61, 19.04) * mm});
            skLineSegment(sketch, "E27.2.0.2", {"start": v(-64.61, 14.04) * mm, "end": v(-66.05, 16.54) * mm});
            skLineSegment(sketch, "E27.2.0.3", {"start": v(-61.72, 14.04) * mm, "end": v(-64.61, 14.04) * mm});
            skLineSegment(sketch, "E27.2.0.4", {"start": v(-60.28, 16.54) * mm, "end": v(-61.72, 14.04) * mm});
            skLineSegment(sketch, "E27.2.0.5", {"start": v(-61.72, 19.04) * mm, "end": v(-60.28, 16.54) * mm});
            skLineSegment(sketch, "E27.2.0.6", {"start": v(-59.2, 17.17) * mm, "end": v(-60.64, 19.67) * mm});
            skLineSegment(sketch, "E27.2.0.7", {"start": v(-60.64, 19.67) * mm, "end": v(-59.2, 22.17) * mm});
            skLineSegment(sketch, "E27.2.0.8", {"start": v(-59.2, 22.17) * mm, "end": v(-56.31, 22.17) * mm});
            skLineSegment(sketch, "E27.2.0.9", {"start": v(-56.31, 22.17) * mm, "end": v(-54.87, 19.67) * mm});
            skLineSegment(sketch, "E27.2.0.10", {"start": v(-54.87, 19.67) * mm, "end": v(-56.31, 17.17) * mm});
            skLineSegment(sketch, "E27.2.0.11", {"start": v(-56.31, 17.17) * mm, "end": v(-59.2, 17.17) * mm});
            skLineSegment(sketch, "E27.2.1.0", {"start": v(-64.61, 12.8) * mm, "end": v(-61.72, 12.8) * mm});
            skLineSegment(sketch, "E27.2.1.1", {"start": v(-66.05, 10.3) * mm, "end": v(-64.61, 12.8) * mm});
            skLineSegment(sketch, "E27.2.1.2", {"start": v(-64.61, 7.8) * mm, "end": v(-66.05, 10.3) * mm});
            skLineSegment(sketch, "E27.2.1.3", {"start": v(-61.72, 7.8) * mm, "end": v(-64.61, 7.8) * mm});
            skLineSegment(sketch, "E27.2.1.4", {"start": v(-60.28, 10.3) * mm, "end": v(-61.72, 7.8) * mm});
            skLineSegment(sketch, "E27.2.1.5", {"start": v(-61.72, 12.8) * mm, "end": v(-60.28, 10.3) * mm});
            skLineSegment(sketch, "E27.2.1.6", {"start": v(-59.2, 10.92) * mm, "end": v(-60.64, 13.42) * mm});
            skLineSegment(sketch, "E27.2.1.7", {"start": v(-60.64, 13.42) * mm, "end": v(-59.2, 15.92) * mm});
            skLineSegment(sketch, "E27.2.1.8", {"start": v(-59.2, 15.92) * mm, "end": v(-56.31, 15.92) * mm});
            skLineSegment(sketch, "E27.2.1.9", {"start": v(-56.31, 15.92) * mm, "end": v(-54.87, 13.42) * mm});
            skLineSegment(sketch, "E27.2.1.10", {"start": v(-54.87, 13.42) * mm, "end": v(-56.31, 10.92) * mm});
            skLineSegment(sketch, "E27.2.1.11", {"start": v(-56.31, 10.92) * mm, "end": v(-59.2, 10.92) * mm});
            skLineSegment(sketch, "E27.direction1", {"start": v(-86.6, 19.04) * mm, "end": v(-75.6, 19.04) * mm, "construction": true});
            skLineSegment(sketch, "E27.direction2", {"start": v(-86.6, 19.04) * mm, "end": v(-86.6, 12.8) * mm, "construction": true});
            skLineSegment(sketch, "E28.0.0.2", {"start": v(-86.6, 6.54) * mm, "end": v(-83.71, 6.54) * mm});
            skLineSegment(sketch, "E28.3.0.2", {"start": v(-88.04, 4.04) * mm, "end": v(-86.6, 6.54) * mm});
            skLineSegment(sketch, "E28.6.0.2", {"start": v(-86.6, 1.54) * mm, "end": v(-88.04, 4.04) * mm});
            skLineSegment(sketch, "E28.9.0.2", {"start": v(-83.71, 1.54) * mm, "end": v(-86.6, 1.54) * mm});
            skLineSegment(sketch, "E28.12.0.2", {"start": v(-82.27, 4.04) * mm, "end": v(-83.71, 1.54) * mm});
            skLineSegment(sketch, "E28.15.0.2", {"start": v(-83.71, 6.54) * mm, "end": v(-82.27, 4.04) * mm});
            skLineSegment(sketch, "E28.18.0.2", {"start": v(-81.18, 4.67) * mm, "end": v(-82.63, 7.17) * mm});
            skLineSegment(sketch, "E28.21.0.2", {"start": v(-82.63, 7.17) * mm, "end": v(-81.18, 9.67) * mm});
            skLineSegment(sketch, "E28.24.0.2", {"start": v(-81.18, 9.67) * mm, "end": v(-78.3, 9.67) * mm});
            skLineSegment(sketch, "E28.27.0.2", {"start": v(-78.3, 9.67) * mm, "end": v(-76.85, 7.17) * mm});
            skLineSegment(sketch, "E28.30.0.2", {"start": v(-76.85, 7.17) * mm, "end": v(-78.3, 4.67) * mm});
            skLineSegment(sketch, "E28.33.0.2", {"start": v(-78.3, 4.67) * mm, "end": v(-81.18, 4.67) * mm});
            skLineSegment(sketch, "E28.0.1.2", {"start": v(-75.6, 6.54) * mm, "end": v(-72.72, 6.54) * mm});
            skLineSegment(sketch, "E28.3.1.2", {"start": v(-77.05, 4.04) * mm, "end": v(-75.6, 6.54) * mm});
            skLineSegment(sketch, "E28.6.1.2", {"start": v(-75.6, 1.54) * mm, "end": v(-77.05, 4.04) * mm});
            skLineSegment(sketch, "E28.9.1.2", {"start": v(-72.72, 1.54) * mm, "end": v(-75.6, 1.54) * mm});
            skLineSegment(sketch, "E28.12.1.2", {"start": v(-71.27, 4.04) * mm, "end": v(-72.72, 1.54) * mm});
            skLineSegment(sketch, "E28.15.1.2", {"start": v(-72.72, 6.54) * mm, "end": v(-71.27, 4.04) * mm});
            skLineSegment(sketch, "E28.18.1.2", {"start": v(-70.2, 4.67) * mm, "end": v(-71.63, 7.17) * mm});
            skLineSegment(sketch, "E28.21.1.2", {"start": v(-71.63, 7.17) * mm, "end": v(-70.2, 9.67) * mm});
            skLineSegment(sketch, "E28.24.1.2", {"start": v(-70.2, 9.67) * mm, "end": v(-67.3, 9.67) * mm});
            skLineSegment(sketch, "E28.27.1.2", {"start": v(-67.3, 9.67) * mm, "end": v(-65.86, 7.17) * mm});
            skLineSegment(sketch, "E28.30.1.2", {"start": v(-65.86, 7.17) * mm, "end": v(-67.3, 4.67) * mm});
            skLineSegment(sketch, "E28.33.1.2", {"start": v(-67.3, 4.67) * mm, "end": v(-70.2, 4.67) * mm});
            skLineSegment(sketch, "E28.0.2.2", {"start": v(-64.61, 6.54) * mm, "end": v(-61.72, 6.54) * mm});
            skLineSegment(sketch, "E28.3.2.2", {"start": v(-66.05, 4.04) * mm, "end": v(-64.61, 6.54) * mm});
            skLineSegment(sketch, "E28.6.2.2", {"start": v(-64.61, 1.54) * mm, "end": v(-66.05, 4.04) * mm});
            skLineSegment(sketch, "E28.9.2.2", {"start": v(-61.72, 1.54) * mm, "end": v(-64.61, 1.54) * mm});
            skLineSegment(sketch, "E28.12.2.2", {"start": v(-60.28, 4.04) * mm, "end": v(-61.72, 1.54) * mm});
            skLineSegment(sketch, "E28.15.2.2", {"start": v(-61.72, 6.54) * mm, "end": v(-60.28, 4.04) * mm});
            skLineSegment(sketch, "E28.18.2.2", {"start": v(-59.2, 4.67) * mm, "end": v(-60.64, 7.17) * mm});
            skLineSegment(sketch, "E28.21.2.2", {"start": v(-60.64, 7.17) * mm, "end": v(-59.2, 9.67) * mm});
            skLineSegment(sketch, "E28.24.2.2", {"start": v(-59.2, 9.67) * mm, "end": v(-56.31, 9.67) * mm});
            skLineSegment(sketch, "E28.27.2.2", {"start": v(-56.31, 9.67) * mm, "end": v(-54.87, 7.17) * mm});
            skLineSegment(sketch, "E28.30.2.2", {"start": v(-54.87, 7.17) * mm, "end": v(-56.31, 4.67) * mm});
            skLineSegment(sketch, "E28.33.2.2", {"start": v(-56.31, 4.67) * mm, "end": v(-59.2, 4.67) * mm});
            skLineSegment(sketch, "E29.0.0.3", {"start": v(-86.6, 0.3) * mm, "end": v(-83.71, 0.3) * mm});
            skLineSegment(sketch, "E29.3.0.3", {"start": v(-88.04, -2.2) * mm, "end": v(-86.6, 0.3) * mm});
            skLineSegment(sketch, "E29.6.0.3", {"start": v(-86.6, -4.7) * mm, "end": v(-88.04, -2.2) * mm});
            skLineSegment(sketch, "E29.9.0.3", {"start": v(-83.71, -4.7) * mm, "end": v(-86.6, -4.7) * mm});
            skLineSegment(sketch, "E29.12.0.3", {"start": v(-82.27, -2.2) * mm, "end": v(-83.71, -4.7) * mm});
            skLineSegment(sketch, "E29.15.0.3", {"start": v(-83.71, 0.3) * mm, "end": v(-82.27, -2.2) * mm});
            skLineSegment(sketch, "E29.18.0.3", {"start": v(-81.18, -1.58) * mm, "end": v(-82.63, 0.92) * mm});
            skLineSegment(sketch, "E29.21.0.3", {"start": v(-82.63, 0.92) * mm, "end": v(-81.18, 3.42) * mm});
            skLineSegment(sketch, "E29.24.0.3", {"start": v(-81.18, 3.42) * mm, "end": v(-78.3, 3.42) * mm});
            skLineSegment(sketch, "E29.27.0.3", {"start": v(-78.3, 3.42) * mm, "end": v(-76.85, 0.92) * mm});
            skLineSegment(sketch, "E29.30.0.3", {"start": v(-76.85, 0.92) * mm, "end": v(-78.3, -1.58) * mm});
            skLineSegment(sketch, "E29.33.0.3", {"start": v(-78.3, -1.58) * mm, "end": v(-81.18, -1.58) * mm});
            skLineSegment(sketch, "E29.0.1.3", {"start": v(-75.6, 0.3) * mm, "end": v(-72.72, 0.3) * mm});
            skLineSegment(sketch, "E29.3.1.3", {"start": v(-77.05, -2.2) * mm, "end": v(-75.6, 0.3) * mm});
            skLineSegment(sketch, "E29.6.1.3", {"start": v(-75.6, -4.7) * mm, "end": v(-77.05, -2.2) * mm});
            skLineSegment(sketch, "E29.9.1.3", {"start": v(-72.72, -4.7) * mm, "end": v(-75.6, -4.7) * mm});
            skLineSegment(sketch, "E29.12.1.3", {"start": v(-71.27, -2.2) * mm, "end": v(-72.72, -4.7) * mm});
            skLineSegment(sketch, "E29.15.1.3", {"start": v(-72.72, 0.3) * mm, "end": v(-71.27, -2.2) * mm});
            skLineSegment(sketch, "E29.18.1.3", {"start": v(-70.2, -1.58) * mm, "end": v(-71.63, 0.92) * mm});
            skLineSegment(sketch, "E29.21.1.3", {"start": v(-71.63, 0.92) * mm, "end": v(-70.2, 3.42) * mm});
            skLineSegment(sketch, "E29.24.1.3", {"start": v(-70.2, 3.42) * mm, "end": v(-67.3, 3.42) * mm});
            skLineSegment(sketch, "E29.27.1.3", {"start": v(-67.3, 3.42) * mm, "end": v(-65.86, 0.92) * mm});
            skLineSegment(sketch, "E29.30.1.3", {"start": v(-65.86, 0.92) * mm, "end": v(-67.3, -1.58) * mm});
            skLineSegment(sketch, "E29.33.1.3", {"start": v(-67.3, -1.58) * mm, "end": v(-70.2, -1.58) * mm});
            skLineSegment(sketch, "E29.0.2.3", {"start": v(-64.61, 0.3) * mm, "end": v(-61.72, 0.3) * mm});
            skLineSegment(sketch, "E29.3.2.3", {"start": v(-66.05, -2.2) * mm, "end": v(-64.61, 0.3) * mm});
            skLineSegment(sketch, "E29.6.2.3", {"start": v(-64.61, -4.7) * mm, "end": v(-66.05, -2.2) * mm});
            skLineSegment(sketch, "E29.9.2.3", {"start": v(-61.72, -4.7) * mm, "end": v(-64.61, -4.7) * mm});
            skLineSegment(sketch, "E29.12.2.3", {"start": v(-60.28, -2.2) * mm, "end": v(-61.72, -4.7) * mm});
            skLineSegment(sketch, "E29.15.2.3", {"start": v(-61.72, 0.3) * mm, "end": v(-60.28, -2.2) * mm});
            skLineSegment(sketch, "E29.18.2.3", {"start": v(-59.2, -1.58) * mm, "end": v(-60.64, 0.92) * mm});
            skLineSegment(sketch, "E29.21.2.3", {"start": v(-60.64, 0.92) * mm, "end": v(-59.2, 3.42) * mm});
            skLineSegment(sketch, "E29.24.2.3", {"start": v(-59.2, 3.42) * mm, "end": v(-56.31, 3.42) * mm});
            skLineSegment(sketch, "E29.27.2.3", {"start": v(-56.31, 3.42) * mm, "end": v(-54.87, 0.92) * mm});
            skLineSegment(sketch, "E29.30.2.3", {"start": v(-54.87, 0.92) * mm, "end": v(-56.31, -1.58) * mm});
            skLineSegment(sketch, "E29.33.2.3", {"start": v(-56.31, -1.58) * mm, "end": v(-59.2, -1.58) * mm});
            skLineSegment(sketch, "E30.0.3.0", {"start": v(-53.62, 19.04) * mm, "end": v(-50.73, 19.04) * mm});
            skLineSegment(sketch, "E30.3.3.0", {"start": v(-55.06, 16.54) * mm, "end": v(-53.62, 19.04) * mm});
            skLineSegment(sketch, "E30.6.3.0", {"start": v(-53.62, 14.04) * mm, "end": v(-55.06, 16.54) * mm});
            skLineSegment(sketch, "E30.9.3.0", {"start": v(-50.73, 14.04) * mm, "end": v(-53.62, 14.04) * mm});
            skLineSegment(sketch, "E30.12.3.0", {"start": v(-49.29, 16.54) * mm, "end": v(-50.73, 14.04) * mm});
            skLineSegment(sketch, "E30.15.3.0", {"start": v(-50.73, 19.04) * mm, "end": v(-49.29, 16.54) * mm});
            skLineSegment(sketch, "E30.18.3.0", {"start": v(-48.2, 17.17) * mm, "end": v(-49.65, 19.67) * mm});
            skLineSegment(sketch, "E30.21.3.0", {"start": v(-49.65, 19.67) * mm, "end": v(-48.2, 22.17) * mm});
            skLineSegment(sketch, "E30.24.3.0", {"start": v(-48.2, 22.17) * mm, "end": v(-45.32, 22.17) * mm});
            skLineSegment(sketch, "E30.27.3.0", {"start": v(-45.32, 22.17) * mm, "end": v(-43.88, 19.67) * mm});
            skLineSegment(sketch, "E30.30.3.0", {"start": v(-43.88, 19.67) * mm, "end": v(-45.32, 17.17) * mm});
            skLineSegment(sketch, "E30.33.3.0", {"start": v(-45.32, 17.17) * mm, "end": v(-48.2, 17.17) * mm});
            skLineSegment(sketch, "E30.0.3.1", {"start": v(-53.62, 12.8) * mm, "end": v(-50.73, 12.8) * mm});
            skLineSegment(sketch, "E30.3.3.1", {"start": v(-55.06, 10.3) * mm, "end": v(-53.62, 12.8) * mm});
            skLineSegment(sketch, "E30.6.3.1", {"start": v(-53.62, 7.8) * mm, "end": v(-55.06, 10.3) * mm});
            skLineSegment(sketch, "E30.9.3.1", {"start": v(-50.73, 7.8) * mm, "end": v(-53.62, 7.8) * mm});
            skLineSegment(sketch, "E30.12.3.1", {"start": v(-49.29, 10.3) * mm, "end": v(-50.73, 7.8) * mm});
            skLineSegment(sketch, "E30.15.3.1", {"start": v(-50.73, 12.8) * mm, "end": v(-49.29, 10.3) * mm});
            skLineSegment(sketch, "E30.18.3.1", {"start": v(-48.2, 10.92) * mm, "end": v(-49.65, 13.42) * mm});
            skLineSegment(sketch, "E30.21.3.1", {"start": v(-49.65, 13.42) * mm, "end": v(-48.2, 15.92) * mm});
            skLineSegment(sketch, "E30.24.3.1", {"start": v(-48.2, 15.92) * mm, "end": v(-45.32, 15.92) * mm});
            skLineSegment(sketch, "E30.27.3.1", {"start": v(-45.32, 15.92) * mm, "end": v(-43.88, 13.42) * mm});
            skLineSegment(sketch, "E30.30.3.1", {"start": v(-43.88, 13.42) * mm, "end": v(-45.32, 10.92) * mm});
            skLineSegment(sketch, "E30.33.3.1", {"start": v(-45.32, 10.92) * mm, "end": v(-48.2, 10.92) * mm});
            skLineSegment(sketch, "E30.0.3.2", {"start": v(-53.62, 6.54) * mm, "end": v(-50.73, 6.54) * mm});
            skLineSegment(sketch, "E30.3.3.2", {"start": v(-55.06, 4.04) * mm, "end": v(-53.62, 6.54) * mm});
            skLineSegment(sketch, "E30.6.3.2", {"start": v(-53.62, 1.54) * mm, "end": v(-55.06, 4.04) * mm});
            skLineSegment(sketch, "E30.9.3.2", {"start": v(-50.73, 1.54) * mm, "end": v(-53.62, 1.54) * mm});
            skLineSegment(sketch, "E30.12.3.2", {"start": v(-49.29, 4.04) * mm, "end": v(-50.73, 1.54) * mm});
            skLineSegment(sketch, "E30.15.3.2", {"start": v(-50.73, 6.54) * mm, "end": v(-49.29, 4.04) * mm});
            skLineSegment(sketch, "E30.18.3.2", {"start": v(-48.2, 4.67) * mm, "end": v(-49.65, 7.17) * mm});
            skLineSegment(sketch, "E30.21.3.2", {"start": v(-49.65, 7.17) * mm, "end": v(-48.2, 9.67) * mm});
            skLineSegment(sketch, "E30.24.3.2", {"start": v(-48.2, 9.67) * mm, "end": v(-45.32, 9.67) * mm});
            skLineSegment(sketch, "E30.27.3.2", {"start": v(-45.32, 9.67) * mm, "end": v(-43.88, 7.17) * mm});
            skLineSegment(sketch, "E30.30.3.2", {"start": v(-43.88, 7.17) * mm, "end": v(-45.32, 4.67) * mm});
            skLineSegment(sketch, "E30.33.3.2", {"start": v(-45.32, 4.67) * mm, "end": v(-48.2, 4.67) * mm});
            skLineSegment(sketch, "E30.0.3.3", {"start": v(-53.62, 0.3) * mm, "end": v(-50.73, 0.3) * mm});
            skLineSegment(sketch, "E30.3.3.3", {"start": v(-55.06, -2.2) * mm, "end": v(-53.62, 0.3) * mm});
            skLineSegment(sketch, "E30.6.3.3", {"start": v(-53.62, -4.7) * mm, "end": v(-55.06, -2.2) * mm});
            skLineSegment(sketch, "E30.9.3.3", {"start": v(-50.73, -4.7) * mm, "end": v(-53.62, -4.7) * mm});
            skLineSegment(sketch, "E30.12.3.3", {"start": v(-49.29, -2.2) * mm, "end": v(-50.73, -4.7) * mm});
            skLineSegment(sketch, "E30.15.3.3", {"start": v(-50.73, 0.3) * mm, "end": v(-49.29, -2.2) * mm});
            skLineSegment(sketch, "E30.18.3.3", {"start": v(-48.2, -1.58) * mm, "end": v(-49.65, 0.92) * mm});
            skLineSegment(sketch, "E30.21.3.3", {"start": v(-49.65, 0.92) * mm, "end": v(-48.2, 3.42) * mm});
            skLineSegment(sketch, "E30.24.3.3", {"start": v(-48.2, 3.42) * mm, "end": v(-45.32, 3.42) * mm});
            skLineSegment(sketch, "E30.27.3.3", {"start": v(-45.32, 3.42) * mm, "end": v(-43.88, 0.92) * mm});
            skLineSegment(sketch, "E30.30.3.3", {"start": v(-43.88, 0.92) * mm, "end": v(-45.32, -1.58) * mm});
            skLineSegment(sketch, "E30.33.3.3", {"start": v(-45.32, -1.58) * mm, "end": v(-48.2, -1.58) * mm});
            skLineSegment(sketch, "E30.0.4.0", {"start": v(-42.63, 19.04) * mm, "end": v(-39.74, 19.04) * mm});
            skLineSegment(sketch, "E30.3.4.0", {"start": v(-44.07, 16.54) * mm, "end": v(-42.63, 19.04) * mm});
            skLineSegment(sketch, "E30.6.4.0", {"start": v(-42.63, 14.04) * mm, "end": v(-44.07, 16.54) * mm});
            skLineSegment(sketch, "E30.9.4.0", {"start": v(-39.74, 14.04) * mm, "end": v(-42.63, 14.04) * mm});
            skLineSegment(sketch, "E30.12.4.0", {"start": v(-38.3, 16.54) * mm, "end": v(-39.74, 14.04) * mm});
            skLineSegment(sketch, "E30.15.4.0", {"start": v(-39.74, 19.04) * mm, "end": v(-38.3, 16.54) * mm});
            skLineSegment(sketch, "E30.18.4.0", {"start": v(-37.21, 17.17) * mm, "end": v(-38.66, 19.67) * mm});
            skLineSegment(sketch, "E30.21.4.0", {"start": v(-38.66, 19.67) * mm, "end": v(-37.21, 22.17) * mm});
            skLineSegment(sketch, "E30.24.4.0", {"start": v(-37.21, 22.17) * mm, "end": v(-34.33, 22.17) * mm});
            skLineSegment(sketch, "E30.27.4.0", {"start": v(-34.33, 22.17) * mm, "end": v(-32.88, 19.67) * mm});
            skLineSegment(sketch, "E30.30.4.0", {"start": v(-32.88, 19.67) * mm, "end": v(-34.33, 17.17) * mm});
            skLineSegment(sketch, "E30.33.4.0", {"start": v(-34.33, 17.17) * mm, "end": v(-37.21, 17.17) * mm});
            skLineSegment(sketch, "E30.0.4.1", {"start": v(-42.63, 12.8) * mm, "end": v(-39.74, 12.8) * mm});
            skLineSegment(sketch, "E30.3.4.1", {"start": v(-44.07, 10.3) * mm, "end": v(-42.63, 12.8) * mm});
            skLineSegment(sketch, "E30.6.4.1", {"start": v(-42.63, 7.8) * mm, "end": v(-44.07, 10.3) * mm});
            skLineSegment(sketch, "E30.9.4.1", {"start": v(-39.74, 7.8) * mm, "end": v(-42.63, 7.8) * mm});
            skLineSegment(sketch, "E30.12.4.1", {"start": v(-38.3, 10.3) * mm, "end": v(-39.74, 7.8) * mm});
            skLineSegment(sketch, "E30.15.4.1", {"start": v(-39.74, 12.8) * mm, "end": v(-38.3, 10.3) * mm});
            skLineSegment(sketch, "E30.18.4.1", {"start": v(-37.21, 10.92) * mm, "end": v(-38.66, 13.42) * mm});
            skLineSegment(sketch, "E30.21.4.1", {"start": v(-38.66, 13.42) * mm, "end": v(-37.21, 15.92) * mm});
            skLineSegment(sketch, "E30.24.4.1", {"start": v(-37.21, 15.92) * mm, "end": v(-34.33, 15.92) * mm});
            skLineSegment(sketch, "E30.27.4.1", {"start": v(-34.33, 15.92) * mm, "end": v(-32.88, 13.42) * mm});
            skLineSegment(sketch, "E30.30.4.1", {"start": v(-32.88, 13.42) * mm, "end": v(-34.33, 10.92) * mm});
            skLineSegment(sketch, "E30.33.4.1", {"start": v(-34.33, 10.92) * mm, "end": v(-37.21, 10.92) * mm});
            skLineSegment(sketch, "E30.0.4.2", {"start": v(-42.63, 6.54) * mm, "end": v(-39.74, 6.54) * mm});
            skLineSegment(sketch, "E30.3.4.2", {"start": v(-44.07, 4.04) * mm, "end": v(-42.63, 6.54) * mm});
            skLineSegment(sketch, "E30.6.4.2", {"start": v(-42.63, 1.54) * mm, "end": v(-44.07, 4.04) * mm});
            skLineSegment(sketch, "E30.9.4.2", {"start": v(-39.74, 1.54) * mm, "end": v(-42.63, 1.54) * mm});
            skLineSegment(sketch, "E30.12.4.2", {"start": v(-38.3, 4.04) * mm, "end": v(-39.74, 1.54) * mm});
            skLineSegment(sketch, "E30.15.4.2", {"start": v(-39.74, 6.54) * mm, "end": v(-38.3, 4.04) * mm});
            skLineSegment(sketch, "E30.18.4.2", {"start": v(-37.21, 4.67) * mm, "end": v(-38.66, 7.17) * mm});
            skLineSegment(sketch, "E30.21.4.2", {"start": v(-38.66, 7.17) * mm, "end": v(-37.21, 9.67) * mm});
            skLineSegment(sketch, "E30.24.4.2", {"start": v(-37.21, 9.67) * mm, "end": v(-34.33, 9.67) * mm});
            skLineSegment(sketch, "E30.27.4.2", {"start": v(-34.33, 9.67) * mm, "end": v(-32.88, 7.17) * mm});
            skLineSegment(sketch, "E30.30.4.2", {"start": v(-32.88, 7.17) * mm, "end": v(-34.33, 4.67) * mm});
            skLineSegment(sketch, "E30.33.4.2", {"start": v(-34.33, 4.67) * mm, "end": v(-37.21, 4.67) * mm});
            skLineSegment(sketch, "E30.0.4.3", {"start": v(-42.63, 0.3) * mm, "end": v(-39.74, 0.3) * mm});
            skLineSegment(sketch, "E30.3.4.3", {"start": v(-44.07, -2.2) * mm, "end": v(-42.63, 0.3) * mm});
            skLineSegment(sketch, "E30.6.4.3", {"start": v(-42.63, -4.7) * mm, "end": v(-44.07, -2.2) * mm});
            skLineSegment(sketch, "E30.9.4.3", {"start": v(-39.74, -4.7) * mm, "end": v(-42.63, -4.7) * mm});
            skLineSegment(sketch, "E30.12.4.3", {"start": v(-38.3, -2.2) * mm, "end": v(-39.74, -4.7) * mm});
            skLineSegment(sketch, "E30.15.4.3", {"start": v(-39.74, 0.3) * mm, "end": v(-38.3, -2.2) * mm});
            skLineSegment(sketch, "E30.18.4.3", {"start": v(-37.21, -1.58) * mm, "end": v(-38.66, 0.92) * mm});
            skLineSegment(sketch, "E30.21.4.3", {"start": v(-38.66, 0.92) * mm, "end": v(-37.21, 3.42) * mm});
            skLineSegment(sketch, "E30.24.4.3", {"start": v(-37.21, 3.42) * mm, "end": v(-34.33, 3.42) * mm});
            skLineSegment(sketch, "E30.27.4.3", {"start": v(-34.33, 3.42) * mm, "end": v(-32.88, 0.92) * mm});
            skLineSegment(sketch, "E30.30.4.3", {"start": v(-32.88, 0.92) * mm, "end": v(-34.33, -1.58) * mm});
            skLineSegment(sketch, "E30.33.4.3", {"start": v(-34.33, -1.58) * mm, "end": v(-37.21, -1.58) * mm});
            skLineSegment(sketch, "E30.0.5.0", {"start": v(-31.63, 19.04) * mm, "end": v(-28.75, 19.04) * mm});
            skLineSegment(sketch, "E30.3.5.0", {"start": v(-33.08, 16.54) * mm, "end": v(-31.63, 19.04) * mm});
            skLineSegment(sketch, "E30.6.5.0", {"start": v(-31.63, 14.04) * mm, "end": v(-33.08, 16.54) * mm});
            skLineSegment(sketch, "E30.9.5.0", {"start": v(-28.75, 14.04) * mm, "end": v(-31.63, 14.04) * mm});
            skLineSegment(sketch, "E30.12.5.0", {"start": v(-27.3, 16.54) * mm, "end": v(-28.75, 14.04) * mm});
            skLineSegment(sketch, "E30.15.5.0", {"start": v(-28.75, 19.04) * mm, "end": v(-27.3, 16.54) * mm});
            skLineSegment(sketch, "E30.18.5.0", {"start": v(-26.22, 17.17) * mm, "end": v(-27.66, 19.67) * mm});
            skLineSegment(sketch, "E30.21.5.0", {"start": v(-27.66, 19.67) * mm, "end": v(-26.22, 22.17) * mm});
            skLineSegment(sketch, "E30.24.5.0", {"start": v(-26.22, 22.17) * mm, "end": v(-23.33, 22.17) * mm});
            skLineSegment(sketch, "E30.27.5.0", {"start": v(-23.33, 22.17) * mm, "end": v(-21.89, 19.67) * mm});
            skLineSegment(sketch, "E30.30.5.0", {"start": v(-21.89, 19.67) * mm, "end": v(-23.33, 17.17) * mm});
            skLineSegment(sketch, "E30.33.5.0", {"start": v(-23.33, 17.17) * mm, "end": v(-26.22, 17.17) * mm});
            skLineSegment(sketch, "E30.0.5.1", {"start": v(-31.63, 12.8) * mm, "end": v(-28.75, 12.8) * mm});
            skLineSegment(sketch, "E30.3.5.1", {"start": v(-33.08, 10.3) * mm, "end": v(-31.63, 12.8) * mm});
            skLineSegment(sketch, "E30.6.5.1", {"start": v(-31.63, 7.8) * mm, "end": v(-33.08, 10.3) * mm});
            skLineSegment(sketch, "E30.9.5.1", {"start": v(-28.75, 7.8) * mm, "end": v(-31.63, 7.8) * mm});
            skLineSegment(sketch, "E30.12.5.1", {"start": v(-27.3, 10.3) * mm, "end": v(-28.75, 7.8) * mm});
            skLineSegment(sketch, "E30.15.5.1", {"start": v(-28.75, 12.8) * mm, "end": v(-27.3, 10.3) * mm});
            skLineSegment(sketch, "E30.18.5.1", {"start": v(-26.22, 10.92) * mm, "end": v(-27.66, 13.42) * mm});
            skLineSegment(sketch, "E30.21.5.1", {"start": v(-27.66, 13.42) * mm, "end": v(-26.22, 15.92) * mm});
            skLineSegment(sketch, "E30.24.5.1", {"start": v(-26.22, 15.92) * mm, "end": v(-23.33, 15.92) * mm});
            skLineSegment(sketch, "E30.27.5.1", {"start": v(-23.33, 15.92) * mm, "end": v(-21.89, 13.42) * mm});
            skLineSegment(sketch, "E30.30.5.1", {"start": v(-21.89, 13.42) * mm, "end": v(-23.33, 10.92) * mm});
            skLineSegment(sketch, "E30.33.5.1", {"start": v(-23.33, 10.92) * mm, "end": v(-26.22, 10.92) * mm});
            skLineSegment(sketch, "E30.0.5.2", {"start": v(-31.63, 6.54) * mm, "end": v(-28.75, 6.54) * mm});
            skLineSegment(sketch, "E30.3.5.2", {"start": v(-33.08, 4.04) * mm, "end": v(-31.63, 6.54) * mm});
            skLineSegment(sketch, "E30.6.5.2", {"start": v(-31.63, 1.54) * mm, "end": v(-33.08, 4.04) * mm});
            skLineSegment(sketch, "E30.9.5.2", {"start": v(-28.75, 1.54) * mm, "end": v(-31.63, 1.54) * mm});
            skLineSegment(sketch, "E30.12.5.2", {"start": v(-27.3, 4.04) * mm, "end": v(-28.75, 1.54) * mm});
            skLineSegment(sketch, "E30.15.5.2", {"start": v(-28.75, 6.54) * mm, "end": v(-27.3, 4.04) * mm});
            skLineSegment(sketch, "E30.18.5.2", {"start": v(-26.22, 4.67) * mm, "end": v(-27.66, 7.17) * mm});
            skLineSegment(sketch, "E30.21.5.2", {"start": v(-27.66, 7.17) * mm, "end": v(-26.22, 9.67) * mm});
            skLineSegment(sketch, "E30.24.5.2", {"start": v(-26.22, 9.67) * mm, "end": v(-23.33, 9.67) * mm});
            skLineSegment(sketch, "E30.27.5.2", {"start": v(-23.33, 9.67) * mm, "end": v(-21.89, 7.17) * mm});
            skLineSegment(sketch, "E30.30.5.2", {"start": v(-21.89, 7.17) * mm, "end": v(-23.33, 4.67) * mm});
            skLineSegment(sketch, "E30.33.5.2", {"start": v(-23.33, 4.67) * mm, "end": v(-26.22, 4.67) * mm});
            skLineSegment(sketch, "E30.0.5.3", {"start": v(-31.63, 0.3) * mm, "end": v(-28.75, 0.3) * mm});
            skLineSegment(sketch, "E30.3.5.3", {"start": v(-33.08, -2.2) * mm, "end": v(-31.63, 0.3) * mm});
            skLineSegment(sketch, "E30.6.5.3", {"start": v(-31.63, -4.7) * mm, "end": v(-33.08, -2.2) * mm});
            skLineSegment(sketch, "E30.9.5.3", {"start": v(-28.75, -4.7) * mm, "end": v(-31.63, -4.7) * mm});
            skLineSegment(sketch, "E30.12.5.3", {"start": v(-27.3, -2.2) * mm, "end": v(-28.75, -4.7) * mm});
            skLineSegment(sketch, "E30.15.5.3", {"start": v(-28.75, 0.3) * mm, "end": v(-27.3, -2.2) * mm});
            skLineSegment(sketch, "E30.18.5.3", {"start": v(-26.22, -1.58) * mm, "end": v(-27.66, 0.92) * mm});
            skLineSegment(sketch, "E30.21.5.3", {"start": v(-27.66, 0.92) * mm, "end": v(-26.22, 3.42) * mm});
            skLineSegment(sketch, "E30.24.5.3", {"start": v(-26.22, 3.42) * mm, "end": v(-23.33, 3.42) * mm});
            skLineSegment(sketch, "E30.27.5.3", {"start": v(-23.33, 3.42) * mm, "end": v(-21.89, 0.92) * mm});
            skLineSegment(sketch, "E30.30.5.3", {"start": v(-21.89, 0.92) * mm, "end": v(-23.33, -1.58) * mm});
            skLineSegment(sketch, "E30.33.5.3", {"start": v(-23.33, -1.58) * mm, "end": v(-26.22, -1.58) * mm});
            skLineSegment(sketch, "E30.0.6.0", {"start": v(-20.64, 19.04) * mm, "end": v(-17.75, 19.04) * mm});
            skLineSegment(sketch, "E30.3.6.0", {"start": v(-22.08, 16.54) * mm, "end": v(-20.64, 19.04) * mm});
            skLineSegment(sketch, "E30.6.6.0", {"start": v(-20.64, 14.04) * mm, "end": v(-22.08, 16.54) * mm});
            skLineSegment(sketch, "E30.9.6.0", {"start": v(-17.75, 14.04) * mm, "end": v(-20.64, 14.04) * mm});
            skLineSegment(sketch, "E30.12.6.0", {"start": v(-16.3, 16.54) * mm, "end": v(-17.75, 14.04) * mm});
            skLineSegment(sketch, "E30.15.6.0", {"start": v(-17.75, 19.04) * mm, "end": v(-16.3, 16.54) * mm});
            skLineSegment(sketch, "E30.18.6.0", {"start": v(-15.23, 17.17) * mm, "end": v(-16.67, 19.67) * mm});
            skLineSegment(sketch, "E30.21.6.0", {"start": v(-16.67, 19.67) * mm, "end": v(-15.23, 22.17) * mm});
            skLineSegment(sketch, "E30.24.6.0", {"start": v(-15.23, 22.17) * mm, "end": v(-12.34, 22.17) * mm});
            skLineSegment(sketch, "E30.27.6.0", {"start": v(-12.34, 22.17) * mm, "end": v(-10.9, 19.67) * mm});
            skLineSegment(sketch, "E30.30.6.0", {"start": v(-10.9, 19.67) * mm, "end": v(-12.34, 17.17) * mm});
            skLineSegment(sketch, "E30.33.6.0", {"start": v(-12.34, 17.17) * mm, "end": v(-15.23, 17.17) * mm});
            skLineSegment(sketch, "E30.0.6.1", {"start": v(-20.64, 12.8) * mm, "end": v(-17.75, 12.8) * mm});
            skLineSegment(sketch, "E30.3.6.1", {"start": v(-22.08, 10.3) * mm, "end": v(-20.64, 12.8) * mm});
            skLineSegment(sketch, "E30.6.6.1", {"start": v(-20.64, 7.8) * mm, "end": v(-22.08, 10.3) * mm});
            skLineSegment(sketch, "E30.9.6.1", {"start": v(-17.75, 7.8) * mm, "end": v(-20.64, 7.8) * mm});
            skLineSegment(sketch, "E30.12.6.1", {"start": v(-16.3, 10.3) * mm, "end": v(-17.75, 7.8) * mm});
            skLineSegment(sketch, "E30.15.6.1", {"start": v(-17.75, 12.8) * mm, "end": v(-16.3, 10.3) * mm});
            skLineSegment(sketch, "E30.18.6.1", {"start": v(-15.23, 10.92) * mm, "end": v(-16.67, 13.42) * mm});
            skLineSegment(sketch, "E30.21.6.1", {"start": v(-16.67, 13.42) * mm, "end": v(-15.23, 15.92) * mm});
            skLineSegment(sketch, "E30.24.6.1", {"start": v(-15.23, 15.92) * mm, "end": v(-12.34, 15.92) * mm});
            skLineSegment(sketch, "E30.27.6.1", {"start": v(-12.34, 15.92) * mm, "end": v(-10.9, 13.42) * mm});
            skLineSegment(sketch, "E30.30.6.1", {"start": v(-10.9, 13.42) * mm, "end": v(-12.34, 10.92) * mm});
            skLineSegment(sketch, "E30.33.6.1", {"start": v(-12.34, 10.92) * mm, "end": v(-15.23, 10.92) * mm});
            skLineSegment(sketch, "E30.0.6.2", {"start": v(-20.64, 6.54) * mm, "end": v(-17.75, 6.54) * mm});
            skLineSegment(sketch, "E30.3.6.2", {"start": v(-22.08, 4.04) * mm, "end": v(-20.64, 6.54) * mm});
            skLineSegment(sketch, "E30.6.6.2", {"start": v(-20.64, 1.54) * mm, "end": v(-22.08, 4.04) * mm});
            skLineSegment(sketch, "E30.9.6.2", {"start": v(-17.75, 1.54) * mm, "end": v(-20.64, 1.54) * mm});
            skLineSegment(sketch, "E30.12.6.2", {"start": v(-16.3, 4.04) * mm, "end": v(-17.75, 1.54) * mm});
            skLineSegment(sketch, "E30.15.6.2", {"start": v(-17.75, 6.54) * mm, "end": v(-16.3, 4.04) * mm});
            skLineSegment(sketch, "E30.18.6.2", {"start": v(-15.23, 4.67) * mm, "end": v(-16.67, 7.17) * mm});
            skLineSegment(sketch, "E30.21.6.2", {"start": v(-16.67, 7.17) * mm, "end": v(-15.23, 9.67) * mm});
            skLineSegment(sketch, "E30.24.6.2", {"start": v(-15.23, 9.67) * mm, "end": v(-12.34, 9.67) * mm});
            skLineSegment(sketch, "E30.27.6.2", {"start": v(-12.34, 9.67) * mm, "end": v(-10.9, 7.17) * mm});
            skLineSegment(sketch, "E30.30.6.2", {"start": v(-10.9, 7.17) * mm, "end": v(-12.34, 4.67) * mm});
            skLineSegment(sketch, "E30.33.6.2", {"start": v(-12.34, 4.67) * mm, "end": v(-15.23, 4.67) * mm});
            skLineSegment(sketch, "E30.0.6.3", {"start": v(-20.64, 0.3) * mm, "end": v(-17.75, 0.3) * mm});
            skLineSegment(sketch, "E30.3.6.3", {"start": v(-22.08, -2.2) * mm, "end": v(-20.64, 0.3) * mm});
            skLineSegment(sketch, "E30.6.6.3", {"start": v(-20.64, -4.7) * mm, "end": v(-22.08, -2.2) * mm});
            skLineSegment(sketch, "E30.9.6.3", {"start": v(-17.75, -4.7) * mm, "end": v(-20.64, -4.7) * mm});
            skLineSegment(sketch, "E30.12.6.3", {"start": v(-16.3, -2.2) * mm, "end": v(-17.75, -4.7) * mm});
            skLineSegment(sketch, "E30.15.6.3", {"start": v(-17.75, 0.3) * mm, "end": v(-16.3, -2.2) * mm});
            skLineSegment(sketch, "E30.18.6.3", {"start": v(-15.23, -1.58) * mm, "end": v(-16.67, 0.92) * mm});
            skLineSegment(sketch, "E30.21.6.3", {"start": v(-16.67, 0.92) * mm, "end": v(-15.23, 3.42) * mm});
            skLineSegment(sketch, "E30.24.6.3", {"start": v(-15.23, 3.42) * mm, "end": v(-12.34, 3.42) * mm});
            skLineSegment(sketch, "E30.27.6.3", {"start": v(-12.34, 3.42) * mm, "end": v(-10.9, 0.92) * mm});
            skLineSegment(sketch, "E30.30.6.3", {"start": v(-10.9, 0.92) * mm, "end": v(-12.34, -1.58) * mm});
            skLineSegment(sketch, "E30.33.6.3", {"start": v(-12.34, -1.58) * mm, "end": v(-15.23, -1.58) * mm});
            skLineSegment(sketch, "E30.0.7.0", {"start": v(-9.65, 19.04) * mm, "end": v(-6.76, 19.04) * mm});
            skLineSegment(sketch, "E30.3.7.0", {"start": v(-11.09, 16.54) * mm, "end": v(-9.65, 19.04) * mm});
            skLineSegment(sketch, "E30.6.7.0", {"start": v(-9.65, 14.04) * mm, "end": v(-11.09, 16.54) * mm});
            skLineSegment(sketch, "E30.9.7.0", {"start": v(-6.76, 14.04) * mm, "end": v(-9.65, 14.04) * mm});
            skLineSegment(sketch, "E30.12.7.0", {"start": v(-5.32, 16.54) * mm, "end": v(-6.76, 14.04) * mm});
            skLineSegment(sketch, "E30.15.7.0", {"start": v(-6.76, 19.04) * mm, "end": v(-5.32, 16.54) * mm});
            skLineSegment(sketch, "E30.18.7.0", {"start": v(-4.23, 17.17) * mm, "end": v(-5.68, 19.67) * mm});
            skLineSegment(sketch, "E30.21.7.0", {"start": v(-5.68, 19.67) * mm, "end": v(-4.23, 22.17) * mm});
            skLineSegment(sketch, "E30.24.7.0", {"start": v(-4.23, 22.17) * mm, "end": v(-1.35, 22.17) * mm});
            skLineSegment(sketch, "E30.27.7.0", {"start": v(-1.35, 22.17) * mm, "end": v(0.1, 19.67) * mm});
            skLineSegment(sketch, "E30.30.7.0", {"start": v(0.1, 19.67) * mm, "end": v(-1.35, 17.17) * mm});
            skLineSegment(sketch, "E30.33.7.0", {"start": v(-1.35, 17.17) * mm, "end": v(-4.23, 17.17) * mm});
            skLineSegment(sketch, "E30.0.7.1", {"start": v(-9.65, 12.8) * mm, "end": v(-6.76, 12.8) * mm});
            skLineSegment(sketch, "E30.3.7.1", {"start": v(-11.09, 10.3) * mm, "end": v(-9.65, 12.8) * mm});
            skLineSegment(sketch, "E30.6.7.1", {"start": v(-9.65, 7.8) * mm, "end": v(-11.09, 10.3) * mm});
            skLineSegment(sketch, "E30.9.7.1", {"start": v(-6.76, 7.8) * mm, "end": v(-9.65, 7.8) * mm});
            skLineSegment(sketch, "E30.12.7.1", {"start": v(-5.32, 10.3) * mm, "end": v(-6.76, 7.8) * mm});
            skLineSegment(sketch, "E30.15.7.1", {"start": v(-6.76, 12.8) * mm, "end": v(-5.32, 10.3) * mm});
            skLineSegment(sketch, "E30.18.7.1", {"start": v(-4.23, 10.92) * mm, "end": v(-5.68, 13.42) * mm});
            skLineSegment(sketch, "E30.21.7.1", {"start": v(-5.68, 13.42) * mm, "end": v(-4.23, 15.92) * mm});
            skLineSegment(sketch, "E30.24.7.1", {"start": v(-4.23, 15.92) * mm, "end": v(-1.35, 15.92) * mm});
            skLineSegment(sketch, "E30.27.7.1", {"start": v(-1.35, 15.92) * mm, "end": v(0.1, 13.42) * mm});
            skLineSegment(sketch, "E30.30.7.1", {"start": v(0.1, 13.42) * mm, "end": v(-1.35, 10.92) * mm});
            skLineSegment(sketch, "E30.33.7.1", {"start": v(-1.35, 10.92) * mm, "end": v(-4.23, 10.92) * mm});
            skLineSegment(sketch, "E30.0.7.2", {"start": v(-9.65, 6.54) * mm, "end": v(-6.76, 6.54) * mm});
            skLineSegment(sketch, "E30.3.7.2", {"start": v(-11.09, 4.04) * mm, "end": v(-9.65, 6.54) * mm});
            skLineSegment(sketch, "E30.6.7.2", {"start": v(-9.65, 1.54) * mm, "end": v(-11.09, 4.04) * mm});
            skLineSegment(sketch, "E30.9.7.2", {"start": v(-6.76, 1.54) * mm, "end": v(-9.65, 1.54) * mm});
            skLineSegment(sketch, "E30.12.7.2", {"start": v(-5.32, 4.04) * mm, "end": v(-6.76, 1.54) * mm});
            skLineSegment(sketch, "E30.15.7.2", {"start": v(-6.76, 6.54) * mm, "end": v(-5.32, 4.04) * mm});
            skLineSegment(sketch, "E30.18.7.2", {"start": v(-4.23, 4.67) * mm, "end": v(-5.68, 7.17) * mm});
            skLineSegment(sketch, "E30.21.7.2", {"start": v(-5.68, 7.17) * mm, "end": v(-4.23, 9.67) * mm});
            skLineSegment(sketch, "E30.24.7.2", {"start": v(-4.23, 9.67) * mm, "end": v(-1.35, 9.67) * mm});
            skLineSegment(sketch, "E30.27.7.2", {"start": v(-1.35, 9.67) * mm, "end": v(0.1, 7.17) * mm});
            skLineSegment(sketch, "E30.30.7.2", {"start": v(0.1, 7.17) * mm, "end": v(-1.35, 4.67) * mm});
            skLineSegment(sketch, "E30.33.7.2", {"start": v(-1.35, 4.67) * mm, "end": v(-4.23, 4.67) * mm});
            skLineSegment(sketch, "E30.0.7.3", {"start": v(-9.65, 0.3) * mm, "end": v(-6.76, 0.3) * mm});
            skLineSegment(sketch, "E30.3.7.3", {"start": v(-11.09, -2.2) * mm, "end": v(-9.65, 0.3) * mm});
            skLineSegment(sketch, "E30.6.7.3", {"start": v(-9.65, -4.7) * mm, "end": v(-11.09, -2.2) * mm});
            skLineSegment(sketch, "E30.9.7.3", {"start": v(-6.76, -4.7) * mm, "end": v(-9.65, -4.7) * mm});
            skLineSegment(sketch, "E30.12.7.3", {"start": v(-5.32, -2.2) * mm, "end": v(-6.76, -4.7) * mm});
            skLineSegment(sketch, "E30.15.7.3", {"start": v(-6.76, 0.3) * mm, "end": v(-5.32, -2.2) * mm});
            skLineSegment(sketch, "E30.18.7.3", {"start": v(-4.23, -1.58) * mm, "end": v(-5.68, 0.92) * mm});
            skLineSegment(sketch, "E30.21.7.3", {"start": v(-5.68, 0.92) * mm, "end": v(-4.23, 3.42) * mm});
            skLineSegment(sketch, "E30.24.7.3", {"start": v(-4.23, 3.42) * mm, "end": v(-1.35, 3.42) * mm});
            skLineSegment(sketch, "E30.27.7.3", {"start": v(-1.35, 3.42) * mm, "end": v(0.1, 0.92) * mm});
            skLineSegment(sketch, "E30.30.7.3", {"start": v(0.1, 0.92) * mm, "end": v(-1.35, -1.58) * mm});
            skLineSegment(sketch, "E30.33.7.3", {"start": v(-1.35, -1.58) * mm, "end": v(-4.23, -1.58) * mm});
            skLineSegment(sketch, "E30.0.8.0", {"start": v(1.35, 19.04) * mm, "end": v(4.23, 19.04) * mm});
            skLineSegment(sketch, "E30.3.8.0", {"start": v(-0.1, 16.54) * mm, "end": v(1.35, 19.04) * mm});
            skLineSegment(sketch, "E30.6.8.0", {"start": v(1.35, 14.04) * mm, "end": v(-0.1, 16.54) * mm});
            skLineSegment(sketch, "E30.9.8.0", {"start": v(4.23, 14.04) * mm, "end": v(1.35, 14.04) * mm});
            skLineSegment(sketch, "E30.12.8.0", {"start": v(5.68, 16.54) * mm, "end": v(4.23, 14.04) * mm});
            skLineSegment(sketch, "E30.15.8.0", {"start": v(4.23, 19.04) * mm, "end": v(5.68, 16.54) * mm});
            skLineSegment(sketch, "E30.18.8.0", {"start": v(6.76, 17.17) * mm, "end": v(5.32, 19.67) * mm});
            skLineSegment(sketch, "E30.21.8.0", {"start": v(5.32, 19.67) * mm, "end": v(6.76, 22.17) * mm});
            skLineSegment(sketch, "E30.24.8.0", {"start": v(6.76, 22.17) * mm, "end": v(9.65, 22.17) * mm});
            skLineSegment(sketch, "E30.27.8.0", {"start": v(9.65, 22.17) * mm, "end": v(11.09, 19.67) * mm});
            skLineSegment(sketch, "E30.30.8.0", {"start": v(11.09, 19.67) * mm, "end": v(9.65, 17.17) * mm});
            skLineSegment(sketch, "E30.33.8.0", {"start": v(9.65, 17.17) * mm, "end": v(6.76, 17.17) * mm});
            skLineSegment(sketch, "E30.0.8.1", {"start": v(1.35, 12.8) * mm, "end": v(4.23, 12.8) * mm});
            skLineSegment(sketch, "E30.3.8.1", {"start": v(-0.1, 10.3) * mm, "end": v(1.35, 12.8) * mm});
            skLineSegment(sketch, "E30.6.8.1", {"start": v(1.35, 7.8) * mm, "end": v(-0.1, 10.3) * mm});
            skLineSegment(sketch, "E30.9.8.1", {"start": v(4.23, 7.8) * mm, "end": v(1.35, 7.8) * mm});
            skLineSegment(sketch, "E30.12.8.1", {"start": v(5.68, 10.3) * mm, "end": v(4.23, 7.8) * mm});
            skLineSegment(sketch, "E30.15.8.1", {"start": v(4.23, 12.8) * mm, "end": v(5.68, 10.3) * mm});
            skLineSegment(sketch, "E30.18.8.1", {"start": v(6.76, 10.92) * mm, "end": v(5.32, 13.42) * mm});
            skLineSegment(sketch, "E30.21.8.1", {"start": v(5.32, 13.42) * mm, "end": v(6.76, 15.92) * mm});
            skLineSegment(sketch, "E30.24.8.1", {"start": v(6.76, 15.92) * mm, "end": v(9.65, 15.92) * mm});
            skLineSegment(sketch, "E30.27.8.1", {"start": v(9.65, 15.92) * mm, "end": v(11.09, 13.42) * mm});
            skLineSegment(sketch, "E30.30.8.1", {"start": v(11.09, 13.42) * mm, "end": v(9.65, 10.92) * mm});
            skLineSegment(sketch, "E30.33.8.1", {"start": v(9.65, 10.92) * mm, "end": v(6.76, 10.92) * mm});
            skLineSegment(sketch, "E30.0.8.2", {"start": v(1.35, 6.54) * mm, "end": v(4.23, 6.54) * mm});
            skLineSegment(sketch, "E30.3.8.2", {"start": v(-0.1, 4.04) * mm, "end": v(1.35, 6.54) * mm});
            skLineSegment(sketch, "E30.6.8.2", {"start": v(1.35, 1.54) * mm, "end": v(-0.1, 4.04) * mm});
            skLineSegment(sketch, "E30.9.8.2", {"start": v(4.23, 1.54) * mm, "end": v(1.35, 1.54) * mm});
            skLineSegment(sketch, "E30.12.8.2", {"start": v(5.68, 4.04) * mm, "end": v(4.23, 1.54) * mm});
            skLineSegment(sketch, "E30.15.8.2", {"start": v(4.23, 6.54) * mm, "end": v(5.68, 4.04) * mm});
            skLineSegment(sketch, "E30.18.8.2", {"start": v(6.76, 4.67) * mm, "end": v(5.32, 7.17) * mm});
            skLineSegment(sketch, "E30.21.8.2", {"start": v(5.32, 7.17) * mm, "end": v(6.76, 9.67) * mm});
            skLineSegment(sketch, "E30.24.8.2", {"start": v(6.76, 9.67) * mm, "end": v(9.65, 9.67) * mm});
            skLineSegment(sketch, "E30.27.8.2", {"start": v(9.65, 9.67) * mm, "end": v(11.09, 7.17) * mm});
            skLineSegment(sketch, "E30.30.8.2", {"start": v(11.09, 7.17) * mm, "end": v(9.65, 4.67) * mm});
            skLineSegment(sketch, "E30.33.8.2", {"start": v(9.65, 4.67) * mm, "end": v(6.76, 4.67) * mm});
            skLineSegment(sketch, "E30.0.8.3", {"start": v(1.35, 0.3) * mm, "end": v(4.23, 0.3) * mm});
            skLineSegment(sketch, "E30.3.8.3", {"start": v(-0.1, -2.2) * mm, "end": v(1.35, 0.3) * mm});
            skLineSegment(sketch, "E30.6.8.3", {"start": v(1.35, -4.7) * mm, "end": v(-0.1, -2.2) * mm});
            skLineSegment(sketch, "E30.9.8.3", {"start": v(4.23, -4.7) * mm, "end": v(1.35, -4.7) * mm});
            skLineSegment(sketch, "E30.12.8.3", {"start": v(5.68, -2.2) * mm, "end": v(4.23, -4.7) * mm});
            skLineSegment(sketch, "E30.15.8.3", {"start": v(4.23, 0.3) * mm, "end": v(5.68, -2.2) * mm});
            skLineSegment(sketch, "E30.18.8.3", {"start": v(6.76, -1.58) * mm, "end": v(5.32, 0.92) * mm});
            skLineSegment(sketch, "E30.21.8.3", {"start": v(5.32, 0.92) * mm, "end": v(6.76, 3.42) * mm});
            skLineSegment(sketch, "E30.24.8.3", {"start": v(6.76, 3.42) * mm, "end": v(9.65, 3.42) * mm});
            skLineSegment(sketch, "E30.27.8.3", {"start": v(9.65, 3.42) * mm, "end": v(11.09, 0.92) * mm});
            skLineSegment(sketch, "E30.30.8.3", {"start": v(11.09, 0.92) * mm, "end": v(9.65, -1.58) * mm});
            skLineSegment(sketch, "E30.33.8.3", {"start": v(9.65, -1.58) * mm, "end": v(6.76, -1.58) * mm});
            skLineSegment(sketch, "E30.0.9.0", {"start": v(12.34, 19.04) * mm, "end": v(15.23, 19.04) * mm});
            skLineSegment(sketch, "E30.3.9.0", {"start": v(10.9, 16.54) * mm, "end": v(12.34, 19.04) * mm});
            skLineSegment(sketch, "E30.6.9.0", {"start": v(12.34, 14.04) * mm, "end": v(10.9, 16.54) * mm});
            skLineSegment(sketch, "E30.9.9.0", {"start": v(15.23, 14.04) * mm, "end": v(12.34, 14.04) * mm});
            skLineSegment(sketch, "E30.12.9.0", {"start": v(16.67, 16.54) * mm, "end": v(15.23, 14.04) * mm});
            skLineSegment(sketch, "E30.15.9.0", {"start": v(15.23, 19.04) * mm, "end": v(16.67, 16.54) * mm});
            skLineSegment(sketch, "E30.18.9.0", {"start": v(17.75, 17.17) * mm, "end": v(16.3, 19.67) * mm});
            skLineSegment(sketch, "E30.21.9.0", {"start": v(16.3, 19.67) * mm, "end": v(17.75, 22.17) * mm});
            skLineSegment(sketch, "E30.24.9.0", {"start": v(17.75, 22.17) * mm, "end": v(20.64, 22.17) * mm});
            skLineSegment(sketch, "E30.27.9.0", {"start": v(20.64, 22.17) * mm, "end": v(22.08, 19.67) * mm});
            skLineSegment(sketch, "E30.30.9.0", {"start": v(22.08, 19.67) * mm, "end": v(20.64, 17.17) * mm});
            skLineSegment(sketch, "E30.33.9.0", {"start": v(20.64, 17.17) * mm, "end": v(17.75, 17.17) * mm});
            skLineSegment(sketch, "E30.0.9.1", {"start": v(12.34, 12.8) * mm, "end": v(15.23, 12.8) * mm});
            skLineSegment(sketch, "E30.3.9.1", {"start": v(10.9, 10.3) * mm, "end": v(12.34, 12.8) * mm});
            skLineSegment(sketch, "E30.6.9.1", {"start": v(12.34, 7.8) * mm, "end": v(10.9, 10.3) * mm});
            skLineSegment(sketch, "E30.9.9.1", {"start": v(15.23, 7.8) * mm, "end": v(12.34, 7.8) * mm});
            skLineSegment(sketch, "E30.12.9.1", {"start": v(16.67, 10.3) * mm, "end": v(15.23, 7.8) * mm});
            skLineSegment(sketch, "E30.15.9.1", {"start": v(15.23, 12.8) * mm, "end": v(16.67, 10.3) * mm});
            skLineSegment(sketch, "E30.18.9.1", {"start": v(17.75, 10.92) * mm, "end": v(16.3, 13.42) * mm});
            skLineSegment(sketch, "E30.21.9.1", {"start": v(16.3, 13.42) * mm, "end": v(17.75, 15.92) * mm});
            skLineSegment(sketch, "E30.24.9.1", {"start": v(17.75, 15.92) * mm, "end": v(20.64, 15.92) * mm});
            skLineSegment(sketch, "E30.27.9.1", {"start": v(20.64, 15.92) * mm, "end": v(22.08, 13.42) * mm});
            skLineSegment(sketch, "E30.30.9.1", {"start": v(22.08, 13.42) * mm, "end": v(20.64, 10.92) * mm});
            skLineSegment(sketch, "E30.33.9.1", {"start": v(20.64, 10.92) * mm, "end": v(17.75, 10.92) * mm});
            skLineSegment(sketch, "E30.0.9.2", {"start": v(12.34, 6.54) * mm, "end": v(15.23, 6.54) * mm});
            skLineSegment(sketch, "E30.3.9.2", {"start": v(10.9, 4.04) * mm, "end": v(12.34, 6.54) * mm});
            skLineSegment(sketch, "E30.6.9.2", {"start": v(12.34, 1.54) * mm, "end": v(10.9, 4.04) * mm});
            skLineSegment(sketch, "E30.9.9.2", {"start": v(15.23, 1.54) * mm, "end": v(12.34, 1.54) * mm});
            skLineSegment(sketch, "E30.12.9.2", {"start": v(16.67, 4.04) * mm, "end": v(15.23, 1.54) * mm});
            skLineSegment(sketch, "E30.15.9.2", {"start": v(15.23, 6.54) * mm, "end": v(16.67, 4.04) * mm});
            skLineSegment(sketch, "E30.18.9.2", {"start": v(17.75, 4.67) * mm, "end": v(16.3, 7.17) * mm});
            skLineSegment(sketch, "E30.21.9.2", {"start": v(16.3, 7.17) * mm, "end": v(17.75, 9.67) * mm});
            skLineSegment(sketch, "E30.24.9.2", {"start": v(17.75, 9.67) * mm, "end": v(20.64, 9.67) * mm});
            skLineSegment(sketch, "E30.27.9.2", {"start": v(20.64, 9.67) * mm, "end": v(22.08, 7.17) * mm});
            skLineSegment(sketch, "E30.30.9.2", {"start": v(22.08, 7.17) * mm, "end": v(20.64, 4.67) * mm});
            skLineSegment(sketch, "E30.33.9.2", {"start": v(20.64, 4.67) * mm, "end": v(17.75, 4.67) * mm});
            skLineSegment(sketch, "E30.0.9.3", {"start": v(12.34, 0.3) * mm, "end": v(15.23, 0.3) * mm});
            skLineSegment(sketch, "E30.3.9.3", {"start": v(10.9, -2.2) * mm, "end": v(12.34, 0.3) * mm});
            skLineSegment(sketch, "E30.6.9.3", {"start": v(12.34, -4.7) * mm, "end": v(10.9, -2.2) * mm});
            skLineSegment(sketch, "E30.9.9.3", {"start": v(15.23, -4.7) * mm, "end": v(12.34, -4.7) * mm});
            skLineSegment(sketch, "E30.12.9.3", {"start": v(16.67, -2.2) * mm, "end": v(15.23, -4.7) * mm});
            skLineSegment(sketch, "E30.15.9.3", {"start": v(15.23, 0.3) * mm, "end": v(16.67, -2.2) * mm});
            skLineSegment(sketch, "E30.18.9.3", {"start": v(17.75, -1.58) * mm, "end": v(16.3, 0.92) * mm});
            skLineSegment(sketch, "E30.21.9.3", {"start": v(16.3, 0.92) * mm, "end": v(17.75, 3.42) * mm});
            skLineSegment(sketch, "E30.24.9.3", {"start": v(17.75, 3.42) * mm, "end": v(20.64, 3.42) * mm});
            skLineSegment(sketch, "E30.27.9.3", {"start": v(20.64, 3.42) * mm, "end": v(22.08, 0.92) * mm});
            skLineSegment(sketch, "E30.30.9.3", {"start": v(22.08, 0.92) * mm, "end": v(20.64, -1.58) * mm});
            skLineSegment(sketch, "E30.33.9.3", {"start": v(20.64, -1.58) * mm, "end": v(17.75, -1.58) * mm});
            skLineSegment(sketch, "E31.0.10.0", {"start": v(23.33, 19.04) * mm, "end": v(26.22, 19.04) * mm});
            skLineSegment(sketch, "E31.3.10.0", {"start": v(21.89, 16.54) * mm, "end": v(23.33, 19.04) * mm});
            skLineSegment(sketch, "E31.6.10.0", {"start": v(23.33, 14.04) * mm, "end": v(21.89, 16.54) * mm});
            skLineSegment(sketch, "E31.9.10.0", {"start": v(26.22, 14.04) * mm, "end": v(23.33, 14.04) * mm});
            skLineSegment(sketch, "E31.12.10.0", {"start": v(27.66, 16.54) * mm, "end": v(26.22, 14.04) * mm});
            skLineSegment(sketch, "E31.15.10.0", {"start": v(26.22, 19.04) * mm, "end": v(27.66, 16.54) * mm});
            skLineSegment(sketch, "E31.18.10.0", {"start": v(28.75, 17.17) * mm, "end": v(27.3, 19.67) * mm});
            skLineSegment(sketch, "E31.21.10.0", {"start": v(27.3, 19.67) * mm, "end": v(28.75, 22.17) * mm});
            skLineSegment(sketch, "E31.24.10.0", {"start": v(28.75, 22.17) * mm, "end": v(31.63, 22.17) * mm});
            skLineSegment(sketch, "E31.27.10.0", {"start": v(31.63, 22.17) * mm, "end": v(33.08, 19.67) * mm});
            skLineSegment(sketch, "E31.30.10.0", {"start": v(33.08, 19.67) * mm, "end": v(31.63, 17.17) * mm});
            skLineSegment(sketch, "E31.33.10.0", {"start": v(31.63, 17.17) * mm, "end": v(28.75, 17.17) * mm});
            skLineSegment(sketch, "E31.0.10.1", {"start": v(23.33, 12.8) * mm, "end": v(26.22, 12.8) * mm});
            skLineSegment(sketch, "E31.3.10.1", {"start": v(21.89, 10.3) * mm, "end": v(23.33, 12.8) * mm});
            skLineSegment(sketch, "E31.6.10.1", {"start": v(23.33, 7.8) * mm, "end": v(21.89, 10.3) * mm});
            skLineSegment(sketch, "E31.9.10.1", {"start": v(26.22, 7.8) * mm, "end": v(23.33, 7.8) * mm});
            skLineSegment(sketch, "E31.12.10.1", {"start": v(27.66, 10.3) * mm, "end": v(26.22, 7.8) * mm});
            skLineSegment(sketch, "E31.15.10.1", {"start": v(26.22, 12.8) * mm, "end": v(27.66, 10.3) * mm});
            skLineSegment(sketch, "E31.18.10.1", {"start": v(28.75, 10.92) * mm, "end": v(27.3, 13.42) * mm});
            skLineSegment(sketch, "E31.21.10.1", {"start": v(27.3, 13.42) * mm, "end": v(28.75, 15.92) * mm});
            skLineSegment(sketch, "E31.24.10.1", {"start": v(28.75, 15.92) * mm, "end": v(31.63, 15.92) * mm});
            skLineSegment(sketch, "E31.27.10.1", {"start": v(31.63, 15.92) * mm, "end": v(33.08, 13.42) * mm});
            skLineSegment(sketch, "E31.30.10.1", {"start": v(33.08, 13.42) * mm, "end": v(31.63, 10.92) * mm});
            skLineSegment(sketch, "E31.33.10.1", {"start": v(31.63, 10.92) * mm, "end": v(28.75, 10.92) * mm});
            skLineSegment(sketch, "E31.0.10.2", {"start": v(23.33, 6.54) * mm, "end": v(26.22, 6.54) * mm});
            skLineSegment(sketch, "E31.3.10.2", {"start": v(21.89, 4.04) * mm, "end": v(23.33, 6.54) * mm});
            skLineSegment(sketch, "E31.6.10.2", {"start": v(23.33, 1.54) * mm, "end": v(21.89, 4.04) * mm});
            skLineSegment(sketch, "E31.9.10.2", {"start": v(26.22, 1.54) * mm, "end": v(23.33, 1.54) * mm});
            skLineSegment(sketch, "E31.12.10.2", {"start": v(27.66, 4.04) * mm, "end": v(26.22, 1.54) * mm});
            skLineSegment(sketch, "E31.15.10.2", {"start": v(26.22, 6.54) * mm, "end": v(27.66, 4.04) * mm});
            skLineSegment(sketch, "E31.18.10.2", {"start": v(28.75, 4.67) * mm, "end": v(27.3, 7.17) * mm});
            skLineSegment(sketch, "E31.21.10.2", {"start": v(27.3, 7.17) * mm, "end": v(28.75, 9.67) * mm});
            skLineSegment(sketch, "E31.24.10.2", {"start": v(28.75, 9.67) * mm, "end": v(31.63, 9.67) * mm});
            skLineSegment(sketch, "E31.27.10.2", {"start": v(31.63, 9.67) * mm, "end": v(33.08, 7.17) * mm});
            skLineSegment(sketch, "E31.30.10.2", {"start": v(33.08, 7.17) * mm, "end": v(31.63, 4.67) * mm});
            skLineSegment(sketch, "E31.33.10.2", {"start": v(31.63, 4.67) * mm, "end": v(28.75, 4.67) * mm});
            skLineSegment(sketch, "E31.0.10.3", {"start": v(23.33, 0.3) * mm, "end": v(26.22, 0.3) * mm});
            skLineSegment(sketch, "E31.3.10.3", {"start": v(21.89, -2.2) * mm, "end": v(23.33, 0.3) * mm});
            skLineSegment(sketch, "E31.6.10.3", {"start": v(23.33, -4.7) * mm, "end": v(21.89, -2.2) * mm});
            skLineSegment(sketch, "E31.9.10.3", {"start": v(26.22, -4.7) * mm, "end": v(23.33, -4.7) * mm});
            skLineSegment(sketch, "E31.12.10.3", {"start": v(27.66, -2.2) * mm, "end": v(26.22, -4.7) * mm});
            skLineSegment(sketch, "E31.15.10.3", {"start": v(26.22, 0.3) * mm, "end": v(27.66, -2.2) * mm});
            skLineSegment(sketch, "E31.18.10.3", {"start": v(28.75, -1.58) * mm, "end": v(27.3, 0.92) * mm});
            skLineSegment(sketch, "E31.21.10.3", {"start": v(27.3, 0.92) * mm, "end": v(28.75, 3.42) * mm});
            skLineSegment(sketch, "E31.24.10.3", {"start": v(28.75, 3.42) * mm, "end": v(31.63, 3.42) * mm});
            skLineSegment(sketch, "E31.27.10.3", {"start": v(31.63, 3.42) * mm, "end": v(33.08, 0.92) * mm});
            skLineSegment(sketch, "E31.30.10.3", {"start": v(33.08, 0.92) * mm, "end": v(31.63, -1.58) * mm});
            skLineSegment(sketch, "E31.33.10.3", {"start": v(31.63, -1.58) * mm, "end": v(28.75, -1.58) * mm});
            skLineSegment(sketch, "E31.0.11.0", {"start": v(34.33, 19.04) * mm, "end": v(37.21, 19.04) * mm});
            skLineSegment(sketch, "E31.3.11.0", {"start": v(32.88, 16.54) * mm, "end": v(34.33, 19.04) * mm});
            skLineSegment(sketch, "E31.6.11.0", {"start": v(34.33, 14.04) * mm, "end": v(32.88, 16.54) * mm});
            skLineSegment(sketch, "E31.9.11.0", {"start": v(37.21, 14.04) * mm, "end": v(34.33, 14.04) * mm});
            skLineSegment(sketch, "E31.12.11.0", {"start": v(38.66, 16.54) * mm, "end": v(37.21, 14.04) * mm});
            skLineSegment(sketch, "E31.15.11.0", {"start": v(37.21, 19.04) * mm, "end": v(38.66, 16.54) * mm});
            skLineSegment(sketch, "E31.18.11.0", {"start": v(39.74, 17.17) * mm, "end": v(38.3, 19.67) * mm});
            skLineSegment(sketch, "E31.21.11.0", {"start": v(38.3, 19.67) * mm, "end": v(39.74, 22.17) * mm});
            skLineSegment(sketch, "E31.24.11.0", {"start": v(39.74, 22.17) * mm, "end": v(42.63, 22.17) * mm});
            skLineSegment(sketch, "E31.27.11.0", {"start": v(42.63, 22.17) * mm, "end": v(44.07, 19.67) * mm});
            skLineSegment(sketch, "E31.30.11.0", {"start": v(44.07, 19.67) * mm, "end": v(42.63, 17.17) * mm});
            skLineSegment(sketch, "E31.33.11.0", {"start": v(42.63, 17.17) * mm, "end": v(39.74, 17.17) * mm});
            skLineSegment(sketch, "E31.0.11.1", {"start": v(34.33, 12.8) * mm, "end": v(37.21, 12.8) * mm});
            skLineSegment(sketch, "E31.3.11.1", {"start": v(32.88, 10.3) * mm, "end": v(34.33, 12.8) * mm});
            skLineSegment(sketch, "E31.6.11.1", {"start": v(34.33, 7.8) * mm, "end": v(32.88, 10.3) * mm});
            skLineSegment(sketch, "E31.9.11.1", {"start": v(37.21, 7.8) * mm, "end": v(34.33, 7.8) * mm});
            skLineSegment(sketch, "E31.12.11.1", {"start": v(38.66, 10.3) * mm, "end": v(37.21, 7.8) * mm});
            skLineSegment(sketch, "E31.15.11.1", {"start": v(37.21, 12.8) * mm, "end": v(38.66, 10.3) * mm});
            skLineSegment(sketch, "E31.18.11.1", {"start": v(39.74, 10.92) * mm, "end": v(38.3, 13.42) * mm});
            skLineSegment(sketch, "E31.21.11.1", {"start": v(38.3, 13.42) * mm, "end": v(39.74, 15.92) * mm});
            skLineSegment(sketch, "E31.24.11.1", {"start": v(39.74, 15.92) * mm, "end": v(42.63, 15.92) * mm});
            skLineSegment(sketch, "E31.27.11.1", {"start": v(42.63, 15.92) * mm, "end": v(44.07, 13.42) * mm});
            skLineSegment(sketch, "E31.30.11.1", {"start": v(44.07, 13.42) * mm, "end": v(42.63, 10.92) * mm});
            skLineSegment(sketch, "E31.33.11.1", {"start": v(42.63, 10.92) * mm, "end": v(39.74, 10.92) * mm});
            skLineSegment(sketch, "E31.0.11.2", {"start": v(34.33, 6.54) * mm, "end": v(37.21, 6.54) * mm});
            skLineSegment(sketch, "E31.3.11.2", {"start": v(32.88, 4.04) * mm, "end": v(34.33, 6.54) * mm});
            skLineSegment(sketch, "E31.6.11.2", {"start": v(34.33, 1.54) * mm, "end": v(32.88, 4.04) * mm});
            skLineSegment(sketch, "E31.9.11.2", {"start": v(37.21, 1.54) * mm, "end": v(34.33, 1.54) * mm});
            skLineSegment(sketch, "E31.12.11.2", {"start": v(38.66, 4.04) * mm, "end": v(37.21, 1.54) * mm});
            skLineSegment(sketch, "E31.15.11.2", {"start": v(37.21, 6.54) * mm, "end": v(38.66, 4.04) * mm});
            skLineSegment(sketch, "E31.18.11.2", {"start": v(39.74, 4.67) * mm, "end": v(38.3, 7.17) * mm});
            skLineSegment(sketch, "E31.21.11.2", {"start": v(38.3, 7.17) * mm, "end": v(39.74, 9.67) * mm});
            skLineSegment(sketch, "E31.24.11.2", {"start": v(39.74, 9.67) * mm, "end": v(42.63, 9.67) * mm});
            skLineSegment(sketch, "E31.27.11.2", {"start": v(42.63, 9.67) * mm, "end": v(44.07, 7.17) * mm});
            skLineSegment(sketch, "E31.30.11.2", {"start": v(44.07, 7.17) * mm, "end": v(42.63, 4.67) * mm});
            skLineSegment(sketch, "E31.33.11.2", {"start": v(42.63, 4.67) * mm, "end": v(39.74, 4.67) * mm});
            skLineSegment(sketch, "E31.0.11.3", {"start": v(34.33, 0.3) * mm, "end": v(37.21, 0.3) * mm});
            skLineSegment(sketch, "E31.3.11.3", {"start": v(32.88, -2.2) * mm, "end": v(34.33, 0.3) * mm});
            skLineSegment(sketch, "E31.6.11.3", {"start": v(34.33, -4.7) * mm, "end": v(32.88, -2.2) * mm});
            skLineSegment(sketch, "E31.9.11.3", {"start": v(37.21, -4.7) * mm, "end": v(34.33, -4.7) * mm});
            skLineSegment(sketch, "E31.12.11.3", {"start": v(38.66, -2.2) * mm, "end": v(37.21, -4.7) * mm});
            skLineSegment(sketch, "E31.15.11.3", {"start": v(37.21, 0.3) * mm, "end": v(38.66, -2.2) * mm});
            skLineSegment(sketch, "E31.18.11.3", {"start": v(39.74, -1.58) * mm, "end": v(38.3, 0.92) * mm});
            skLineSegment(sketch, "E31.21.11.3", {"start": v(38.3, 0.92) * mm, "end": v(39.74, 3.42) * mm});
            skLineSegment(sketch, "E31.24.11.3", {"start": v(39.74, 3.42) * mm, "end": v(42.63, 3.42) * mm});
            skLineSegment(sketch, "E31.27.11.3", {"start": v(42.63, 3.42) * mm, "end": v(44.07, 0.92) * mm});
            skLineSegment(sketch, "E31.30.11.3", {"start": v(44.07, 0.92) * mm, "end": v(42.63, -1.58) * mm});
            skLineSegment(sketch, "E31.33.11.3", {"start": v(42.63, -1.58) * mm, "end": v(39.74, -1.58) * mm});
            skLineSegment(sketch, "E31.0.12.0", {"start": v(45.32, 19.04) * mm, "end": v(48.2, 19.04) * mm});
            skLineSegment(sketch, "E31.3.12.0", {"start": v(43.88, 16.54) * mm, "end": v(45.32, 19.04) * mm});
            skLineSegment(sketch, "E31.6.12.0", {"start": v(45.32, 14.04) * mm, "end": v(43.88, 16.54) * mm});
            skLineSegment(sketch, "E31.9.12.0", {"start": v(48.2, 14.04) * mm, "end": v(45.32, 14.04) * mm});
            skLineSegment(sketch, "E31.12.12.0", {"start": v(49.65, 16.54) * mm, "end": v(48.2, 14.04) * mm});
            skLineSegment(sketch, "E31.15.12.0", {"start": v(48.2, 19.04) * mm, "end": v(49.65, 16.54) * mm});
            skLineSegment(sketch, "E31.18.12.0", {"start": v(50.73, 17.17) * mm, "end": v(49.29, 19.67) * mm});
            skLineSegment(sketch, "E31.21.12.0", {"start": v(49.29, 19.67) * mm, "end": v(50.73, 22.17) * mm});
            skLineSegment(sketch, "E31.24.12.0", {"start": v(50.73, 22.17) * mm, "end": v(53.62, 22.17) * mm});
            skLineSegment(sketch, "E31.27.12.0", {"start": v(53.62, 22.17) * mm, "end": v(55.06, 19.67) * mm});
            skLineSegment(sketch, "E31.30.12.0", {"start": v(55.06, 19.67) * mm, "end": v(53.62, 17.17) * mm});
            skLineSegment(sketch, "E31.33.12.0", {"start": v(53.62, 17.17) * mm, "end": v(50.73, 17.17) * mm});
            skLineSegment(sketch, "E31.0.12.1", {"start": v(45.32, 12.8) * mm, "end": v(48.2, 12.8) * mm});
            skLineSegment(sketch, "E31.3.12.1", {"start": v(43.88, 10.3) * mm, "end": v(45.32, 12.8) * mm});
            skLineSegment(sketch, "E31.6.12.1", {"start": v(45.32, 7.8) * mm, "end": v(43.88, 10.3) * mm});
            skLineSegment(sketch, "E31.9.12.1", {"start": v(48.2, 7.8) * mm, "end": v(45.32, 7.8) * mm});
            skLineSegment(sketch, "E31.12.12.1", {"start": v(49.65, 10.3) * mm, "end": v(48.2, 7.8) * mm});
            skLineSegment(sketch, "E31.15.12.1", {"start": v(48.2, 12.8) * mm, "end": v(49.65, 10.3) * mm});
            skLineSegment(sketch, "E31.18.12.1", {"start": v(50.73, 10.92) * mm, "end": v(49.29, 13.42) * mm});
            skLineSegment(sketch, "E31.21.12.1", {"start": v(49.29, 13.42) * mm, "end": v(50.73, 15.92) * mm});
            skLineSegment(sketch, "E31.24.12.1", {"start": v(50.73, 15.92) * mm, "end": v(53.62, 15.92) * mm});
            skLineSegment(sketch, "E31.27.12.1", {"start": v(53.62, 15.92) * mm, "end": v(55.06, 13.42) * mm});
            skLineSegment(sketch, "E31.30.12.1", {"start": v(55.06, 13.42) * mm, "end": v(53.62, 10.92) * mm});
            skLineSegment(sketch, "E31.33.12.1", {"start": v(53.62, 10.92) * mm, "end": v(50.73, 10.92) * mm});
            skLineSegment(sketch, "E31.0.12.2", {"start": v(45.32, 6.54) * mm, "end": v(48.2, 6.54) * mm});
            skLineSegment(sketch, "E31.3.12.2", {"start": v(43.88, 4.04) * mm, "end": v(45.32, 6.54) * mm});
            skLineSegment(sketch, "E31.6.12.2", {"start": v(45.32, 1.54) * mm, "end": v(43.88, 4.04) * mm});
            skLineSegment(sketch, "E31.9.12.2", {"start": v(48.2, 1.54) * mm, "end": v(45.32, 1.54) * mm});
            skLineSegment(sketch, "E31.12.12.2", {"start": v(49.65, 4.04) * mm, "end": v(48.2, 1.54) * mm});
            skLineSegment(sketch, "E31.15.12.2", {"start": v(48.2, 6.54) * mm, "end": v(49.65, 4.04) * mm});
            skLineSegment(sketch, "E31.18.12.2", {"start": v(50.73, 4.67) * mm, "end": v(49.29, 7.17) * mm});
            skLineSegment(sketch, "E31.21.12.2", {"start": v(49.29, 7.17) * mm, "end": v(50.73, 9.67) * mm});
            skLineSegment(sketch, "E31.24.12.2", {"start": v(50.73, 9.67) * mm, "end": v(53.62, 9.67) * mm});
            skLineSegment(sketch, "E31.27.12.2", {"start": v(53.62, 9.67) * mm, "end": v(55.06, 7.17) * mm});
            skLineSegment(sketch, "E31.30.12.2", {"start": v(55.06, 7.17) * mm, "end": v(53.62, 4.67) * mm});
            skLineSegment(sketch, "E31.33.12.2", {"start": v(53.62, 4.67) * mm, "end": v(50.73, 4.67) * mm});
            skLineSegment(sketch, "E31.0.12.3", {"start": v(45.32, 0.3) * mm, "end": v(48.2, 0.3) * mm});
            skLineSegment(sketch, "E31.3.12.3", {"start": v(43.88, -2.2) * mm, "end": v(45.32, 0.3) * mm});
            skLineSegment(sketch, "E31.6.12.3", {"start": v(45.32, -4.7) * mm, "end": v(43.88, -2.2) * mm});
            skLineSegment(sketch, "E31.9.12.3", {"start": v(48.2, -4.7) * mm, "end": v(45.32, -4.7) * mm});
            skLineSegment(sketch, "E31.12.12.3", {"start": v(49.65, -2.2) * mm, "end": v(48.2, -4.7) * mm});
            skLineSegment(sketch, "E31.15.12.3", {"start": v(48.2, 0.3) * mm, "end": v(49.65, -2.2) * mm});
            skLineSegment(sketch, "E31.18.12.3", {"start": v(50.73, -1.58) * mm, "end": v(49.29, 0.92) * mm});
            skLineSegment(sketch, "E31.21.12.3", {"start": v(49.29, 0.92) * mm, "end": v(50.73, 3.42) * mm});
            skLineSegment(sketch, "E31.24.12.3", {"start": v(50.73, 3.42) * mm, "end": v(53.62, 3.42) * mm});
            skLineSegment(sketch, "E31.27.12.3", {"start": v(53.62, 3.42) * mm, "end": v(55.06, 0.92) * mm});
            skLineSegment(sketch, "E31.30.12.3", {"start": v(55.06, 0.92) * mm, "end": v(53.62, -1.58) * mm});
            skLineSegment(sketch, "E31.33.12.3", {"start": v(53.62, -1.58) * mm, "end": v(50.73, -1.58) * mm});
            skLineSegment(sketch, "E31.0.13.0", {"start": v(56.31, 19.04) * mm, "end": v(59.2, 19.04) * mm});
            skLineSegment(sketch, "E31.3.13.0", {"start": v(54.87, 16.54) * mm, "end": v(56.31, 19.04) * mm});
            skLineSegment(sketch, "E31.6.13.0", {"start": v(56.31, 14.04) * mm, "end": v(54.87, 16.54) * mm});
            skLineSegment(sketch, "E31.9.13.0", {"start": v(59.2, 14.04) * mm, "end": v(56.31, 14.04) * mm});
            skLineSegment(sketch, "E31.12.13.0", {"start": v(60.64, 16.54) * mm, "end": v(59.2, 14.04) * mm});
            skLineSegment(sketch, "E31.15.13.0", {"start": v(59.2, 19.04) * mm, "end": v(60.64, 16.54) * mm});
            skLineSegment(sketch, "E31.18.13.0", {"start": v(61.72, 17.17) * mm, "end": v(60.28, 19.67) * mm});
            skLineSegment(sketch, "E31.21.13.0", {"start": v(60.28, 19.67) * mm, "end": v(61.72, 22.17) * mm});
            skLineSegment(sketch, "E31.24.13.0", {"start": v(61.72, 22.17) * mm, "end": v(64.61, 22.17) * mm});
            skLineSegment(sketch, "E31.27.13.0", {"start": v(64.61, 22.17) * mm, "end": v(66.05, 19.67) * mm});
            skLineSegment(sketch, "E31.30.13.0", {"start": v(66.05, 19.67) * mm, "end": v(64.61, 17.17) * mm});
            skLineSegment(sketch, "E31.33.13.0", {"start": v(64.61, 17.17) * mm, "end": v(61.72, 17.17) * mm});
            skLineSegment(sketch, "E31.0.13.1", {"start": v(56.31, 12.8) * mm, "end": v(59.2, 12.8) * mm});
            skLineSegment(sketch, "E31.3.13.1", {"start": v(54.87, 10.3) * mm, "end": v(56.31, 12.8) * mm});
            skLineSegment(sketch, "E31.6.13.1", {"start": v(56.31, 7.8) * mm, "end": v(54.87, 10.3) * mm});
            skLineSegment(sketch, "E31.9.13.1", {"start": v(59.2, 7.8) * mm, "end": v(56.31, 7.8) * mm});
            skLineSegment(sketch, "E31.12.13.1", {"start": v(60.64, 10.3) * mm, "end": v(59.2, 7.8) * mm});
            skLineSegment(sketch, "E31.15.13.1", {"start": v(59.2, 12.8) * mm, "end": v(60.64, 10.3) * mm});
            skLineSegment(sketch, "E31.18.13.1", {"start": v(61.72, 10.92) * mm, "end": v(60.28, 13.42) * mm});
            skLineSegment(sketch, "E31.21.13.1", {"start": v(60.28, 13.42) * mm, "end": v(61.72, 15.92) * mm});
            skLineSegment(sketch, "E31.24.13.1", {"start": v(61.72, 15.92) * mm, "end": v(64.61, 15.92) * mm});
            skLineSegment(sketch, "E31.27.13.1", {"start": v(64.61, 15.92) * mm, "end": v(66.05, 13.42) * mm});
            skLineSegment(sketch, "E31.30.13.1", {"start": v(66.05, 13.42) * mm, "end": v(64.61, 10.92) * mm});
            skLineSegment(sketch, "E31.33.13.1", {"start": v(64.61, 10.92) * mm, "end": v(61.72, 10.92) * mm});
            skLineSegment(sketch, "E31.0.13.2", {"start": v(56.31, 6.54) * mm, "end": v(59.2, 6.54) * mm});
            skLineSegment(sketch, "E31.3.13.2", {"start": v(54.87, 4.04) * mm, "end": v(56.31, 6.54) * mm});
            skLineSegment(sketch, "E31.6.13.2", {"start": v(56.31, 1.54) * mm, "end": v(54.87, 4.04) * mm});
            skLineSegment(sketch, "E31.9.13.2", {"start": v(59.2, 1.54) * mm, "end": v(56.31, 1.54) * mm});
            skLineSegment(sketch, "E31.12.13.2", {"start": v(60.64, 4.04) * mm, "end": v(59.2, 1.54) * mm});
            skLineSegment(sketch, "E31.15.13.2", {"start": v(59.2, 6.54) * mm, "end": v(60.64, 4.04) * mm});
            skLineSegment(sketch, "E31.18.13.2", {"start": v(61.72, 4.67) * mm, "end": v(60.28, 7.17) * mm});
            skLineSegment(sketch, "E31.21.13.2", {"start": v(60.28, 7.17) * mm, "end": v(61.72, 9.67) * mm});
            skLineSegment(sketch, "E31.24.13.2", {"start": v(61.72, 9.67) * mm, "end": v(64.61, 9.67) * mm});
            skLineSegment(sketch, "E31.27.13.2", {"start": v(64.61, 9.67) * mm, "end": v(66.05, 7.17) * mm});
            skLineSegment(sketch, "E31.30.13.2", {"start": v(66.05, 7.17) * mm, "end": v(64.61, 4.67) * mm});
            skLineSegment(sketch, "E31.33.13.2", {"start": v(64.61, 4.67) * mm, "end": v(61.72, 4.67) * mm});
            skLineSegment(sketch, "E31.0.13.3", {"start": v(56.31, 0.3) * mm, "end": v(59.2, 0.3) * mm});
            skLineSegment(sketch, "E31.3.13.3", {"start": v(54.87, -2.2) * mm, "end": v(56.31, 0.3) * mm});
            skLineSegment(sketch, "E31.6.13.3", {"start": v(56.31, -4.7) * mm, "end": v(54.87, -2.2) * mm});
            skLineSegment(sketch, "E31.9.13.3", {"start": v(59.2, -4.7) * mm, "end": v(56.31, -4.7) * mm});
            skLineSegment(sketch, "E31.12.13.3", {"start": v(60.64, -2.2) * mm, "end": v(59.2, -4.7) * mm});
            skLineSegment(sketch, "E31.15.13.3", {"start": v(59.2, 0.3) * mm, "end": v(60.64, -2.2) * mm});
            skLineSegment(sketch, "E31.18.13.3", {"start": v(61.72, -1.58) * mm, "end": v(60.28, 0.92) * mm});
            skLineSegment(sketch, "E31.21.13.3", {"start": v(60.28, 0.92) * mm, "end": v(61.72, 3.42) * mm});
            skLineSegment(sketch, "E31.24.13.3", {"start": v(61.72, 3.42) * mm, "end": v(64.61, 3.42) * mm});
            skLineSegment(sketch, "E31.27.13.3", {"start": v(64.61, 3.42) * mm, "end": v(66.05, 0.92) * mm});
            skLineSegment(sketch, "E31.30.13.3", {"start": v(66.05, 0.92) * mm, "end": v(64.61, -1.58) * mm});
            skLineSegment(sketch, "E31.33.13.3", {"start": v(64.61, -1.58) * mm, "end": v(61.72, -1.58) * mm});
            skLineSegment(sketch, "E31.0.14.0", {"start": v(67.3, 19.04) * mm, "end": v(70.2, 19.04) * mm});
            skLineSegment(sketch, "E31.3.14.0", {"start": v(65.86, 16.54) * mm, "end": v(67.3, 19.04) * mm});
            skLineSegment(sketch, "E31.6.14.0", {"start": v(67.3, 14.04) * mm, "end": v(65.86, 16.54) * mm});
            skLineSegment(sketch, "E31.9.14.0", {"start": v(70.2, 14.04) * mm, "end": v(67.3, 14.04) * mm});
            skLineSegment(sketch, "E31.12.14.0", {"start": v(71.64, 16.54) * mm, "end": v(70.2, 14.04) * mm});
            skLineSegment(sketch, "E31.15.14.0", {"start": v(70.2, 19.04) * mm, "end": v(71.64, 16.54) * mm});
            skLineSegment(sketch, "E31.18.14.0", {"start": v(72.72, 17.17) * mm, "end": v(71.27, 19.67) * mm});
            skLineSegment(sketch, "E31.21.14.0", {"start": v(71.27, 19.67) * mm, "end": v(72.72, 22.17) * mm});
            skLineSegment(sketch, "E31.24.14.0", {"start": v(72.72, 22.17) * mm, "end": v(75.6, 22.17) * mm});
            skLineSegment(sketch, "E31.27.14.0", {"start": v(75.6, 22.17) * mm, "end": v(77.05, 19.67) * mm});
            skLineSegment(sketch, "E31.30.14.0", {"start": v(77.05, 19.67) * mm, "end": v(75.6, 17.17) * mm});
            skLineSegment(sketch, "E31.33.14.0", {"start": v(75.6, 17.17) * mm, "end": v(72.72, 17.17) * mm});
            skLineSegment(sketch, "E31.0.14.1", {"start": v(67.3, 12.8) * mm, "end": v(70.2, 12.8) * mm});
            skLineSegment(sketch, "E31.3.14.1", {"start": v(65.86, 10.3) * mm, "end": v(67.3, 12.8) * mm});
            skLineSegment(sketch, "E31.6.14.1", {"start": v(67.3, 7.8) * mm, "end": v(65.86, 10.3) * mm});
            skLineSegment(sketch, "E31.9.14.1", {"start": v(70.2, 7.8) * mm, "end": v(67.3, 7.8) * mm});
            skLineSegment(sketch, "E31.12.14.1", {"start": v(71.64, 10.3) * mm, "end": v(70.2, 7.8) * mm});
            skLineSegment(sketch, "E31.15.14.1", {"start": v(70.2, 12.8) * mm, "end": v(71.64, 10.3) * mm});
            skLineSegment(sketch, "E31.18.14.1", {"start": v(72.72, 10.92) * mm, "end": v(71.27, 13.42) * mm});
            skLineSegment(sketch, "E31.21.14.1", {"start": v(71.27, 13.42) * mm, "end": v(72.72, 15.92) * mm});
            skLineSegment(sketch, "E31.24.14.1", {"start": v(72.72, 15.92) * mm, "end": v(75.6, 15.92) * mm});
            skLineSegment(sketch, "E31.27.14.1", {"start": v(75.6, 15.92) * mm, "end": v(77.05, 13.42) * mm});
            skLineSegment(sketch, "E31.30.14.1", {"start": v(77.05, 13.42) * mm, "end": v(75.6, 10.92) * mm});
            skLineSegment(sketch, "E31.33.14.1", {"start": v(75.6, 10.92) * mm, "end": v(72.72, 10.92) * mm});
            skLineSegment(sketch, "E31.0.14.2", {"start": v(67.3, 6.54) * mm, "end": v(70.2, 6.54) * mm});
            skLineSegment(sketch, "E31.3.14.2", {"start": v(65.86, 4.04) * mm, "end": v(67.3, 6.54) * mm});
            skLineSegment(sketch, "E31.6.14.2", {"start": v(67.3, 1.54) * mm, "end": v(65.86, 4.04) * mm});
            skLineSegment(sketch, "E31.9.14.2", {"start": v(70.2, 1.54) * mm, "end": v(67.3, 1.54) * mm});
            skLineSegment(sketch, "E31.12.14.2", {"start": v(71.64, 4.04) * mm, "end": v(70.2, 1.54) * mm});
            skLineSegment(sketch, "E31.15.14.2", {"start": v(70.2, 6.54) * mm, "end": v(71.64, 4.04) * mm});
            skLineSegment(sketch, "E31.18.14.2", {"start": v(72.72, 4.67) * mm, "end": v(71.27, 7.17) * mm});
            skLineSegment(sketch, "E31.21.14.2", {"start": v(71.27, 7.17) * mm, "end": v(72.72, 9.67) * mm});
            skLineSegment(sketch, "E31.24.14.2", {"start": v(72.72, 9.67) * mm, "end": v(75.6, 9.67) * mm});
            skLineSegment(sketch, "E31.27.14.2", {"start": v(75.6, 9.67) * mm, "end": v(77.05, 7.17) * mm});
            skLineSegment(sketch, "E31.30.14.2", {"start": v(77.05, 7.17) * mm, "end": v(75.6, 4.67) * mm});
            skLineSegment(sketch, "E31.33.14.2", {"start": v(75.6, 4.67) * mm, "end": v(72.72, 4.67) * mm});
            skLineSegment(sketch, "E31.0.14.3", {"start": v(67.3, 0.3) * mm, "end": v(70.2, 0.3) * mm});
            skLineSegment(sketch, "E31.3.14.3", {"start": v(65.86, -2.2) * mm, "end": v(67.3, 0.3) * mm});
            skLineSegment(sketch, "E31.6.14.3", {"start": v(67.3, -4.7) * mm, "end": v(65.86, -2.2) * mm});
            skLineSegment(sketch, "E31.9.14.3", {"start": v(70.2, -4.7) * mm, "end": v(67.3, -4.7) * mm});
            skLineSegment(sketch, "E31.12.14.3", {"start": v(71.64, -2.2) * mm, "end": v(70.2, -4.7) * mm});
            skLineSegment(sketch, "E31.15.14.3", {"start": v(70.2, 0.3) * mm, "end": v(71.64, -2.2) * mm});
            skLineSegment(sketch, "E31.18.14.3", {"start": v(72.72, -1.58) * mm, "end": v(71.27, 0.92) * mm});
            skLineSegment(sketch, "E31.21.14.3", {"start": v(71.27, 0.92) * mm, "end": v(72.72, 3.42) * mm});
            skLineSegment(sketch, "E31.24.14.3", {"start": v(72.72, 3.42) * mm, "end": v(75.6, 3.42) * mm});
            skLineSegment(sketch, "E31.27.14.3", {"start": v(75.6, 3.42) * mm, "end": v(77.05, 0.92) * mm});
            skLineSegment(sketch, "E31.30.14.3", {"start": v(77.05, 0.92) * mm, "end": v(75.6, -1.58) * mm});
            skLineSegment(sketch, "E31.33.14.3", {"start": v(75.6, -1.58) * mm, "end": v(72.72, -1.58) * mm});
            skLineSegment(sketch, "E31.0.15.0", {"start": v(78.3, 19.04) * mm, "end": v(81.18, 19.04) * mm});
            skLineSegment(sketch, "E31.3.15.0", {"start": v(76.85, 16.54) * mm, "end": v(78.3, 19.04) * mm});
            skLineSegment(sketch, "E31.6.15.0", {"start": v(78.3, 14.04) * mm, "end": v(76.85, 16.54) * mm});
            skLineSegment(sketch, "E31.9.15.0", {"start": v(81.18, 14.04) * mm, "end": v(78.3, 14.04) * mm});
            skLineSegment(sketch, "E31.12.15.0", {"start": v(82.63, 16.54) * mm, "end": v(81.18, 14.04) * mm});
            skLineSegment(sketch, "E31.15.15.0", {"start": v(81.18, 19.04) * mm, "end": v(82.63, 16.54) * mm});
            skLineSegment(sketch, "E31.18.15.0", {"start": v(83.71, 17.17) * mm, "end": v(82.27, 19.67) * mm});
            skLineSegment(sketch, "E31.21.15.0", {"start": v(82.27, 19.67) * mm, "end": v(83.71, 22.17) * mm});
            skLineSegment(sketch, "E31.24.15.0", {"start": v(83.71, 22.17) * mm, "end": v(86.6, 22.17) * mm});
            skLineSegment(sketch, "E31.27.15.0", {"start": v(86.6, 22.17) * mm, "end": v(88.04, 19.67) * mm});
            skLineSegment(sketch, "E31.30.15.0", {"start": v(88.04, 19.67) * mm, "end": v(86.6, 17.17) * mm});
            skLineSegment(sketch, "E31.33.15.0", {"start": v(86.6, 17.17) * mm, "end": v(83.71, 17.17) * mm});
            skLineSegment(sketch, "E31.0.15.1", {"start": v(78.3, 12.8) * mm, "end": v(81.18, 12.8) * mm});
            skLineSegment(sketch, "E31.3.15.1", {"start": v(76.85, 10.3) * mm, "end": v(78.3, 12.8) * mm});
            skLineSegment(sketch, "E31.6.15.1", {"start": v(78.3, 7.8) * mm, "end": v(76.85, 10.3) * mm});
            skLineSegment(sketch, "E31.9.15.1", {"start": v(81.18, 7.8) * mm, "end": v(78.3, 7.8) * mm});
            skLineSegment(sketch, "E31.12.15.1", {"start": v(82.63, 10.3) * mm, "end": v(81.18, 7.8) * mm});
            skLineSegment(sketch, "E31.15.15.1", {"start": v(81.18, 12.8) * mm, "end": v(82.63, 10.3) * mm});
            skLineSegment(sketch, "E31.18.15.1", {"start": v(83.71, 10.92) * mm, "end": v(82.27, 13.42) * mm});
            skLineSegment(sketch, "E31.21.15.1", {"start": v(82.27, 13.42) * mm, "end": v(83.71, 15.92) * mm});
            skLineSegment(sketch, "E31.24.15.1", {"start": v(83.71, 15.92) * mm, "end": v(86.6, 15.92) * mm});
            skLineSegment(sketch, "E31.27.15.1", {"start": v(86.6, 15.92) * mm, "end": v(88.04, 13.42) * mm});
            skLineSegment(sketch, "E31.30.15.1", {"start": v(88.04, 13.42) * mm, "end": v(86.6, 10.92) * mm});
            skLineSegment(sketch, "E31.33.15.1", {"start": v(86.6, 10.92) * mm, "end": v(83.71, 10.92) * mm});
            skLineSegment(sketch, "E31.0.15.2", {"start": v(78.3, 6.54) * mm, "end": v(81.18, 6.54) * mm});
            skLineSegment(sketch, "E31.3.15.2", {"start": v(76.85, 4.04) * mm, "end": v(78.3, 6.54) * mm});
            skLineSegment(sketch, "E31.6.15.2", {"start": v(78.3, 1.54) * mm, "end": v(76.85, 4.04) * mm});
            skLineSegment(sketch, "E31.9.15.2", {"start": v(81.18, 1.54) * mm, "end": v(78.3, 1.54) * mm});
            skLineSegment(sketch, "E31.12.15.2", {"start": v(82.63, 4.04) * mm, "end": v(81.18, 1.54) * mm});
            skLineSegment(sketch, "E31.15.15.2", {"start": v(81.18, 6.54) * mm, "end": v(82.63, 4.04) * mm});
            skLineSegment(sketch, "E31.18.15.2", {"start": v(83.71, 4.67) * mm, "end": v(82.27, 7.17) * mm});
            skLineSegment(sketch, "E31.21.15.2", {"start": v(82.27, 7.17) * mm, "end": v(83.71, 9.67) * mm});
            skLineSegment(sketch, "E31.24.15.2", {"start": v(83.71, 9.67) * mm, "end": v(86.6, 9.67) * mm});
            skLineSegment(sketch, "E31.27.15.2", {"start": v(86.6, 9.67) * mm, "end": v(88.04, 7.17) * mm});
            skLineSegment(sketch, "E31.30.15.2", {"start": v(88.04, 7.17) * mm, "end": v(86.6, 4.67) * mm});
            skLineSegment(sketch, "E31.33.15.2", {"start": v(86.6, 4.67) * mm, "end": v(83.71, 4.67) * mm});
            skLineSegment(sketch, "E31.0.15.3", {"start": v(78.3, 0.3) * mm, "end": v(81.18, 0.3) * mm});
            skLineSegment(sketch, "E31.3.15.3", {"start": v(76.85, -2.2) * mm, "end": v(78.3, 0.3) * mm});
            skLineSegment(sketch, "E31.6.15.3", {"start": v(78.3, -4.7) * mm, "end": v(76.85, -2.2) * mm});
            skLineSegment(sketch, "E31.9.15.3", {"start": v(81.18, -4.7) * mm, "end": v(78.3, -4.7) * mm});
            skLineSegment(sketch, "E31.12.15.3", {"start": v(82.63, -2.2) * mm, "end": v(81.18, -4.7) * mm});
            skLineSegment(sketch, "E31.15.15.3", {"start": v(81.18, 0.3) * mm, "end": v(82.63, -2.2) * mm});
            skLineSegment(sketch, "E31.18.15.3", {"start": v(83.71, -1.58) * mm, "end": v(82.27, 0.92) * mm});
            skLineSegment(sketch, "E31.21.15.3", {"start": v(82.27, 0.92) * mm, "end": v(83.71, 3.42) * mm});
            skLineSegment(sketch, "E31.24.15.3", {"start": v(83.71, 3.42) * mm, "end": v(86.6, 3.42) * mm});
            skLineSegment(sketch, "E31.27.15.3", {"start": v(86.6, 3.42) * mm, "end": v(88.04, 0.92) * mm});
            skLineSegment(sketch, "E31.30.15.3", {"start": v(88.04, 0.92) * mm, "end": v(86.6, -1.58) * mm});
            skLineSegment(sketch, "E31.33.15.3", {"start": v(86.6, -1.58) * mm, "end": v(83.71, -1.58) * mm});
            skSolve(sketch);
        }
        {
            var Q0;
            {var subQ0=sQuery(id+"F6.wireOp",EDGE,"E26.0");Q0=makeQuery(id+"F6.imprint","IMPRINT",FACE,{"disambiguationData":[TD([[makeQuery(id+"F6.imprint","IMPRINT",EDGE,{"derivedFrom":subQ0}),-1.0]])]});}
            var Q1;
            {var subQ5=sQuery(id+"F6.wireOp",EDGE,"E27.0.1.0");Q1=makeQuery(id+"F6.imprint","IMPRINT",FACE,{"disambiguationData":[TD([[makeQuery(id+"F6.imprint","IMPRINT",EDGE,{"derivedFrom":subQ5}),-1.0]])]});}
            var Q2;
            {var subQ0=sQuery(id+"F6.wireOp",EDGE,"E28.0.0.2");Q2=makeQuery(id+"F6.imprint","IMPRINT",FACE,{"disambiguationData":[TD([[makeQuery(id+"F6.imprint","IMPRINT",EDGE,{"derivedFrom":subQ0}),-1.0]])]});}
            var Q3;
            {var subQ5=sQuery(id+"F6.wireOp",EDGE,"E25.0");Q3=makeQuery(id+"F6.imprint","IMPRINT",FACE,{"disambiguationData":[TD([[makeQuery(id+"F6.imprint","IMPRINT",EDGE,{"derivedFrom":subQ5}),-1.0]])]});}
            var Q4;
            Q4=makeQuery(id+"F6.imprint","IMPRINT",FACE,{"disambiguationData":[TD([[makeQuery(id+"F6.imprint","IMPRINT",EDGE,{"derivedFrom":sQuery(id+"F6.wireOp",EDGE,"E27.0.1.6")}),-1.0]])]});
            var Q5;
            Q5=makeQuery(id+"F6.imprint","IMPRINT",FACE,{"disambiguationData":[TD([[makeQuery(id+"F6.imprint","IMPRINT",EDGE,{"derivedFrom":sQuery(id+"F6.wireOp",EDGE,"E28.18.0.2")}),-1.0]])]});
            var Q6;
            {var subQ5=sQuery(id+"F6.wireOp",EDGE,"E29.24.0.3");Q6=makeQuery(id+"F6.imprint","IMPRINT",FACE,{"disambiguationData":[TD([[makeQuery(id+"F6.imprint","IMPRINT",EDGE,{"derivedFrom":subQ5}),-1.0]])]});}
            var Q7;
            {var subQ0=sQuery(id+"F6.wireOp",EDGE,"E27.1.0.2");Q7=makeQuery(id+"F6.imprint","IMPRINT",FACE,{"disambiguationData":[TD([[makeQuery(id+"F6.imprint","IMPRINT",EDGE,{"derivedFrom":subQ0}),-1.0]])]});}
            var Q8;
            Q8=makeQuery(id+"F6.imprint","IMPRINT",FACE,{"disambiguationData":[TD([[makeQuery(id+"F6.imprint","IMPRINT",EDGE,{"derivedFrom":sQuery(id+"F6.wireOp",EDGE,"E27.1.1.0")}),-1.0]])]});
            var Q9;
            Q9=makeQuery(id+"F6.imprint","IMPRINT",FACE,{"disambiguationData":[TD([[makeQuery(id+"F6.imprint","IMPRINT",EDGE,{"derivedFrom":sQuery(id+"F6.wireOp",EDGE,"E28.0.1.2")}),-1.0]])]});
            var Q10;
            {var subQ5=sQuery(id+"F6.wireOp",EDGE,"E27.1.0.11");Q10=makeQuery(id+"F6.imprint","IMPRINT",FACE,{"disambiguationData":[TD([[makeQuery(id+"F6.imprint","IMPRINT",EDGE,{"derivedFrom":subQ5}),-1.0]])]});}
            var Q11;
            Q11=makeQuery(id+"F6.imprint","IMPRINT",FACE,{"disambiguationData":[TD([[makeQuery(id+"F6.imprint","IMPRINT",EDGE,{"derivedFrom":sQuery(id+"F6.wireOp",EDGE,"E27.1.1.6")}),-1.0]])]});
            var Q12;
            Q12=makeQuery(id+"F6.imprint","IMPRINT",FACE,{"disambiguationData":[TD([[makeQuery(id+"F6.imprint","IMPRINT",EDGE,{"derivedFrom":sQuery(id+"F6.wireOp",EDGE,"E28.18.1.2")}),-1.0]])]});
            var Q13;
            {var subQ5=sQuery(id+"F6.wireOp",EDGE,"E29.24.1.3");Q13=makeQuery(id+"F6.imprint","IMPRINT",FACE,{"disambiguationData":[TD([[makeQuery(id+"F6.imprint","IMPRINT",EDGE,{"derivedFrom":subQ5}),-1.0]])]});}
            var Q14;
            {var subQ5=sQuery(id+"F6.wireOp",EDGE,"E27.2.0.2");Q14=makeQuery(id+"F6.imprint","IMPRINT",FACE,{"disambiguationData":[TD([[makeQuery(id+"F6.imprint","IMPRINT",EDGE,{"derivedFrom":subQ5}),-1.0]])]});}
            var Q15;
            Q15=makeQuery(id+"F6.imprint","IMPRINT",FACE,{"disambiguationData":[TD([[makeQuery(id+"F6.imprint","IMPRINT",EDGE,{"derivedFrom":sQuery(id+"F6.wireOp",EDGE,"E27.2.1.0")}),-1.0]])]});
            var Q16;
            Q16=makeQuery(id+"F6.imprint","IMPRINT",FACE,{"disambiguationData":[TD([[makeQuery(id+"F6.imprint","IMPRINT",EDGE,{"derivedFrom":sQuery(id+"F6.wireOp",EDGE,"E28.0.2.2")}),-1.0]])]});
            var Q17;
            {var subQ5=sQuery(id+"F6.wireOp",EDGE,"E27.2.0.11");Q17=makeQuery(id+"F6.imprint","IMPRINT",FACE,{"disambiguationData":[TD([[makeQuery(id+"F6.imprint","IMPRINT",EDGE,{"derivedFrom":subQ5}),-1.0]])]});}
            var Q18;
            Q18=makeQuery(id+"F6.imprint","IMPRINT",FACE,{"disambiguationData":[TD([[makeQuery(id+"F6.imprint","IMPRINT",EDGE,{"derivedFrom":sQuery(id+"F6.wireOp",EDGE,"E27.2.1.6")}),-1.0]])]});
            var Q19;
            Q19=makeQuery(id+"F6.imprint","IMPRINT",FACE,{"disambiguationData":[TD([[makeQuery(id+"F6.imprint","IMPRINT",EDGE,{"derivedFrom":sQuery(id+"F6.wireOp",EDGE,"E28.18.2.2")}),-1.0]])]});
            var Q20;
            {var subQ5=sQuery(id+"F6.wireOp",EDGE,"E29.24.2.3");Q20=makeQuery(id+"F6.imprint","IMPRINT",FACE,{"disambiguationData":[TD([[makeQuery(id+"F6.imprint","IMPRINT",EDGE,{"derivedFrom":subQ5}),-1.0]])]});}
            var Q21;
            {var subQ0=sQuery(id+"F6.wireOp",EDGE,"E30.6.3.0");Q21=makeQuery(id+"F6.imprint","IMPRINT",FACE,{"disambiguationData":[TD([[makeQuery(id+"F6.imprint","IMPRINT",EDGE,{"derivedFrom":subQ0}),-1.0]])]});}
            var Q22;
            Q22=makeQuery(id+"F6.imprint","IMPRINT",FACE,{"disambiguationData":[TD([[makeQuery(id+"F6.imprint","IMPRINT",EDGE,{"derivedFrom":sQuery(id+"F6.wireOp",EDGE,"E30.0.3.1")}),-1.0]])]});
            var Q23;
            Q23=makeQuery(id+"F6.imprint","IMPRINT",FACE,{"disambiguationData":[TD([[makeQuery(id+"F6.imprint","IMPRINT",EDGE,{"derivedFrom":sQuery(id+"F6.wireOp",EDGE,"E30.0.3.2")}),-1.0]])]});
            var Q24;
            {var subQ5=sQuery(id+"F6.wireOp",EDGE,"E30.33.3.0");Q24=makeQuery(id+"F6.imprint","IMPRINT",FACE,{"disambiguationData":[TD([[makeQuery(id+"F6.imprint","IMPRINT",EDGE,{"derivedFrom":subQ5}),-1.0]])]});}
            var Q25;
            Q25=makeQuery(id+"F6.imprint","IMPRINT",FACE,{"disambiguationData":[TD([[makeQuery(id+"F6.imprint","IMPRINT",EDGE,{"derivedFrom":sQuery(id+"F6.wireOp",EDGE,"E30.18.3.1")}),-1.0]])]});
            var Q26;
            Q26=makeQuery(id+"F6.imprint","IMPRINT",FACE,{"disambiguationData":[TD([[makeQuery(id+"F6.imprint","IMPRINT",EDGE,{"derivedFrom":sQuery(id+"F6.wireOp",EDGE,"E30.18.3.2")}),-1.0]])]});
            var Q27;
            {var subQ5=sQuery(id+"F6.wireOp",EDGE,"E30.24.3.3");Q27=makeQuery(id+"F6.imprint","IMPRINT",FACE,{"disambiguationData":[TD([[makeQuery(id+"F6.imprint","IMPRINT",EDGE,{"derivedFrom":subQ5}),-1.0]])]});}
            var Q28;
            {var subQ0=sQuery(id+"F6.wireOp",EDGE,"E30.6.4.0");Q28=makeQuery(id+"F6.imprint","IMPRINT",FACE,{"disambiguationData":[TD([[makeQuery(id+"F6.imprint","IMPRINT",EDGE,{"derivedFrom":subQ0}),-1.0]])]});}
            var Q29;
            Q29=makeQuery(id+"F6.imprint","IMPRINT",FACE,{"disambiguationData":[TD([[makeQuery(id+"F6.imprint","IMPRINT",EDGE,{"derivedFrom":sQuery(id+"F6.wireOp",EDGE,"E30.0.4.1")}),-1.0]])]});
            var Q30;
            Q30=makeQuery(id+"F6.imprint","IMPRINT",FACE,{"disambiguationData":[TD([[makeQuery(id+"F6.imprint","IMPRINT",EDGE,{"derivedFrom":sQuery(id+"F6.wireOp",EDGE,"E30.0.4.2")}),-1.0]])]});
            var Q31;
            {var subQ5=sQuery(id+"F6.wireOp",EDGE,"E30.33.4.0");Q31=makeQuery(id+"F6.imprint","IMPRINT",FACE,{"disambiguationData":[TD([[makeQuery(id+"F6.imprint","IMPRINT",EDGE,{"derivedFrom":subQ5}),-1.0]])]});}
            var Q32;
            Q32=makeQuery(id+"F6.imprint","IMPRINT",FACE,{"disambiguationData":[TD([[makeQuery(id+"F6.imprint","IMPRINT",EDGE,{"derivedFrom":sQuery(id+"F6.wireOp",EDGE,"E30.18.4.1")}),-1.0]])]});
            var Q33;
            Q33=makeQuery(id+"F6.imprint","IMPRINT",FACE,{"disambiguationData":[TD([[makeQuery(id+"F6.imprint","IMPRINT",EDGE,{"derivedFrom":sQuery(id+"F6.wireOp",EDGE,"E30.18.4.2")}),-1.0]])]});
            var Q34;
            {var subQ5=sQuery(id+"F6.wireOp",EDGE,"E30.24.4.3");Q34=makeQuery(id+"F6.imprint","IMPRINT",FACE,{"disambiguationData":[TD([[makeQuery(id+"F6.imprint","IMPRINT",EDGE,{"derivedFrom":subQ5}),-1.0]])]});}
            var Q35;
            {var subQ0=sQuery(id+"F6.wireOp",EDGE,"E30.6.5.0");Q35=makeQuery(id+"F6.imprint","IMPRINT",FACE,{"disambiguationData":[TD([[makeQuery(id+"F6.imprint","IMPRINT",EDGE,{"derivedFrom":subQ0}),-1.0]])]});}
            var Q36;
            Q36=makeQuery(id+"F6.imprint","IMPRINT",FACE,{"disambiguationData":[TD([[makeQuery(id+"F6.imprint","IMPRINT",EDGE,{"derivedFrom":sQuery(id+"F6.wireOp",EDGE,"E30.0.5.1")}),-1.0]])]});
            var Q37;
            Q37=makeQuery(id+"F6.imprint","IMPRINT",FACE,{"disambiguationData":[TD([[makeQuery(id+"F6.imprint","IMPRINT",EDGE,{"derivedFrom":sQuery(id+"F6.wireOp",EDGE,"E30.0.5.2")}),-1.0]])]});
            var Q38;
            {var subQ5=sQuery(id+"F6.wireOp",EDGE,"E30.33.5.0");Q38=makeQuery(id+"F6.imprint","IMPRINT",FACE,{"disambiguationData":[TD([[makeQuery(id+"F6.imprint","IMPRINT",EDGE,{"derivedFrom":subQ5}),-1.0]])]});}
            var Q39;
            Q39=makeQuery(id+"F6.imprint","IMPRINT",FACE,{"disambiguationData":[TD([[makeQuery(id+"F6.imprint","IMPRINT",EDGE,{"derivedFrom":sQuery(id+"F6.wireOp",EDGE,"E30.18.5.1")}),-1.0]])]});
            var Q40;
            Q40=makeQuery(id+"F6.imprint","IMPRINT",FACE,{"disambiguationData":[TD([[makeQuery(id+"F6.imprint","IMPRINT",EDGE,{"derivedFrom":sQuery(id+"F6.wireOp",EDGE,"E30.18.5.2")}),-1.0]])]});
            var Q41;
            {var subQ5=sQuery(id+"F6.wireOp",EDGE,"E30.24.5.3");Q41=makeQuery(id+"F6.imprint","IMPRINT",FACE,{"disambiguationData":[TD([[makeQuery(id+"F6.imprint","IMPRINT",EDGE,{"derivedFrom":subQ5}),-1.0]])]});}
            var Q42;
            {var subQ0=sQuery(id+"F6.wireOp",EDGE,"E30.6.6.0");Q42=makeQuery(id+"F6.imprint","IMPRINT",FACE,{"disambiguationData":[TD([[makeQuery(id+"F6.imprint","IMPRINT",EDGE,{"derivedFrom":subQ0}),-1.0]])]});}
            var Q43;
            Q43=makeQuery(id+"F6.imprint","IMPRINT",FACE,{"disambiguationData":[TD([[makeQuery(id+"F6.imprint","IMPRINT",EDGE,{"derivedFrom":sQuery(id+"F6.wireOp",EDGE,"E30.0.6.1")}),-1.0]])]});
            var Q44;
            Q44=makeQuery(id+"F6.imprint","IMPRINT",FACE,{"disambiguationData":[TD([[makeQuery(id+"F6.imprint","IMPRINT",EDGE,{"derivedFrom":sQuery(id+"F6.wireOp",EDGE,"E30.0.6.2")}),-1.0]])]});
            var Q45;
            {var subQ5=sQuery(id+"F6.wireOp",EDGE,"E30.33.6.0");Q45=makeQuery(id+"F6.imprint","IMPRINT",FACE,{"disambiguationData":[TD([[makeQuery(id+"F6.imprint","IMPRINT",EDGE,{"derivedFrom":subQ5}),-1.0]])]});}
            var Q46;
            Q46=makeQuery(id+"F6.imprint","IMPRINT",FACE,{"disambiguationData":[TD([[makeQuery(id+"F6.imprint","IMPRINT",EDGE,{"derivedFrom":sQuery(id+"F6.wireOp",EDGE,"E30.18.6.1")}),-1.0]])]});
            var Q47;
            Q47=makeQuery(id+"F6.imprint","IMPRINT",FACE,{"disambiguationData":[TD([[makeQuery(id+"F6.imprint","IMPRINT",EDGE,{"derivedFrom":sQuery(id+"F6.wireOp",EDGE,"E30.18.6.2")}),-1.0]])]});
            var Q48;
            {var subQ5=sQuery(id+"F6.wireOp",EDGE,"E30.24.6.3");Q48=makeQuery(id+"F6.imprint","IMPRINT",FACE,{"disambiguationData":[TD([[makeQuery(id+"F6.imprint","IMPRINT",EDGE,{"derivedFrom":subQ5}),-1.0]])]});}
            var Q49;
            {var subQ0=sQuery(id+"F6.wireOp",EDGE,"E30.6.7.0");Q49=makeQuery(id+"F6.imprint","IMPRINT",FACE,{"disambiguationData":[TD([[makeQuery(id+"F6.imprint","IMPRINT",EDGE,{"derivedFrom":subQ0}),-1.0]])]});}
            var Q50;
            Q50=makeQuery(id+"F6.imprint","IMPRINT",FACE,{"disambiguationData":[TD([[makeQuery(id+"F6.imprint","IMPRINT",EDGE,{"derivedFrom":sQuery(id+"F6.wireOp",EDGE,"E30.0.7.1")}),-1.0]])]});
            var Q51;
            Q51=makeQuery(id+"F6.imprint","IMPRINT",FACE,{"disambiguationData":[TD([[makeQuery(id+"F6.imprint","IMPRINT",EDGE,{"derivedFrom":sQuery(id+"F6.wireOp",EDGE,"E30.0.7.2")}),-1.0]])]});
            var Q52;
            {var subQ5=sQuery(id+"F6.wireOp",EDGE,"E30.33.7.0");Q52=makeQuery(id+"F6.imprint","IMPRINT",FACE,{"disambiguationData":[TD([[makeQuery(id+"F6.imprint","IMPRINT",EDGE,{"derivedFrom":subQ5}),-1.0]])]});}
            var Q53;
            Q53=makeQuery(id+"F6.imprint","IMPRINT",FACE,{"disambiguationData":[TD([[makeQuery(id+"F6.imprint","IMPRINT",EDGE,{"derivedFrom":sQuery(id+"F6.wireOp",EDGE,"E30.18.7.1")}),-1.0]])]});
            var Q54;
            Q54=makeQuery(id+"F6.imprint","IMPRINT",FACE,{"disambiguationData":[TD([[makeQuery(id+"F6.imprint","IMPRINT",EDGE,{"derivedFrom":sQuery(id+"F6.wireOp",EDGE,"E30.18.7.2")}),-1.0]])]});
            var Q55;
            {var subQ5=sQuery(id+"F6.wireOp",EDGE,"E30.24.7.3");Q55=makeQuery(id+"F6.imprint","IMPRINT",FACE,{"disambiguationData":[TD([[makeQuery(id+"F6.imprint","IMPRINT",EDGE,{"derivedFrom":subQ5}),-1.0]])]});}
            var Q56;
            {var subQ0=sQuery(id+"F6.wireOp",EDGE,"E30.6.8.0");Q56=makeQuery(id+"F6.imprint","IMPRINT",FACE,{"disambiguationData":[TD([[makeQuery(id+"F6.imprint","IMPRINT",EDGE,{"derivedFrom":subQ0}),-1.0]])]});}
            var Q57;
            Q57=makeQuery(id+"F6.imprint","IMPRINT",FACE,{"disambiguationData":[TD([[makeQuery(id+"F6.imprint","IMPRINT",EDGE,{"derivedFrom":sQuery(id+"F6.wireOp",EDGE,"E30.0.8.1")}),-1.0]])]});
            var Q58;
            Q58=makeQuery(id+"F6.imprint","IMPRINT",FACE,{"disambiguationData":[TD([[makeQuery(id+"F6.imprint","IMPRINT",EDGE,{"derivedFrom":sQuery(id+"F6.wireOp",EDGE,"E30.0.8.2")}),-1.0]])]});
            var Q59;
            {var subQ5=sQuery(id+"F6.wireOp",EDGE,"E30.33.8.0");Q59=makeQuery(id+"F6.imprint","IMPRINT",FACE,{"disambiguationData":[TD([[makeQuery(id+"F6.imprint","IMPRINT",EDGE,{"derivedFrom":subQ5}),-1.0]])]});}
            var Q60;
            Q60=makeQuery(id+"F6.imprint","IMPRINT",FACE,{"disambiguationData":[TD([[makeQuery(id+"F6.imprint","IMPRINT",EDGE,{"derivedFrom":sQuery(id+"F6.wireOp",EDGE,"E30.18.8.1")}),-1.0]])]});
            var Q61;
            Q61=makeQuery(id+"F6.imprint","IMPRINT",FACE,{"disambiguationData":[TD([[makeQuery(id+"F6.imprint","IMPRINT",EDGE,{"derivedFrom":sQuery(id+"F6.wireOp",EDGE,"E30.18.8.2")}),-1.0]])]});
            var Q62;
            {var subQ5=sQuery(id+"F6.wireOp",EDGE,"E30.24.8.3");Q62=makeQuery(id+"F6.imprint","IMPRINT",FACE,{"disambiguationData":[TD([[makeQuery(id+"F6.imprint","IMPRINT",EDGE,{"derivedFrom":subQ5}),-1.0]])]});}
            var Q63;
            {var subQ0=sQuery(id+"F6.wireOp",EDGE,"E30.6.9.0");Q63=makeQuery(id+"F6.imprint","IMPRINT",FACE,{"disambiguationData":[TD([[makeQuery(id+"F6.imprint","IMPRINT",EDGE,{"derivedFrom":subQ0}),-1.0]])]});}
            var Q64;
            Q64=makeQuery(id+"F6.imprint","IMPRINT",FACE,{"disambiguationData":[TD([[makeQuery(id+"F6.imprint","IMPRINT",EDGE,{"derivedFrom":sQuery(id+"F6.wireOp",EDGE,"E30.0.9.1")}),-1.0]])]});
            var Q65;
            Q65=makeQuery(id+"F6.imprint","IMPRINT",FACE,{"disambiguationData":[TD([[makeQuery(id+"F6.imprint","IMPRINT",EDGE,{"derivedFrom":sQuery(id+"F6.wireOp",EDGE,"E30.0.9.2")}),-1.0]])]});
            var Q66;
            {var subQ5=sQuery(id+"F6.wireOp",EDGE,"E30.33.9.0");Q66=makeQuery(id+"F6.imprint","IMPRINT",FACE,{"disambiguationData":[TD([[makeQuery(id+"F6.imprint","IMPRINT",EDGE,{"derivedFrom":subQ5}),-1.0]])]});}
            var Q67;
            Q67=makeQuery(id+"F6.imprint","IMPRINT",FACE,{"disambiguationData":[TD([[makeQuery(id+"F6.imprint","IMPRINT",EDGE,{"derivedFrom":sQuery(id+"F6.wireOp",EDGE,"E30.18.9.1")}),-1.0]])]});
            var Q68;
            Q68=makeQuery(id+"F6.imprint","IMPRINT",FACE,{"disambiguationData":[TD([[makeQuery(id+"F6.imprint","IMPRINT",EDGE,{"derivedFrom":sQuery(id+"F6.wireOp",EDGE,"E30.18.9.2")}),-1.0]])]});
            var Q69;
            {var subQ5=sQuery(id+"F6.wireOp",EDGE,"E30.24.9.3");Q69=makeQuery(id+"F6.imprint","IMPRINT",FACE,{"disambiguationData":[TD([[makeQuery(id+"F6.imprint","IMPRINT",EDGE,{"derivedFrom":subQ5}),-1.0]])]});}
            var Q70;
            {var subQ0=sQuery(id+"F6.wireOp",EDGE,"E31.6.10.0");Q70=makeQuery(id+"F6.imprint","IMPRINT",FACE,{"disambiguationData":[TD([[makeQuery(id+"F6.imprint","IMPRINT",EDGE,{"derivedFrom":subQ0}),-1.0]])]});}
            var Q71;
            Q71=makeQuery(id+"F6.imprint","IMPRINT",FACE,{"disambiguationData":[TD([[makeQuery(id+"F6.imprint","IMPRINT",EDGE,{"derivedFrom":sQuery(id+"F6.wireOp",EDGE,"E31.0.10.1")}),-1.0]])]});
            var Q72;
            Q72=makeQuery(id+"F6.imprint","IMPRINT",FACE,{"disambiguationData":[TD([[makeQuery(id+"F6.imprint","IMPRINT",EDGE,{"derivedFrom":sQuery(id+"F6.wireOp",EDGE,"E31.0.10.2")}),-1.0]])]});
            var Q73;
            {var subQ5=sQuery(id+"F6.wireOp",EDGE,"E31.33.10.0");Q73=makeQuery(id+"F6.imprint","IMPRINT",FACE,{"disambiguationData":[TD([[makeQuery(id+"F6.imprint","IMPRINT",EDGE,{"derivedFrom":subQ5}),-1.0]])]});}
            var Q74;
            Q74=makeQuery(id+"F6.imprint","IMPRINT",FACE,{"disambiguationData":[TD([[makeQuery(id+"F6.imprint","IMPRINT",EDGE,{"derivedFrom":sQuery(id+"F6.wireOp",EDGE,"E31.18.10.1")}),-1.0]])]});
            var Q75;
            Q75=makeQuery(id+"F6.imprint","IMPRINT",FACE,{"disambiguationData":[TD([[makeQuery(id+"F6.imprint","IMPRINT",EDGE,{"derivedFrom":sQuery(id+"F6.wireOp",EDGE,"E31.18.10.2")}),-1.0]])]});
            var Q76;
            {var subQ5=sQuery(id+"F6.wireOp",EDGE,"E31.24.10.3");Q76=makeQuery(id+"F6.imprint","IMPRINT",FACE,{"disambiguationData":[TD([[makeQuery(id+"F6.imprint","IMPRINT",EDGE,{"derivedFrom":subQ5}),-1.0]])]});}
            var Q77;
            {var subQ0=sQuery(id+"F6.wireOp",EDGE,"E31.6.11.0");Q77=makeQuery(id+"F6.imprint","IMPRINT",FACE,{"disambiguationData":[TD([[makeQuery(id+"F6.imprint","IMPRINT",EDGE,{"derivedFrom":subQ0}),-1.0]])]});}
            var Q78;
            Q78=makeQuery(id+"F6.imprint","IMPRINT",FACE,{"disambiguationData":[TD([[makeQuery(id+"F6.imprint","IMPRINT",EDGE,{"derivedFrom":sQuery(id+"F6.wireOp",EDGE,"E31.0.11.1")}),-1.0]])]});
            var Q79;
            Q79=makeQuery(id+"F6.imprint","IMPRINT",FACE,{"disambiguationData":[TD([[makeQuery(id+"F6.imprint","IMPRINT",EDGE,{"derivedFrom":sQuery(id+"F6.wireOp",EDGE,"E31.0.11.2")}),-1.0]])]});
            var Q80;
            {var subQ5=sQuery(id+"F6.wireOp",EDGE,"E31.33.11.0");Q80=makeQuery(id+"F6.imprint","IMPRINT",FACE,{"disambiguationData":[TD([[makeQuery(id+"F6.imprint","IMPRINT",EDGE,{"derivedFrom":subQ5}),-1.0]])]});}
            var Q81;
            Q81=makeQuery(id+"F6.imprint","IMPRINT",FACE,{"disambiguationData":[TD([[makeQuery(id+"F6.imprint","IMPRINT",EDGE,{"derivedFrom":sQuery(id+"F6.wireOp",EDGE,"E31.18.11.1")}),-1.0]])]});
            var Q82;
            Q82=makeQuery(id+"F6.imprint","IMPRINT",FACE,{"disambiguationData":[TD([[makeQuery(id+"F6.imprint","IMPRINT",EDGE,{"derivedFrom":sQuery(id+"F6.wireOp",EDGE,"E31.18.11.2")}),-1.0]])]});
            var Q83;
            {var subQ5=sQuery(id+"F6.wireOp",EDGE,"E31.24.11.3");Q83=makeQuery(id+"F6.imprint","IMPRINT",FACE,{"disambiguationData":[TD([[makeQuery(id+"F6.imprint","IMPRINT",EDGE,{"derivedFrom":subQ5}),-1.0]])]});}
            var Q84;
            {var subQ0=sQuery(id+"F6.wireOp",EDGE,"E31.6.12.0");Q84=makeQuery(id+"F6.imprint","IMPRINT",FACE,{"disambiguationData":[TD([[makeQuery(id+"F6.imprint","IMPRINT",EDGE,{"derivedFrom":subQ0}),-1.0]])]});}
            var Q85;
            Q85=makeQuery(id+"F6.imprint","IMPRINT",FACE,{"disambiguationData":[TD([[makeQuery(id+"F6.imprint","IMPRINT",EDGE,{"derivedFrom":sQuery(id+"F6.wireOp",EDGE,"E31.0.12.1")}),-1.0]])]});
            var Q86;
            Q86=makeQuery(id+"F6.imprint","IMPRINT",FACE,{"disambiguationData":[TD([[makeQuery(id+"F6.imprint","IMPRINT",EDGE,{"derivedFrom":sQuery(id+"F6.wireOp",EDGE,"E31.0.12.2")}),-1.0]])]});
            var Q87;
            {var subQ5=sQuery(id+"F6.wireOp",EDGE,"E31.33.12.0");Q87=makeQuery(id+"F6.imprint","IMPRINT",FACE,{"disambiguationData":[TD([[makeQuery(id+"F6.imprint","IMPRINT",EDGE,{"derivedFrom":subQ5}),-1.0]])]});}
            var Q88;
            Q88=makeQuery(id+"F6.imprint","IMPRINT",FACE,{"disambiguationData":[TD([[makeQuery(id+"F6.imprint","IMPRINT",EDGE,{"derivedFrom":sQuery(id+"F6.wireOp",EDGE,"E31.18.12.1")}),-1.0]])]});
            var Q89;
            Q89=makeQuery(id+"F6.imprint","IMPRINT",FACE,{"disambiguationData":[TD([[makeQuery(id+"F6.imprint","IMPRINT",EDGE,{"derivedFrom":sQuery(id+"F6.wireOp",EDGE,"E31.18.12.2")}),-1.0]])]});
            var Q90;
            {var subQ5=sQuery(id+"F6.wireOp",EDGE,"E31.24.12.3");Q90=makeQuery(id+"F6.imprint","IMPRINT",FACE,{"disambiguationData":[TD([[makeQuery(id+"F6.imprint","IMPRINT",EDGE,{"derivedFrom":subQ5}),-1.0]])]});}
            var Q91;
            {var subQ0=sQuery(id+"F6.wireOp",EDGE,"E31.6.13.0");Q91=makeQuery(id+"F6.imprint","IMPRINT",FACE,{"disambiguationData":[TD([[makeQuery(id+"F6.imprint","IMPRINT",EDGE,{"derivedFrom":subQ0}),-1.0]])]});}
            var Q92;
            Q92=makeQuery(id+"F6.imprint","IMPRINT",FACE,{"disambiguationData":[TD([[makeQuery(id+"F6.imprint","IMPRINT",EDGE,{"derivedFrom":sQuery(id+"F6.wireOp",EDGE,"E31.0.13.1")}),-1.0]])]});
            var Q93;
            Q93=makeQuery(id+"F6.imprint","IMPRINT",FACE,{"disambiguationData":[TD([[makeQuery(id+"F6.imprint","IMPRINT",EDGE,{"derivedFrom":sQuery(id+"F6.wireOp",EDGE,"E31.0.13.2")}),-1.0]])]});
            var Q94;
            {var subQ5=sQuery(id+"F6.wireOp",EDGE,"E31.33.13.0");Q94=makeQuery(id+"F6.imprint","IMPRINT",FACE,{"disambiguationData":[TD([[makeQuery(id+"F6.imprint","IMPRINT",EDGE,{"derivedFrom":subQ5}),-1.0]])]});}
            var Q95;
            Q95=makeQuery(id+"F6.imprint","IMPRINT",FACE,{"disambiguationData":[TD([[makeQuery(id+"F6.imprint","IMPRINT",EDGE,{"derivedFrom":sQuery(id+"F6.wireOp",EDGE,"E31.18.13.1")}),-1.0]])]});
            var Q96;
            Q96=makeQuery(id+"F6.imprint","IMPRINT",FACE,{"disambiguationData":[TD([[makeQuery(id+"F6.imprint","IMPRINT",EDGE,{"derivedFrom":sQuery(id+"F6.wireOp",EDGE,"E31.18.13.2")}),-1.0]])]});
            var Q97;
            {var subQ5=sQuery(id+"F6.wireOp",EDGE,"E31.24.13.3");Q97=makeQuery(id+"F6.imprint","IMPRINT",FACE,{"disambiguationData":[TD([[makeQuery(id+"F6.imprint","IMPRINT",EDGE,{"derivedFrom":subQ5}),-1.0]])]});}
            var Q98;
            {var subQ0=sQuery(id+"F6.wireOp",EDGE,"E31.6.14.0");Q98=makeQuery(id+"F6.imprint","IMPRINT",FACE,{"disambiguationData":[TD([[makeQuery(id+"F6.imprint","IMPRINT",EDGE,{"derivedFrom":subQ0}),-1.0]])]});}
            var Q99;
            Q99=makeQuery(id+"F6.imprint","IMPRINT",FACE,{"disambiguationData":[TD([[makeQuery(id+"F6.imprint","IMPRINT",EDGE,{"derivedFrom":sQuery(id+"F6.wireOp",EDGE,"E31.0.14.1")}),-1.0]])]});
            var Q100;
            Q100=makeQuery(id+"F6.imprint","IMPRINT",FACE,{"disambiguationData":[TD([[makeQuery(id+"F6.imprint","IMPRINT",EDGE,{"derivedFrom":sQuery(id+"F6.wireOp",EDGE,"E31.0.14.2")}),-1.0]])]});
            var Q101;
            {var subQ5=sQuery(id+"F6.wireOp",EDGE,"E31.33.14.0");Q101=makeQuery(id+"F6.imprint","IMPRINT",FACE,{"disambiguationData":[TD([[makeQuery(id+"F6.imprint","IMPRINT",EDGE,{"derivedFrom":subQ5}),-1.0]])]});}
            var Q102;
            Q102=makeQuery(id+"F6.imprint","IMPRINT",FACE,{"disambiguationData":[TD([[makeQuery(id+"F6.imprint","IMPRINT",EDGE,{"derivedFrom":sQuery(id+"F6.wireOp",EDGE,"E31.18.14.1")}),-1.0]])]});
            var Q103;
            Q103=makeQuery(id+"F6.imprint","IMPRINT",FACE,{"disambiguationData":[TD([[makeQuery(id+"F6.imprint","IMPRINT",EDGE,{"derivedFrom":sQuery(id+"F6.wireOp",EDGE,"E31.18.14.2")}),-1.0]])]});
            var Q104;
            {var subQ5=sQuery(id+"F6.wireOp",EDGE,"E31.24.14.3");Q104=makeQuery(id+"F6.imprint","IMPRINT",FACE,{"disambiguationData":[TD([[makeQuery(id+"F6.imprint","IMPRINT",EDGE,{"derivedFrom":subQ5}),-1.0]])]});}
            var Q105;
            {var subQ0=sQuery(id+"F6.wireOp",EDGE,"E31.6.15.0");Q105=makeQuery(id+"F6.imprint","IMPRINT",FACE,{"disambiguationData":[TD([[makeQuery(id+"F6.imprint","IMPRINT",EDGE,{"derivedFrom":subQ0}),-1.0]])]});}
            var Q106;
            Q106=makeQuery(id+"F6.imprint","IMPRINT",FACE,{"disambiguationData":[TD([[makeQuery(id+"F6.imprint","IMPRINT",EDGE,{"derivedFrom":sQuery(id+"F6.wireOp",EDGE,"E31.0.15.1")}),-1.0]])]});
            var Q107;
            Q107=makeQuery(id+"F6.imprint","IMPRINT",FACE,{"disambiguationData":[TD([[makeQuery(id+"F6.imprint","IMPRINT",EDGE,{"derivedFrom":sQuery(id+"F6.wireOp",EDGE,"E31.0.15.2")}),-1.0]])]});
            var Q108;
            {var subQ5=sQuery(id+"F6.wireOp",EDGE,"E31.33.15.0");Q108=makeQuery(id+"F6.imprint","IMPRINT",FACE,{"disambiguationData":[TD([[makeQuery(id+"F6.imprint","IMPRINT",EDGE,{"derivedFrom":subQ5}),-1.0]])]});}
            var Q109;
            Q109=makeQuery(id+"F6.imprint","IMPRINT",FACE,{"disambiguationData":[TD([[makeQuery(id+"F6.imprint","IMPRINT",EDGE,{"derivedFrom":sQuery(id+"F6.wireOp",EDGE,"E31.18.15.1")}),-1.0]])]});
            var Q110;
            Q110=makeQuery(id+"F6.imprint","IMPRINT",FACE,{"disambiguationData":[TD([[makeQuery(id+"F6.imprint","IMPRINT",EDGE,{"derivedFrom":sQuery(id+"F6.wireOp",EDGE,"E31.18.15.2")}),-1.0]])]});
            var Q111;
            {var subQ5=sQuery(id+"F6.wireOp",EDGE,"E31.24.15.3");Q111=makeQuery(id+"F6.imprint","IMPRINT",FACE,{"disambiguationData":[TD([[makeQuery(id+"F6.imprint","IMPRINT",EDGE,{"derivedFrom":subQ5}),-1.0]])]});}
            var Q112;
            Q112=makeQuery(id+"F3.opSweep","SWEPT_FACE",FACE,{"disambiguationData":[OSD([sQuery(id+"F0.wireOp",EDGE,"E0.bottom"),sQuery(id+"F2.wireOp",EDGE,"E6.right")])]});
            extrude(context, id + "F7", {"entities" : qUnion([Q0, Q1, Q2, Q3, Q4, Q5, Q6, Q7, Q8, Q9, Q10, Q11, Q12, Q13, Q14, Q15, Q16, Q17, Q18, Q19, Q20, Q21, Q22, Q23, Q24, Q25, Q26, Q27, Q28, Q29, Q30, Q31, Q32, Q33, Q34, Q35, Q36, Q37, Q38, Q39, Q40, Q41, Q42, Q43, Q44, Q45, Q46, Q47, Q48, Q49, Q50, Q51, Q52, Q53, Q54, Q55, Q56, Q57, Q58, Q59, Q60, Q61, Q62, Q63, Q64, Q65, Q66, Q67, Q68, Q69, Q70, Q71, Q72, Q73, Q74, Q75, Q76, Q77, Q78, Q79, Q80, Q81, Q82, Q83, Q84, Q85, Q86, Q87, Q88, Q89, Q90, Q91, Q92, Q93, Q94, Q95, Q96, Q97, Q98, Q99, Q100, Q101, Q102, Q103, Q104, Q105, Q106, Q107, Q108, Q109, Q110, Q111]), "operationType" : NewBodyOperationType.REMOVE, "endBound" : BoundingType.UP_TO_SURFACE, "oppositeDirection" : true, "depth" : 25 * mm, "endBoundEntityFace" : qUnion([Q112]), "offsetDistance" : 25 * mm});
        }
    });
